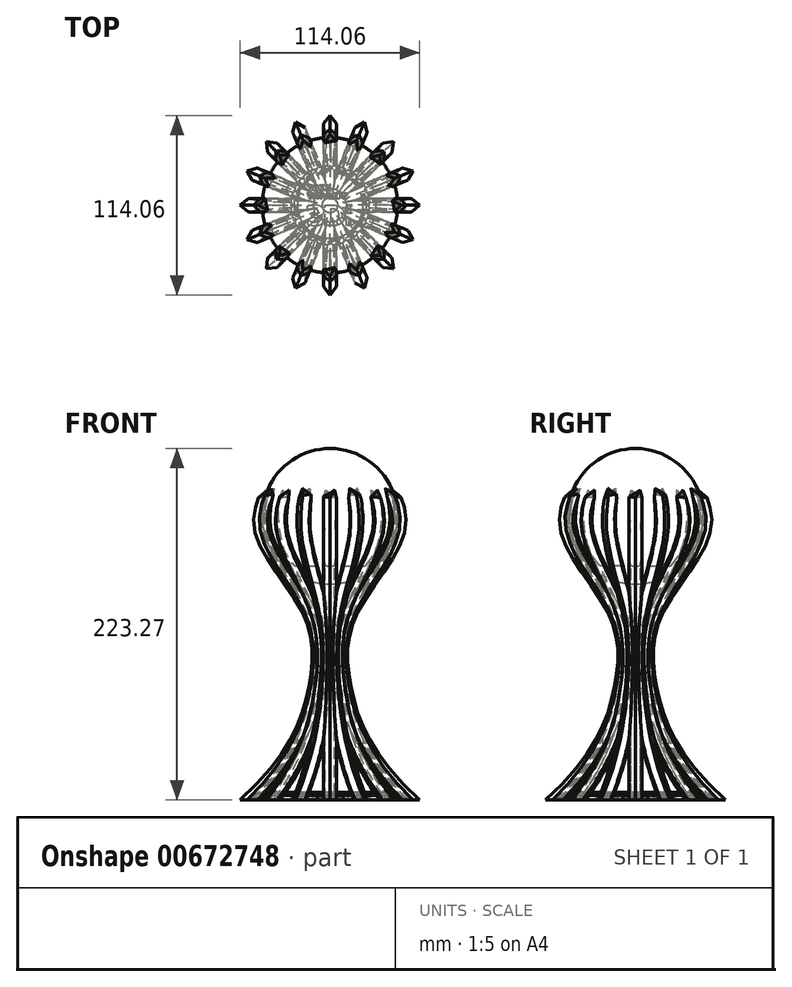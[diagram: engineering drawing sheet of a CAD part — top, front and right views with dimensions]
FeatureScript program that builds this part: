
annotation { "Feature Type Name" : "Feature", "Feature Type Description" : "" }
export const myFeature = defineFeature(function(context is Context, id is Id, definition is map)
    precondition{}
    {
        {
            var Q0;
            Q0=qCreatedBy(makeId("Front.planeOp"),FACE);
            var sketch = newSketch(context, id + "F0", { "sketchPlane" : qUnion([Q0])});
            skCircle(sketch, "E0", {"center": v(-0.22, 180.27) * mm, "radius": 43 * mm});
            skLineSegment(sketch, "E1", {"start": v(-0.22, 249.8) * mm, "end": v(-0.22, -3.53) * mm, "construction": true});
            skLineSegment(sketch, "E2", {"start": v(94.67, 200) * mm, "end": v(-91.24, 200) * mm, "construction": true});
            skFitSpline(sketch, "E3", {"points": [v(-37.53, 197.97) * mm, v(-44.72, 173.88) * mm, v(-14.42, 119.99) * mm, v(-10.02, 72.07) * mm, v(-52.16, 0) * mm], "startDerivative": vector(-55.72, -57.4) * mm, "endDerivative": vector(-278.7, -261.6) * mm});
            skLineSegment(sketch, "E4", {"start": v(-0.22, 180.27) * mm, "end": v(-70.32, 183.44) * mm, "construction": true});
            skLineSegment(sketch, "E5", {"start": v(-0.22, 223.27) * mm, "end": v(-0.22, 137.27) * mm});
            skSolve(sketch);
        }
        {
            var Q0;
            Q0=qCreatedBy(makeId("Top.planeOp"),FACE);
            var sketch = newSketch(context, id + "F1", { "sketchPlane" : qUnion([Q0])});
            skPoint(sketch, "E6.0", {"position": v(-52.16, 0) * mm});
            skCircle(sketch, "E7", {"center": v(0, 0) * mm, "radius": 52.16 * mm, "construction": true});
            skLineSegment(sketch, "E8", {"start": v(-50.09, -4.18) * mm, "end": v(-52, -4.18) * mm});
            skLineSegment(sketch, "E9", {"start": v(-52, -4.18) * mm, "end": v(-57.25, 0) * mm});
            skLineSegment(sketch, "E10", {"start": v(-49.1, 0) * mm, "end": v(-61.73, 0) * mm, "construction": true});
            skLineSegment(sketch, "E11.MirrorCS", {"start": v(-50.09, 4.18) * mm, "end": v(-52, 4.18) * mm});
            skLineSegment(sketch, "E12.MirrorCS", {"start": v(-52, 4.18) * mm, "end": v(-57.25, 0) * mm});
            skLineSegment(sketch, "E13", {"start": v(-50.09, -4.18) * mm, "end": v(-47.88, -3.04) * mm});
            skLineSegment(sketch, "E14", {"start": v(-47.88, -3.04) * mm, "end": v(-47.88, 0) * mm});
            skLineSegment(sketch, "E15.MirrorCS", {"start": v(-47.88, 3.04) * mm, "end": v(-47.88, 0) * mm});
            skLineSegment(sketch, "E16.MirrorCS", {"start": v(-50.09, 4.18) * mm, "end": v(-47.88, 3.04) * mm});
            skPoint(sketch, "E17.start.orphan", {"position": v(-51.12, 0) * mm});
            skPoint(sketch, "E18.MirrorCS.end.orphan", {"position": v(-50.09, 4.18) * mm});
            skSolve(sketch);
        }
        {
            var Q0;
            Q0=makeQuery(id+"F1.imprint","IMPRINT",FACE,{"disambiguationData":[TD([[makeQuery(id+"F1.imprint","IMPRINT",EDGE,{"derivedFrom":sQuery(id+"F1.wireOp",EDGE,"E8")}),-1.0]])]});
            var Q1;
            Q1=sQuery(id+"F0.wireOp",EDGE,"E3");
            sweep(context, id + "F2", {"profiles" : qUnion([Q0]), "path" : qUnion([Q1])});
        }
        {
            var Q0;
            Q0=makeQuery(id+"F2.opSweep","SWEPT_BODY",BODY,{"disambiguationData":[OSD([sQuery(id+"F0.wireOp",EDGE,"E3"),sQuery(id+"F1.wireOp",EDGE,"DaZxr78I-HaZT-GVOq-y3KG-bkiKTm5bVj2K"),sQuery(id+"F1.wireOp",EDGE,"ID9TlmXJ-H8h3-IZLx-eHvp-f0HMO6DgMMxN"),sQuery(id+"F1.wireOp",EDGE,"5A4HRRGu-b9xE-CkS7-00Gs-tnyZgG4T912Z"),sQuery(id+"F1.wireOp",EDGE,"uolo1fji-ynfm-Myvc-62LO-FXYa9UhFNky3"),sQuery(id+"F1.wireOp",EDGE,"E17"),sQuery(id+"F1.wireOp",EDGE,"E8"),sQuery(id+"F1.wireOp",EDGE,"E9")])]});
            var Q1;
            Q1=sQuery(id+"F0.wireOp",EDGE,"E1");
            circularPattern(context, id + "F3", {"operationType" : NewBodyOperationType.ADD, "entities" : qUnion([Q0]), "axis" : qUnion([Q1]), "angle" : 360 * degree, "instanceCount" : 16, "equalSpace" : true, "isCentered" : true});
        }
        {
            var Q0;
            {var subQ2=sQuery(id+"F0.wireOp",EDGE,"E5");Q0=makeQuery(id+"F0.imprint","IMPRINT",FACE,{"disambiguationData":[TD([[makeQuery(id+"F0.imprint","IMPRINT",EDGE,{"derivedFrom":subQ2}),-1.0]])]});}
            var Q1;
            Q1=sQuery(id+"F0.wireOp",EDGE,"E1");
            revolve(context, id + "F4", {"entities" : qUnion([Q0]), "axis" : qUnion([Q1]), "revolveType" : RevolveType.FULL});
        }
        {
            var Q0;
            Q0=makeQuery(id+"F3.opPattern","COPY",EDGE,{"derivedFrom":makeQuery(id+"F2.opSweep","CAP_EDGE",EDGE,{"disambiguationData":[OSD([sQuery(id+"F0.wireOp",VERTEX,"E3.start"),sQuery(id+"F1.wireOp",EDGE,"E9")])],"isStart":false}),"instanceName":"-7"});
            var Q1;
            Q1=makeQuery(id+"F3.opPattern","COPY",EDGE,{"derivedFrom":makeQuery(id+"F2.opSweep","CAP_EDGE",EDGE,{"disambiguationData":[OSD([sQuery(id+"F0.wireOp",VERTEX,"E3.start"),sQuery(id+"F1.wireOp",EDGE,"E9")])],"isStart":false}),"instanceName":"-9"});
            var Q2;
            Q2=makeQuery(id+"F3.opPattern","COPY",EDGE,{"derivedFrom":makeQuery(id+"F2.opSweep","CAP_EDGE",EDGE,{"disambiguationData":[OSD([sQuery(id+"F0.wireOp",VERTEX,"E3.start"),sQuery(id+"F1.wireOp",EDGE,"E9")])],"isStart":false}),"instanceName":"-11"});
            var Q3;
            Q3=makeQuery(id+"F3.opPattern","COPY",EDGE,{"derivedFrom":makeQuery(id+"F2.opSweep","CAP_EDGE",EDGE,{"disambiguationData":[OSD([sQuery(id+"F0.wireOp",VERTEX,"E3.start"),sQuery(id+"F1.wireOp",EDGE,"E9")])],"isStart":false}),"instanceName":"-13"});
            var Q4;
            Q4=makeQuery(id+"F3.opPattern","COPY",EDGE,{"derivedFrom":makeQuery(id+"F2.opSweep","CAP_EDGE",EDGE,{"disambiguationData":[OSD([sQuery(id+"F0.wireOp",VERTEX,"E3.start"),sQuery(id+"F1.wireOp",EDGE,"E9")])],"isStart":false}),"instanceName":"-15"});
            var Q5;
            Q5=makeQuery(id+"F3.opPattern","COPY",EDGE,{"derivedFrom":makeQuery(id+"F2.opSweep","CAP_EDGE",EDGE,{"disambiguationData":[OSD([sQuery(id+"F0.wireOp",VERTEX,"E3.start"),sQuery(id+"F1.wireOp",EDGE,"E9")])],"isStart":false}),"instanceName":"-1"});
            var Q6;
            Q6=makeQuery(id+"F3.opPattern","COPY",EDGE,{"derivedFrom":makeQuery(id+"F2.opSweep","CAP_EDGE",EDGE,{"disambiguationData":[OSD([sQuery(id+"F0.wireOp",VERTEX,"E3.start"),sQuery(id+"F1.wireOp",EDGE,"E9")])],"isStart":false}),"instanceName":"-3"});
            var Q7;
            Q7=makeQuery(id+"F3.opPattern","COPY",EDGE,{"derivedFrom":makeQuery(id+"F2.opSweep","CAP_EDGE",EDGE,{"disambiguationData":[OSD([sQuery(id+"F0.wireOp",VERTEX,"E3.start"),sQuery(id+"F1.wireOp",EDGE,"E9")])],"isStart":false}),"instanceName":"-5"});
            chamfer(context, id + "F5", {"entities" : qUnion([Q0, Q1, Q2, Q3, Q4, Q5, Q6, Q7]), "width" : 6 * mm, "tangentPropagation" : true});
        }
        {
            var Q0;
            Q0=makeQuery(id+"F3.opPattern","COPY",EDGE,{"derivedFrom":makeQuery(id+"F2.opSweep","CAP_EDGE",EDGE,{"disambiguationData":[OSD([sQuery(id+"F0.wireOp",VERTEX,"E3.start"),sQuery(id+"F1.wireOp",EDGE,"E12.MirrorCS")])],"isStart":false}),"instanceName":"-4"});
            var Q1;
            Q1=makeQuery(id+"F3.opPattern","COPY",EDGE,{"derivedFrom":makeQuery(id+"F2.opSweep","CAP_EDGE",EDGE,{"disambiguationData":[OSD([sQuery(id+"F0.wireOp",VERTEX,"E3.start"),sQuery(id+"F1.wireOp",EDGE,"E12.MirrorCS")])],"isStart":false}),"instanceName":"-6"});
            var Q2;
            Q2=makeQuery(id+"F3.opPattern","COPY",EDGE,{"derivedFrom":makeQuery(id+"F2.opSweep","CAP_EDGE",EDGE,{"disambiguationData":[OSD([sQuery(id+"F0.wireOp",VERTEX,"E3.start"),sQuery(id+"F1.wireOp",EDGE,"E12.MirrorCS")])],"isStart":false}),"instanceName":"-8"});
            var Q3;
            Q3=makeQuery(id+"F3.opPattern","COPY",EDGE,{"derivedFrom":makeQuery(id+"F2.opSweep","CAP_EDGE",EDGE,{"disambiguationData":[OSD([sQuery(id+"F0.wireOp",VERTEX,"E3.start"),sQuery(id+"F1.wireOp",EDGE,"E12.MirrorCS")])],"isStart":false}),"instanceName":"-10"});
            var Q4;
            Q4=makeQuery(id+"F3.opPattern","COPY",EDGE,{"derivedFrom":makeQuery(id+"F2.opSweep","CAP_EDGE",EDGE,{"disambiguationData":[OSD([sQuery(id+"F0.wireOp",VERTEX,"E3.start"),sQuery(id+"F1.wireOp",EDGE,"E12.MirrorCS")])],"isStart":false}),"instanceName":"-12"});
            var Q5;
            Q5=makeQuery(id+"F3.opPattern","COPY",EDGE,{"derivedFrom":makeQuery(id+"F2.opSweep","CAP_EDGE",EDGE,{"disambiguationData":[OSD([sQuery(id+"F0.wireOp",VERTEX,"E3.start"),sQuery(id+"F1.wireOp",EDGE,"E12.MirrorCS")])],"isStart":false}),"instanceName":"-14"});
            var Q6;
            Q6=makeQuery(id+"F2.opSweep","CAP_EDGE",EDGE,{"disambiguationData":[OSD([sQuery(id+"F0.wireOp",VERTEX,"E3.start"),sQuery(id+"F1.wireOp",EDGE,"E12.MirrorCS")])],"isStart":false});
            var Q7;
            Q7=makeQuery(id+"F3.opPattern","COPY",EDGE,{"derivedFrom":makeQuery(id+"F2.opSweep","CAP_EDGE",EDGE,{"disambiguationData":[OSD([sQuery(id+"F0.wireOp",VERTEX,"E3.start"),sQuery(id+"F1.wireOp",EDGE,"E12.MirrorCS")])],"isStart":false}),"instanceName":"-2"});
            chamfer(context, id + "F6", {"entities" : qUnion([Q0, Q1, Q2, Q3, Q4, Q5, Q6, Q7]), "width" : 8 * mm, "tangentPropagation" : true});
        }
        {
            var Q0;
            Q0=qCreatedBy(makeId("Top.planeOp"),FACE);
            var sketch = newSketch(context, id + "F7", { "sketchPlane" : qUnion([Q0])});
            skArc(sketch, "E19", {"start": v(-24.95, -1.58) * mm, "mid": v(-24.52, -4.88) * mm, "end": v(-23.66, -8.09) * mm});
            skPoint(sketch, "E20.0", {"position": v(-52.16, 0) * mm});
            skCircle(sketch, "E21.cCircle", {"center": v(0, 0) * mm, "radius": 52.16 * mm, "construction": true});
            skLineSegment(sketch, "E21.0", {"start": v(-52.16, 0) * mm, "end": v(-48.19, 19.96) * mm});
            skLineSegment(sketch, "E21.1", {"start": v(-48.19, 19.96) * mm, "end": v(-36.88, 36.88) * mm});
            skLineSegment(sketch, "E21.2", {"start": v(-36.88, 36.88) * mm, "end": v(-19.96, 48.19) * mm});
            skLineSegment(sketch, "E21.3", {"start": v(-19.96, 48.19) * mm, "end": v(0, 52.16) * mm});
            skLineSegment(sketch, "E21.4", {"start": v(0, 52.16) * mm, "end": v(19.96, 48.19) * mm});
            skLineSegment(sketch, "E21.5", {"start": v(19.96, 48.19) * mm, "end": v(36.88, 36.88) * mm});
            skLineSegment(sketch, "E21.6", {"start": v(36.88, 36.88) * mm, "end": v(48.19, 19.96) * mm});
            skLineSegment(sketch, "E21.7", {"start": v(48.19, 19.96) * mm, "end": v(52.16, 0) * mm});
            skLineSegment(sketch, "E21.8", {"start": v(52.16, 0) * mm, "end": v(48.19, -19.96) * mm});
            skLineSegment(sketch, "E21.9", {"start": v(48.19, -19.96) * mm, "end": v(36.88, -36.88) * mm});
            skLineSegment(sketch, "E21.10", {"start": v(36.88, -36.88) * mm, "end": v(19.96, -48.19) * mm});
            skLineSegment(sketch, "E21.11", {"start": v(19.96, -48.19) * mm, "end": v(0, -52.16) * mm});
            skLineSegment(sketch, "E21.12", {"start": v(0, -52.16) * mm, "end": v(-19.96, -48.19) * mm});
            skLineSegment(sketch, "E21.13", {"start": v(-19.96, -48.19) * mm, "end": v(-36.88, -36.88) * mm});
            skLineSegment(sketch, "E21.14", {"start": v(-36.88, -36.88) * mm, "end": v(-48.19, -19.96) * mm});
            skLineSegment(sketch, "E21.15", {"start": v(-48.19, -19.96) * mm, "end": v(-52.16, 0) * mm});
            skPoint(sketch, "E22.0", {"position": v(-47.88, 3.04) * mm});
            skPoint(sketch, "E23.0", {"position": v(-47.88, -3.04) * mm});
            skPoint(sketch, "E24.0", {"position": v(-47.88, 0) * mm});
            skLineSegment(sketch, "E25", {"start": v(-47.88, 3.04) * mm, "end": v(-24.95, 1.58) * mm});
            skLineSegment(sketch, "E26", {"start": v(-47.88, -3.04) * mm, "end": v(-24.95, -1.58) * mm});
            skLineSegment(sketch, "E27", {"start": v(-47.88, 3.04) * mm, "end": v(-52.16, 0) * mm});
            skLineSegment(sketch, "E28", {"start": v(-52.16, 0) * mm, "end": v(-47.88, -3.04) * mm});
            skCircle(sketch, "E29", {"center": v(0, 0) * mm, "radius": 21 * mm});
            skLineSegment(sketch, "E30.1.0", {"start": v(-45.4, -15.52) * mm, "end": v(-23.66, -8.09) * mm});
            skLineSegment(sketch, "E30.1.1", {"start": v(-45.4, -15.52) * mm, "end": v(-48.19, -19.96) * mm});
            skLineSegment(sketch, "E30.1.2", {"start": v(-48.19, -19.96) * mm, "end": v(-43.08, -21.13) * mm});
            skLineSegment(sketch, "E30.1.3", {"start": v(-43.08, -21.13) * mm, "end": v(-22.45, -11) * mm});
            skLineSegment(sketch, "E30.2.0", {"start": v(-36, -31.71) * mm, "end": v(-18.76, -16.52) * mm});
            skLineSegment(sketch, "E30.2.1", {"start": v(-36, -31.71) * mm, "end": v(-36.88, -36.88) * mm});
            skLineSegment(sketch, "E30.2.2", {"start": v(-36.88, -36.88) * mm, "end": v(-31.71, -36) * mm});
            skLineSegment(sketch, "E30.2.3", {"start": v(-31.71, -36) * mm, "end": v(-16.52, -18.76) * mm});
            skLineSegment(sketch, "E30.3.0", {"start": v(-21.13, -43.08) * mm, "end": v(-11, -22.45) * mm});
            skLineSegment(sketch, "E30.3.1", {"start": v(-21.13, -43.08) * mm, "end": v(-19.96, -48.19) * mm});
            skLineSegment(sketch, "E30.3.2", {"start": v(-19.96, -48.19) * mm, "end": v(-15.52, -45.4) * mm});
            skLineSegment(sketch, "E30.3.3", {"start": v(-15.52, -45.4) * mm, "end": v(-8.09, -23.66) * mm});
            skLineSegment(sketch, "E30.4.0", {"start": v(-3.04, -47.88) * mm, "end": v(-1.58, -24.95) * mm});
            skLineSegment(sketch, "E30.4.1", {"start": v(-3.04, -47.88) * mm, "end": v(0, -52.16) * mm});
            skLineSegment(sketch, "E30.4.2", {"start": v(0, -52.16) * mm, "end": v(3.04, -47.88) * mm});
            skLineSegment(sketch, "E30.4.3", {"start": v(3.04, -47.88) * mm, "end": v(1.58, -24.95) * mm});
            skLineSegment(sketch, "E30.5.0", {"start": v(15.52, -45.4) * mm, "end": v(8.09, -23.66) * mm});
            skLineSegment(sketch, "E30.5.1", {"start": v(15.52, -45.4) * mm, "end": v(19.96, -48.19) * mm});
            skLineSegment(sketch, "E30.5.2", {"start": v(19.96, -48.19) * mm, "end": v(21.13, -43.08) * mm});
            skLineSegment(sketch, "E30.5.3", {"start": v(21.13, -43.08) * mm, "end": v(11, -22.45) * mm});
            skLineSegment(sketch, "E30.6.0", {"start": v(31.71, -36) * mm, "end": v(16.52, -18.76) * mm});
            skLineSegment(sketch, "E30.6.1", {"start": v(31.71, -36) * mm, "end": v(36.88, -36.88) * mm});
            skLineSegment(sketch, "E30.6.2", {"start": v(36.88, -36.88) * mm, "end": v(36, -31.71) * mm});
            skLineSegment(sketch, "E30.6.3", {"start": v(36, -31.71) * mm, "end": v(18.76, -16.52) * mm});
            skLineSegment(sketch, "E30.7.0", {"start": v(43.08, -21.13) * mm, "end": v(22.45, -11) * mm});
            skLineSegment(sketch, "E30.7.1", {"start": v(43.08, -21.13) * mm, "end": v(48.19, -19.96) * mm});
            skLineSegment(sketch, "E30.7.2", {"start": v(48.19, -19.96) * mm, "end": v(45.4, -15.52) * mm});
            skLineSegment(sketch, "E30.7.3", {"start": v(45.4, -15.52) * mm, "end": v(23.66, -8.09) * mm});
            skLineSegment(sketch, "E30.8.0", {"start": v(47.88, -3.04) * mm, "end": v(24.95, -1.58) * mm});
            skLineSegment(sketch, "E30.8.1", {"start": v(47.88, -3.04) * mm, "end": v(52.16, 0) * mm});
            skLineSegment(sketch, "E30.8.2", {"start": v(52.16, 0) * mm, "end": v(47.88, 3.04) * mm});
            skLineSegment(sketch, "E30.8.3", {"start": v(47.88, 3.04) * mm, "end": v(24.95, 1.58) * mm});
            skLineSegment(sketch, "E30.9.0", {"start": v(45.4, 15.52) * mm, "end": v(23.66, 8.09) * mm});
            skLineSegment(sketch, "E30.9.1", {"start": v(45.4, 15.52) * mm, "end": v(48.19, 19.96) * mm});
            skLineSegment(sketch, "E30.9.2", {"start": v(48.19, 19.96) * mm, "end": v(43.08, 21.13) * mm});
            skLineSegment(sketch, "E30.9.3", {"start": v(43.08, 21.13) * mm, "end": v(22.45, 11) * mm});
            skLineSegment(sketch, "E30.10.0", {"start": v(36, 31.71) * mm, "end": v(18.76, 16.52) * mm});
            skLineSegment(sketch, "E30.10.1", {"start": v(36, 31.71) * mm, "end": v(36.88, 36.88) * mm});
            skLineSegment(sketch, "E30.10.2", {"start": v(36.88, 36.88) * mm, "end": v(31.71, 36) * mm});
            skLineSegment(sketch, "E30.10.3", {"start": v(31.71, 36) * mm, "end": v(16.52, 18.76) * mm});
            skLineSegment(sketch, "E30.11.0", {"start": v(21.13, 43.08) * mm, "end": v(11, 22.45) * mm});
            skLineSegment(sketch, "E30.11.1", {"start": v(21.13, 43.08) * mm, "end": v(19.96, 48.19) * mm});
            skLineSegment(sketch, "E30.11.2", {"start": v(19.96, 48.19) * mm, "end": v(15.52, 45.4) * mm});
            skLineSegment(sketch, "E30.11.3", {"start": v(15.52, 45.4) * mm, "end": v(8.09, 23.66) * mm});
            skLineSegment(sketch, "E30.12.0", {"start": v(3.04, 47.88) * mm, "end": v(1.58, 24.95) * mm});
            skLineSegment(sketch, "E30.12.1", {"start": v(3.04, 47.88) * mm, "end": v(0, 52.16) * mm});
            skLineSegment(sketch, "E30.12.2", {"start": v(0, 52.16) * mm, "end": v(-3.04, 47.88) * mm});
            skLineSegment(sketch, "E30.12.3", {"start": v(-3.04, 47.88) * mm, "end": v(-1.58, 24.95) * mm});
            skLineSegment(sketch, "E30.13.0", {"start": v(-15.52, 45.4) * mm, "end": v(-8.09, 23.66) * mm});
            skLineSegment(sketch, "E30.13.1", {"start": v(-15.52, 45.4) * mm, "end": v(-19.96, 48.19) * mm});
            skLineSegment(sketch, "E30.13.2", {"start": v(-19.96, 48.19) * mm, "end": v(-21.13, 43.08) * mm});
            skLineSegment(sketch, "E30.13.3", {"start": v(-21.13, 43.08) * mm, "end": v(-11, 22.45) * mm});
            skLineSegment(sketch, "E30.14.0", {"start": v(-31.71, 36) * mm, "end": v(-16.52, 18.76) * mm});
            skLineSegment(sketch, "E30.14.1", {"start": v(-31.71, 36) * mm, "end": v(-36.88, 36.88) * mm});
            skLineSegment(sketch, "E30.14.2", {"start": v(-36.88, 36.88) * mm, "end": v(-36, 31.71) * mm});
            skLineSegment(sketch, "E30.14.3", {"start": v(-36, 31.71) * mm, "end": v(-18.76, 16.52) * mm});
            skLineSegment(sketch, "E30.15.0", {"start": v(-43.08, 21.13) * mm, "end": v(-22.45, 11) * mm});
            skLineSegment(sketch, "E30.15.1", {"start": v(-43.08, 21.13) * mm, "end": v(-48.19, 19.96) * mm});
            skLineSegment(sketch, "E30.15.2", {"start": v(-48.19, 19.96) * mm, "end": v(-45.4, 15.52) * mm});
            skLineSegment(sketch, "E30.15.3", {"start": v(-45.4, 15.52) * mm, "end": v(-23.66, 8.09) * mm});
            skArc(sketch, "E31.trimOffspring", {"start": v(-23.66, 8.09) * mm, "mid": v(-24.52, 4.88) * mm, "end": v(-24.95, 1.58) * mm});
            skArc(sketch, "E32.trimOffspring", {"start": v(-18.76, 16.52) * mm, "mid": v(-20.79, 13.89) * mm, "end": v(-22.45, 11) * mm});
            skArc(sketch, "E33.trimOffspring", {"start": v(-11, 22.45) * mm, "mid": v(-13.89, 20.79) * mm, "end": v(-16.52, 18.76) * mm});
            skArc(sketch, "E34.trimOffspring", {"start": v(-1.58, 24.95) * mm, "mid": v(-4.88, 24.52) * mm, "end": v(-8.09, 23.66) * mm});
            skArc(sketch, "E35.trimOffspring", {"start": v(8.09, 23.66) * mm, "mid": v(4.88, 24.52) * mm, "end": v(1.58, 24.95) * mm});
            skArc(sketch, "E36.trimOffspring", {"start": v(16.52, 18.76) * mm, "mid": v(13.89, 20.79) * mm, "end": v(11, 22.45) * mm});
            skArc(sketch, "E37.trimOffspring", {"start": v(22.45, 11) * mm, "mid": v(20.79, 13.89) * mm, "end": v(18.76, 16.52) * mm});
            skArc(sketch, "E38.trimOffspring", {"start": v(24.95, 1.58) * mm, "mid": v(24.52, 4.88) * mm, "end": v(23.66, 8.09) * mm});
            skArc(sketch, "E39.trimOffspring", {"start": v(23.66, -8.09) * mm, "mid": v(24.52, -4.88) * mm, "end": v(24.95, -1.58) * mm});
            skArc(sketch, "E40.trimOffspring", {"start": v(18.76, -16.52) * mm, "mid": v(20.79, -13.89) * mm, "end": v(22.45, -11) * mm});
            skArc(sketch, "E41.trimOffspring", {"start": v(11, -22.45) * mm, "mid": v(13.89, -20.79) * mm, "end": v(16.52, -18.76) * mm});
            skArc(sketch, "E42.trimOffspring", {"start": v(1.58, -24.95) * mm, "mid": v(4.88, -24.52) * mm, "end": v(8.09, -23.66) * mm});
            skArc(sketch, "E43.trimOffspring", {"start": v(-8.09, -23.66) * mm, "mid": v(-4.88, -24.52) * mm, "end": v(-1.58, -24.95) * mm});
            skArc(sketch, "E44.trimOffspring", {"start": v(-16.52, -18.76) * mm, "mid": v(-13.89, -20.79) * mm, "end": v(-11, -22.45) * mm});
            skArc(sketch, "E45.trimOffspring", {"start": v(-22.45, -11) * mm, "mid": v(-20.79, -13.89) * mm, "end": v(-18.76, -16.52) * mm});
            skSolve(sketch);
        }
        {
            var Q0;
            Q0=makeQuery(id+"F7.imprint","IMPRINT",FACE,{"disambiguationData":[TD([[makeQuery(id+"F7.imprint","IMPRINT",EDGE,{"derivedFrom":sQuery(id+"F7.wireOp",EDGE,"E19")}),1.0]])]});
            extrude(context, id + "F8", {"entities" : qUnion([Q0]), "operationType" : NewBodyOperationType.ADD, "depth" : 3 * mm, "offsetDistance" : 25 * mm, "hasDraft" : true, "draftAngle" : 3.8 * degree});
        }
        {
            var Q0;
            Q0=makeQuery(id+"F8.opExtrude","CAP_FACE",FACE,{"disambiguationData":[OSD([sQuery(id+"F7.wireOp",EDGE,"E19"),sQuery(id+"F7.wireOp",EDGE,"E25"),sQuery(id+"F7.wireOp",EDGE,"E26"),sQuery(id+"F7.wireOp",EDGE,"E27"),sQuery(id+"F7.wireOp",EDGE,"E28"),sQuery(id+"F7.wireOp",EDGE,"E29"),sQuery(id+"F7.wireOp",EDGE,"E30.1.0"),sQuery(id+"F7.wireOp",EDGE,"E30.1.1"),sQuery(id+"F7.wireOp",EDGE,"E30.1.2"),sQuery(id+"F7.wireOp",EDGE,"E30.1.3"),sQuery(id+"F7.wireOp",EDGE,"E30.2.0"),sQuery(id+"F7.wireOp",EDGE,"E30.2.1"),sQuery(id+"F7.wireOp",EDGE,"E30.2.2"),sQuery(id+"F7.wireOp",EDGE,"E30.2.3"),sQuery(id+"F7.wireOp",EDGE,"E30.3.0"),sQuery(id+"F7.wireOp",EDGE,"E30.3.1"),sQuery(id+"F7.wireOp",EDGE,"E30.3.2"),sQuery(id+"F7.wireOp",EDGE,"E30.3.3"),sQuery(id+"F7.wireOp",EDGE,"E30.4.0"),sQuery(id+"F7.wireOp",EDGE,"E30.4.1"),sQuery(id+"F7.wireOp",EDGE,"E30.4.2"),sQuery(id+"F7.wireOp",EDGE,"E30.4.3"),sQuery(id+"F7.wireOp",EDGE,"E30.5.0"),sQuery(id+"F7.wireOp",EDGE,"E30.5.1"),sQuery(id+"F7.wireOp",EDGE,"E30.5.2"),sQuery(id+"F7.wireOp",EDGE,"E30.5.3"),sQuery(id+"F7.wireOp",EDGE,"E30.6.0"),sQuery(id+"F7.wireOp",EDGE,"E30.6.1"),sQuery(id+"F7.wireOp",EDGE,"E30.6.2"),sQuery(id+"F7.wireOp",EDGE,"E30.6.3"),sQuery(id+"F7.wireOp",EDGE,"E30.7.0"),sQuery(id+"F7.wireOp",EDGE,"E30.7.1"),sQuery(id+"F7.wireOp",EDGE,"E30.7.2"),sQuery(id+"F7.wireOp",EDGE,"E30.7.3"),sQuery(id+"F7.wireOp",EDGE,"E30.8.0"),sQuery(id+"F7.wireOp",EDGE,"E30.8.1"),sQuery(id+"F7.wireOp",EDGE,"E30.8.2"),sQuery(id+"F7.wireOp",EDGE,"E30.8.3"),sQuery(id+"F7.wireOp",EDGE,"E30.9.0"),sQuery(id+"F7.wireOp",EDGE,"E30.9.1"),sQuery(id+"F7.wireOp",EDGE,"E30.9.2"),sQuery(id+"F7.wireOp",EDGE,"E30.9.3"),sQuery(id+"F7.wireOp",EDGE,"E30.10.0"),sQuery(id+"F7.wireOp",EDGE,"E30.10.1"),sQuery(id+"F7.wireOp",EDGE,"E30.10.2"),sQuery(id+"F7.wireOp",EDGE,"E30.10.3"),sQuery(id+"F7.wireOp",EDGE,"E30.11.0"),sQuery(id+"F7.wireOp",EDGE,"E30.11.1"),sQuery(id+"F7.wireOp",EDGE,"E30.11.2"),sQuery(id+"F7.wireOp",EDGE,"E30.11.3"),sQuery(id+"F7.wireOp",EDGE,"E30.12.0"),sQuery(id+"F7.wireOp",EDGE,"E30.12.1"),sQuery(id+"F7.wireOp",EDGE,"E30.12.2"),sQuery(id+"F7.wireOp",EDGE,"E30.12.3"),sQuery(id+"F7.wireOp",EDGE,"E30.13.0"),sQuery(id+"F7.wireOp",EDGE,"E30.13.1"),sQuery(id+"F7.wireOp",EDGE,"E30.13.2"),sQuery(id+"F7.wireOp",EDGE,"E30.13.3"),sQuery(id+"F7.wireOp",EDGE,"E30.14.0"),sQuery(id+"F7.wireOp",EDGE,"E30.14.1"),sQuery(id+"F7.wireOp",EDGE,"E30.14.2"),sQuery(id+"F7.wireOp",EDGE,"E30.14.3"),sQuery(id+"F7.wireOp",EDGE,"E30.15.0"),sQuery(id+"F7.wireOp",EDGE,"E30.15.1"),sQuery(id+"F7.wireOp",EDGE,"E30.15.2"),sQuery(id+"F7.wireOp",EDGE,"E30.15.3"),sQuery(id+"F7.wireOp",EDGE,"E31.trimOffspring"),sQuery(id+"F7.wireOp",EDGE,"E32.trimOffspring"),sQuery(id+"F7.wireOp",EDGE,"E33.trimOffspring"),sQuery(id+"F7.wireOp",EDGE,"E34.trimOffspring"),sQuery(id+"F7.wireOp",EDGE,"E35.trimOffspring"),sQuery(id+"F7.wireOp",EDGE,"E36.trimOffspring"),sQuery(id+"F7.wireOp",EDGE,"E37.trimOffspring"),sQuery(id+"F7.wireOp",EDGE,"E38.trimOffspring"),sQuery(id+"F7.wireOp",EDGE,"E39.trimOffspring"),sQuery(id+"F7.wireOp",EDGE,"E40.trimOffspring"),sQuery(id+"F7.wireOp",EDGE,"E41.trimOffspring"),sQuery(id+"F7.wireOp",EDGE,"E42.trimOffspring"),sQuery(id+"F7.wireOp",EDGE,"E43.trimOffspring"),sQuery(id+"F7.wireOp",EDGE,"E44.trimOffspring"),sQuery(id+"F7.wireOp",EDGE,"E45.trimOffspring")])],"isStart":false});
            extrude(context, id + "F9", {"entities" : qUnion([Q0]), "operationType" : NewBodyOperationType.ADD, "depth" : 2 * mm, "offsetDistance" : 25 * mm, "hasDraft" : true, "draftAngle" : 50 * degree, "draftPullDirection" : true});
        }
        {
            var Q0;
            Q0=makeQuery(id+"F8.opExtrude","CAP_EDGE",EDGE,{"disambiguationData":[OSD([sQuery(id+"F7.wireOp",EDGE,"E29")])],"isStart":true});
            chamfer(context, id + "F10", {"entities" : qUnion([Q0]), "chamferType" : ChamferType.TWO_OFFSETS, "width1" : 1 * mm, "oppositeDirection" : false, "width2" : 2 * mm, "tangentPropagation" : true});
        }
        {
            var Q0;
            Q0=makeQuery(id+"F4.opRevolve","SWEPT_BODY",BODY,{"disambiguationData":[OSD([sQuery(id+"F0.wireOp",EDGE,"E0"),sQuery(id+"F0.wireOp",EDGE,"0JXTtzD2-2VzW-rgRp-cltN-5Cip2ue7kMV8")])]});
            var Q1;
            Q1=makeQuery(id+"F2.opSweep","SWEPT_BODY",BODY,{"disambiguationData":[OSD([sQuery(id+"F0.wireOp",EDGE,"E3"),sQuery(id+"F1.wireOp",EDGE,"E8"),sQuery(id+"F1.wireOp",EDGE,"E9"),sQuery(id+"F1.wireOp",EDGE,"E11.MirrorCS"),sQuery(id+"F1.wireOp",EDGE,"E12.MirrorCS"),sQuery(id+"F1.wireOp",EDGE,"E13"),sQuery(id+"F1.wireOp",EDGE,"E14"),sQuery(id+"F1.wireOp",EDGE,"E15.MirrorCS"),sQuery(id+"F1.wireOp",EDGE,"E16.MirrorCS")])]});
            booleanBodies(context, id + "F11", {"operationType" : BooleanOperationType.SUBTRACTION, "tools" : qUnion([Q0]), "targets" : qUnion([Q1]), "keepTools" : true});
        }
        {
            var Q0;
            Q0=qCreatedBy(makeId("Top.planeOp"),FACE);
            var sketch = newSketch(context, id + "F12", { "sketchPlane" : qUnion([Q0])});
            skCircle(sketch, "E46.0", {"center": v(0, 0) * mm, "radius": 22 * mm});
            skSolve(sketch);
        }
        {
            var Q0;
            Q0=makeQuery(id+"F12.imprint","IMPRINT",FACE,{"disambiguationData":[TD([[makeQuery(id+"F12.imprint","IMPRINT",EDGE,{"derivedFrom":sQuery(id+"F12.wireOp",EDGE,"E46.0")}),1.0]])]});
            extrude(context, id + "F13", {"entities" : qUnion([Q0]), "depth" : 3 * mm, "offsetDistance" : 25 * mm});
        }
        {
            var Q0;
            Q0=makeQuery(id+"F2.opSweep","SWEPT_BODY",BODY,{"disambiguationData":[OSD([sQuery(id+"F0.wireOp",EDGE,"E3"),sQuery(id+"F1.wireOp",EDGE,"E8"),sQuery(id+"F1.wireOp",EDGE,"E9"),sQuery(id+"F1.wireOp",EDGE,"E11.MirrorCS"),sQuery(id+"F1.wireOp",EDGE,"E12.MirrorCS"),sQuery(id+"F1.wireOp",EDGE,"E13"),sQuery(id+"F1.wireOp",EDGE,"E14"),sQuery(id+"F1.wireOp",EDGE,"E15.MirrorCS"),sQuery(id+"F1.wireOp",EDGE,"E16.MirrorCS")])]});
            var Q1;
            Q1=makeQuery(id+"F13.opExtrude","SWEPT_BODY",BODY,{"disambiguationData":[OSD([sQuery(id+"F12.wireOp",EDGE,"E46.0")])]});
            booleanBodies(context, id + "F14", {"operationType" : BooleanOperationType.SUBTRACTION, "tools" : qUnion([Q0]), "targets" : qUnion([Q1]), "keepTools" : true});
        }
        {
            var Q0;
            {var subQ0=sQuery(id+"F7.wireOp",EDGE,"E29");Q0=makeQuery(id+"F14.opBoolean","COPY",EDGE,{"derivedFrom":makeQuery(id+"F9.boolean.opBoolean","MERGE",EDGE,{"derivedFrom":[makeQuery(id+"F8.opExtrude","CAP_EDGE",EDGE,{"disambiguationData":[OSD([subQ0])],"isStart":false}),makeQuery(id+"F9.opExtrude","CAP_EDGE",EDGE,{"disambiguationData":[OSD([subQ0])],"isStart":true})]})});}
            var Q1;
            {var subQ0=sQuery(id+"F7.wireOp",EDGE,"E29");var subQ1=makeQuery(id+"F2.opSweep","CAP_FACE",FACE,{"disambiguationData":[OSD([sQuery(id+"F0.wireOp",VERTEX,"E3.end"),sQuery(id+"F1.wireOp",EDGE,"E8"),sQuery(id+"F1.wireOp",EDGE,"E9"),sQuery(id+"F1.wireOp",EDGE,"E11.MirrorCS"),sQuery(id+"F1.wireOp",EDGE,"E12.MirrorCS"),sQuery(id+"F1.wireOp",EDGE,"E13"),sQuery(id+"F1.wireOp",EDGE,"E14"),sQuery(id+"F1.wireOp",EDGE,"E15.MirrorCS"),sQuery(id+"F1.wireOp",EDGE,"E16.MirrorCS")])],"isStart":true});Q1=makeQuery(id+"F14.opBoolean","MERGE",EDGE,{"derivedFrom":[makeQuery(id+"F10.opChamfer","BLEND_EDGE",EDGE,{"blendedFrom":[makeQuery(id+"F8.opExtrude","CAP_EDGE",EDGE,{"disambiguationData":[OSD([subQ0])],"isStart":true}),makeQuery(id+"F8.boolean.opBoolean","MERGE",FACE,{"derivedFrom":[subQ1,makeQuery(id+"F3.opPattern","COPY",FACE,{"derivedFrom":subQ1,"instanceName":"-15"}),makeQuery(id+"F3.opPattern","COPY",FACE,{"derivedFrom":subQ1,"instanceName":"-14"}),makeQuery(id+"F3.opPattern","COPY",FACE,{"derivedFrom":subQ1,"instanceName":"-13"}),makeQuery(id+"F3.opPattern","COPY",FACE,{"derivedFrom":subQ1,"instanceName":"-12"}),makeQuery(id+"F3.opPattern","COPY",FACE,{"derivedFrom":subQ1,"instanceName":"-11"}),makeQuery(id+"F3.opPattern","COPY",FACE,{"derivedFrom":subQ1,"instanceName":"-10"}),makeQuery(id+"F3.opPattern","COPY",FACE,{"derivedFrom":subQ1,"instanceName":"-9"}),makeQuery(id+"F3.opPattern","COPY",FACE,{"derivedFrom":subQ1,"instanceName":"-8"}),makeQuery(id+"F3.opPattern","COPY",FACE,{"derivedFrom":subQ1,"instanceName":"-7"}),makeQuery(id+"F3.opPattern","COPY",FACE,{"derivedFrom":subQ1,"instanceName":"-6"}),makeQuery(id+"F3.opPattern","COPY",FACE,{"derivedFrom":subQ1,"instanceName":"-5"}),makeQuery(id+"F3.opPattern","COPY",FACE,{"derivedFrom":subQ1,"instanceName":"-4"}),makeQuery(id+"F3.opPattern","COPY",FACE,{"derivedFrom":subQ1,"instanceName":"-3"}),makeQuery(id+"F3.opPattern","COPY",FACE,{"derivedFrom":subQ1,"instanceName":"-2"}),makeQuery(id+"F3.opPattern","COPY",FACE,{"derivedFrom":subQ1,"instanceName":"-1"}),makeQuery(id+"F8.opExtrude","CAP_FACE",FACE,{"disambiguationData":[OSD([sQuery(id+"F7.wireOp",EDGE,"E19"),sQuery(id+"F7.wireOp",EDGE,"E25"),sQuery(id+"F7.wireOp",EDGE,"E26"),sQuery(id+"F7.wireOp",EDGE,"E27"),sQuery(id+"F7.wireOp",EDGE,"E28"),subQ0,sQuery(id+"F7.wireOp",EDGE,"E30.1.0"),sQuery(id+"F7.wireOp",EDGE,"E30.1.1"),sQuery(id+"F7.wireOp",EDGE,"E30.1.2"),sQuery(id+"F7.wireOp",EDGE,"E30.1.3"),sQuery(id+"F7.wireOp",EDGE,"E30.2.0"),sQuery(id+"F7.wireOp",EDGE,"E30.2.1"),sQuery(id+"F7.wireOp",EDGE,"E30.2.2"),sQuery(id+"F7.wireOp",EDGE,"E30.2.3"),sQuery(id+"F7.wireOp",EDGE,"E30.3.0"),sQuery(id+"F7.wireOp",EDGE,"E30.3.1"),sQuery(id+"F7.wireOp",EDGE,"E30.3.2"),sQuery(id+"F7.wireOp",EDGE,"E30.3.3"),sQuery(id+"F7.wireOp",EDGE,"E30.4.0"),sQuery(id+"F7.wireOp",EDGE,"E30.4.1"),sQuery(id+"F7.wireOp",EDGE,"E30.4.2"),sQuery(id+"F7.wireOp",EDGE,"E30.4.3"),sQuery(id+"F7.wireOp",EDGE,"E30.5.0"),sQuery(id+"F7.wireOp",EDGE,"E30.5.1"),sQuery(id+"F7.wireOp",EDGE,"E30.5.2"),sQuery(id+"F7.wireOp",EDGE,"E30.5.3"),sQuery(id+"F7.wireOp",EDGE,"E30.6.0"),sQuery(id+"F7.wireOp",EDGE,"E30.6.1"),sQuery(id+"F7.wireOp",EDGE,"E30.6.2"),sQuery(id+"F7.wireOp",EDGE,"E30.6.3"),sQuery(id+"F7.wireOp",EDGE,"E30.7.0"),sQuery(id+"F7.wireOp",EDGE,"E30.7.1"),sQuery(id+"F7.wireOp",EDGE,"E30.7.2"),sQuery(id+"F7.wireOp",EDGE,"E30.7.3"),sQuery(id+"F7.wireOp",EDGE,"E30.8.0"),sQuery(id+"F7.wireOp",EDGE,"E30.8.1"),sQuery(id+"F7.wireOp",EDGE,"E30.8.2"),sQuery(id+"F7.wireOp",EDGE,"E30.8.3"),sQuery(id+"F7.wireOp",EDGE,"E30.9.0"),sQuery(id+"F7.wireOp",EDGE,"E30.9.1"),sQuery(id+"F7.wireOp",EDGE,"E30.9.2"),sQuery(id+"F7.wireOp",EDGE,"E30.9.3"),sQuery(id+"F7.wireOp",EDGE,"E30.10.0"),sQuery(id+"F7.wireOp",EDGE,"E30.10.1"),sQuery(id+"F7.wireOp",EDGE,"E30.10.2"),sQuery(id+"F7.wireOp",EDGE,"E30.10.3"),sQuery(id+"F7.wireOp",EDGE,"E30.11.0"),sQuery(id+"F7.wireOp",EDGE,"E30.11.1"),sQuery(id+"F7.wireOp",EDGE,"E30.11.2"),sQuery(id+"F7.wireOp",EDGE,"E30.11.3"),sQuery(id+"F7.wireOp",EDGE,"E30.12.0"),sQuery(id+"F7.wireOp",EDGE,"E30.12.1"),sQuery(id+"F7.wireOp",EDGE,"E30.12.2"),sQuery(id+"F7.wireOp",EDGE,"E30.12.3"),sQuery(id+"F7.wireOp",EDGE,"E30.13.0"),sQuery(id+"F7.wireOp",EDGE,"E30.13.1"),sQuery(id+"F7.wireOp",EDGE,"E30.13.2"),sQuery(id+"F7.wireOp",EDGE,"E30.13.3"),sQuery(id+"F7.wireOp",EDGE,"E30.14.0"),sQuery(id+"F7.wireOp",EDGE,"E30.14.1"),sQuery(id+"F7.wireOp",EDGE,"E30.14.2"),sQuery(id+"F7.wireOp",EDGE,"E30.14.3"),sQuery(id+"F7.wireOp",EDGE,"E30.15.0"),sQuery(id+"F7.wireOp",EDGE,"E30.15.1"),sQuery(id+"F7.wireOp",EDGE,"E30.15.2"),sQuery(id+"F7.wireOp",EDGE,"E30.15.3"),sQuery(id+"F7.wireOp",EDGE,"E31.trimOffspring"),sQuery(id+"F7.wireOp",EDGE,"E32.trimOffspring"),sQuery(id+"F7.wireOp",EDGE,"E33.trimOffspring"),sQuery(id+"F7.wireOp",EDGE,"E34.trimOffspring"),sQuery(id+"F7.wireOp",EDGE,"E35.trimOffspring"),sQuery(id+"F7.wireOp",EDGE,"E36.trimOffspring"),sQuery(id+"F7.wireOp",EDGE,"E37.trimOffspring"),sQuery(id+"F7.wireOp",EDGE,"E38.trimOffspring"),sQuery(id+"F7.wireOp",EDGE,"E39.trimOffspring"),sQuery(id+"F7.wireOp",EDGE,"E40.trimOffspring"),sQuery(id+"F7.wireOp",EDGE,"E41.trimOffspring"),sQuery(id+"F7.wireOp",EDGE,"E42.trimOffspring"),sQuery(id+"F7.wireOp",EDGE,"E43.trimOffspring"),sQuery(id+"F7.wireOp",EDGE,"E44.trimOffspring"),sQuery(id+"F7.wireOp",EDGE,"E45.trimOffspring")])],"isStart":true})]})],"blendedInto":[makeQuery(id+"F8.boolean.opBoolean","MERGE",FACE,{"derivedFrom":[subQ1,makeQuery(id+"F3.opPattern","COPY",FACE,{"derivedFrom":subQ1,"instanceName":"-15"}),makeQuery(id+"F3.opPattern","COPY",FACE,{"derivedFrom":subQ1,"instanceName":"-14"}),makeQuery(id+"F3.opPattern","COPY",FACE,{"derivedFrom":subQ1,"instanceName":"-13"}),makeQuery(id+"F3.opPattern","COPY",FACE,{"derivedFrom":subQ1,"instanceName":"-12"}),makeQuery(id+"F3.opPattern","COPY",FACE,{"derivedFrom":subQ1,"instanceName":"-11"}),makeQuery(id+"F3.opPattern","COPY",FACE,{"derivedFrom":subQ1,"instanceName":"-10"}),makeQuery(id+"F3.opPattern","COPY",FACE,{"derivedFrom":subQ1,"instanceName":"-9"}),makeQuery(id+"F3.opPattern","COPY",FACE,{"derivedFrom":subQ1,"instanceName":"-8"}),makeQuery(id+"F3.opPattern","COPY",FACE,{"derivedFrom":subQ1,"instanceName":"-7"}),makeQuery(id+"F3.opPattern","COPY",FACE,{"derivedFrom":subQ1,"instanceName":"-6"}),makeQuery(id+"F3.opPattern","COPY",FACE,{"derivedFrom":subQ1,"instanceName":"-5"}),makeQuery(id+"F3.opPattern","COPY",FACE,{"derivedFrom":subQ1,"instanceName":"-4"}),makeQuery(id+"F3.opPattern","COPY",FACE,{"derivedFrom":subQ1,"instanceName":"-3"}),makeQuery(id+"F3.opPattern","COPY",FACE,{"derivedFrom":subQ1,"instanceName":"-2"}),makeQuery(id+"F3.opPattern","COPY",FACE,{"derivedFrom":subQ1,"instanceName":"-1"}),makeQuery(id+"F8.opExtrude","CAP_FACE",FACE,{"disambiguationData":[OSD([sQuery(id+"F7.wireOp",EDGE,"E19"),sQuery(id+"F7.wireOp",EDGE,"E25"),sQuery(id+"F7.wireOp",EDGE,"E26"),sQuery(id+"F7.wireOp",EDGE,"E27"),sQuery(id+"F7.wireOp",EDGE,"E28"),subQ0,sQuery(id+"F7.wireOp",EDGE,"E30.1.0"),sQuery(id+"F7.wireOp",EDGE,"E30.1.1"),sQuery(id+"F7.wireOp",EDGE,"E30.1.2"),sQuery(id+"F7.wireOp",EDGE,"E30.1.3"),sQuery(id+"F7.wireOp",EDGE,"E30.2.0"),sQuery(id+"F7.wireOp",EDGE,"E30.2.1"),sQuery(id+"F7.wireOp",EDGE,"E30.2.2"),sQuery(id+"F7.wireOp",EDGE,"E30.2.3"),sQuery(id+"F7.wireOp",EDGE,"E30.3.0"),sQuery(id+"F7.wireOp",EDGE,"E30.3.1"),sQuery(id+"F7.wireOp",EDGE,"E30.3.2"),sQuery(id+"F7.wireOp",EDGE,"E30.3.3"),sQuery(id+"F7.wireOp",EDGE,"E30.4.0"),sQuery(id+"F7.wireOp",EDGE,"E30.4.1"),sQuery(id+"F7.wireOp",EDGE,"E30.4.2"),sQuery(id+"F7.wireOp",EDGE,"E30.4.3"),sQuery(id+"F7.wireOp",EDGE,"E30.5.0"),sQuery(id+"F7.wireOp",EDGE,"E30.5.1"),sQuery(id+"F7.wireOp",EDGE,"E30.5.2"),sQuery(id+"F7.wireOp",EDGE,"E30.5.3"),sQuery(id+"F7.wireOp",EDGE,"E30.6.0"),sQuery(id+"F7.wireOp",EDGE,"E30.6.1"),sQuery(id+"F7.wireOp",EDGE,"E30.6.2"),sQuery(id+"F7.wireOp",EDGE,"E30.6.3"),sQuery(id+"F7.wireOp",EDGE,"E30.7.0"),sQuery(id+"F7.wireOp",EDGE,"E30.7.1"),sQuery(id+"F7.wireOp",EDGE,"E30.7.2"),sQuery(id+"F7.wireOp",EDGE,"E30.7.3"),sQuery(id+"F7.wireOp",EDGE,"E30.8.0"),sQuery(id+"F7.wireOp",EDGE,"E30.8.1"),sQuery(id+"F7.wireOp",EDGE,"E30.8.2"),sQuery(id+"F7.wireOp",EDGE,"E30.8.3"),sQuery(id+"F7.wireOp",EDGE,"E30.9.0"),sQuery(id+"F7.wireOp",EDGE,"E30.9.1"),sQuery(id+"F7.wireOp",EDGE,"E30.9.2"),sQuery(id+"F7.wireOp",EDGE,"E30.9.3"),sQuery(id+"F7.wireOp",EDGE,"E30.10.0"),sQuery(id+"F7.wireOp",EDGE,"E30.10.1"),sQuery(id+"F7.wireOp",EDGE,"E30.10.2"),sQuery(id+"F7.wireOp",EDGE,"E30.10.3"),sQuery(id+"F7.wireOp",EDGE,"E30.11.0"),sQuery(id+"F7.wireOp",EDGE,"E30.11.1"),sQuery(id+"F7.wireOp",EDGE,"E30.11.2"),sQuery(id+"F7.wireOp",EDGE,"E30.11.3"),sQuery(id+"F7.wireOp",EDGE,"E30.12.0"),sQuery(id+"F7.wireOp",EDGE,"E30.12.1"),sQuery(id+"F7.wireOp",EDGE,"E30.12.2"),sQuery(id+"F7.wireOp",EDGE,"E30.12.3"),sQuery(id+"F7.wireOp",EDGE,"E30.13.0"),sQuery(id+"F7.wireOp",EDGE,"E30.13.1"),sQuery(id+"F7.wireOp",EDGE,"E30.13.2"),sQuery(id+"F7.wireOp",EDGE,"E30.13.3"),sQuery(id+"F7.wireOp",EDGE,"E30.14.0"),sQuery(id+"F7.wireOp",EDGE,"E30.14.1"),sQuery(id+"F7.wireOp",EDGE,"E30.14.2"),sQuery(id+"F7.wireOp",EDGE,"E30.14.3"),sQuery(id+"F7.wireOp",EDGE,"E30.15.0"),sQuery(id+"F7.wireOp",EDGE,"E30.15.1"),sQuery(id+"F7.wireOp",EDGE,"E30.15.2"),sQuery(id+"F7.wireOp",EDGE,"E30.15.3"),sQuery(id+"F7.wireOp",EDGE,"E31.trimOffspring"),sQuery(id+"F7.wireOp",EDGE,"E32.trimOffspring"),sQuery(id+"F7.wireOp",EDGE,"E33.trimOffspring"),sQuery(id+"F7.wireOp",EDGE,"E34.trimOffspring"),sQuery(id+"F7.wireOp",EDGE,"E35.trimOffspring"),sQuery(id+"F7.wireOp",EDGE,"E36.trimOffspring"),sQuery(id+"F7.wireOp",EDGE,"E37.trimOffspring"),sQuery(id+"F7.wireOp",EDGE,"E38.trimOffspring"),sQuery(id+"F7.wireOp",EDGE,"E39.trimOffspring"),sQuery(id+"F7.wireOp",EDGE,"E40.trimOffspring"),sQuery(id+"F7.wireOp",EDGE,"E41.trimOffspring"),sQuery(id+"F7.wireOp",EDGE,"E42.trimOffspring"),sQuery(id+"F7.wireOp",EDGE,"E43.trimOffspring"),sQuery(id+"F7.wireOp",EDGE,"E44.trimOffspring"),sQuery(id+"F7.wireOp",EDGE,"E45.trimOffspring")])],"isStart":true})]})]}),makeQuery(id+"F13.opExtrude","CAP_EDGE",EDGE,{"disambiguationData":[OSD([sQuery(id+"F12.wireOp",EDGE,"E46.0")])],"isStart":true})]});}
            chamfer(context, id + "F15", {"entities" : qUnion([Q0, Q1]), "width" : 0.2 * mm, "tangentPropagation" : true});
        }
        {
            var Q0;
            Q0=qCreatedBy(makeId("Top.planeOp"),FACE);
            var sketch = newSketch(context, id + "F16", { "sketchPlane" : qUnion([Q0])});
            skLineSegment(sketch, "E47", {"start": v(0.53, 40.17) * mm, "end": v(1.64, 40.21) * mm});
            skLineSegment(sketch, "E48", {"start": v(1.64, 40.21) * mm, "end": v(4.95, 40.26) * mm});
            skLineSegment(sketch, "E49", {"start": v(4.95, 40.26) * mm, "end": v(8.94, 40.01) * mm});
            skLineSegment(sketch, "E50", {"start": v(8.94, 40.01) * mm, "end": v(12.53, 39.18) * mm});
            skLineSegment(sketch, "E51", {"start": v(12.53, 39.18) * mm, "end": v(15.03, 38.02) * mm});
            skLineSegment(sketch, "E52", {"start": v(15.03, 38.02) * mm, "end": v(15.76, 37.5) * mm});
            skLineSegment(sketch, "E53", {"start": v(15.76, 37.5) * mm, "end": v(16.17, 37.2) * mm});
            skLineSegment(sketch, "E54", {"start": v(16.17, 37.2) * mm, "end": v(17.3, 36.13) * mm});
            skLineSegment(sketch, "E55", {"start": v(17.3, 36.13) * mm, "end": v(18.64, 34.46) * mm});
            skLineSegment(sketch, "E56", {"start": v(18.64, 34.46) * mm, "end": v(19.73, 32.53) * mm});
            skLineSegment(sketch, "E57", {"start": v(19.73, 32.53) * mm, "end": v(20.57, 30.4) * mm});
            skLineSegment(sketch, "E58", {"start": v(20.57, 30.4) * mm, "end": v(21.16, 28.13) * mm});
            skLineSegment(sketch, "E59", {"start": v(21.16, 28.13) * mm, "end": v(21.46, 25.77) * mm});
            skLineSegment(sketch, "E60", {"start": v(21.46, 25.77) * mm, "end": v(21.48, 23.37) * mm});
            skLineSegment(sketch, "E61", {"start": v(21.48, 23.37) * mm, "end": v(21.19, 20.99) * mm});
            skLineSegment(sketch, "E62", {"start": v(21.19, 20.99) * mm, "end": v(20.58, 18.68) * mm});
            skLineSegment(sketch, "E63", {"start": v(20.58, 18.68) * mm, "end": v(19.65, 16.5) * mm});
            skLineSegment(sketch, "E64", {"start": v(19.65, 16.5) * mm, "end": v(18.37, 14.52) * mm});
            skLineSegment(sketch, "E65", {"start": v(18.37, 14.52) * mm, "end": v(16.73, 12.76) * mm});
            skLineSegment(sketch, "E66", {"start": v(16.73, 12.76) * mm, "end": v(14.72, 11.3) * mm});
            skLineSegment(sketch, "E67", {"start": v(14.72, 11.3) * mm, "end": v(12.32, 10.19) * mm});
            skLineSegment(sketch, "E68", {"start": v(12.32, 10.19) * mm, "end": v(9.53, 9.48) * mm});
            skLineSegment(sketch, "E69", {"start": v(9.53, 9.48) * mm, "end": v(7.12, 9.23) * mm});
            skLineSegment(sketch, "E70", {"start": v(7.12, 9.23) * mm, "end": v(6.32, 9.23) * mm});
            skLineSegment(sketch, "E71", {"start": v(6.32, 9.23) * mm, "end": v(0.54, 9.26) * mm});
            skLineSegment(sketch, "E72", {"start": v(0.54, 9.26) * mm, "end": v(0.53, 40.17) * mm});
            skLineSegment(sketch, "E73", {"start": v(-12.42, -0.15) * mm, "end": v(-11.36, -0.26) * mm});
            skLineSegment(sketch, "E74", {"start": v(-11.36, -0.26) * mm, "end": v(-8.16, -0.39) * mm});
            skLineSegment(sketch, "E75", {"start": v(-8.16, -0.39) * mm, "end": v(-3.47, -0.4) * mm});
            skLineSegment(sketch, "E76", {"start": v(-3.47, -0.4) * mm, "end": v(1.25, -0.31) * mm});
            skLineSegment(sketch, "E77", {"start": v(1.25, -0.31) * mm, "end": v(4.53, -0.25) * mm});
            skLineSegment(sketch, "E78", {"start": v(4.53, -0.25) * mm, "end": v(5.62, -0.25) * mm});
            skLineSegment(sketch, "E79", {"start": v(5.62, -0.25) * mm, "end": v(6.66, -0.25) * mm});
            skLineSegment(sketch, "E80", {"start": v(6.66, -0.25) * mm, "end": v(9.8, -0.12) * mm});
            skLineSegment(sketch, "E81", {"start": v(9.8, -0.12) * mm, "end": v(13.84, 0.3) * mm});
            skLineSegment(sketch, "E82", {"start": v(13.84, 0.3) * mm, "end": v(17.64, 1.11) * mm});
            skLineSegment(sketch, "E83", {"start": v(17.64, 1.11) * mm, "end": v(20.26, 1.98) * mm});
            skLineSegment(sketch, "E84", {"start": v(20.26, 1.98) * mm, "end": v(21.09, 2.35) * mm});
            skLineSegment(sketch, "E85", {"start": v(21.09, 2.35) * mm, "end": v(21.92, 2.73) * mm});
            skLineSegment(sketch, "E86", {"start": v(21.92, 2.73) * mm, "end": v(24.28, 4.13) * mm});
            skLineSegment(sketch, "E87", {"start": v(24.28, 4.13) * mm, "end": v(27.05, 6.32) * mm});
            skLineSegment(sketch, "E88", {"start": v(27.05, 6.32) * mm, "end": v(29.4, 8.85) * mm});
            skLineSegment(sketch, "E89", {"start": v(29.4, 8.85) * mm, "end": v(31.34, 11.67) * mm});
            skLineSegment(sketch, "E90", {"start": v(31.34, 11.67) * mm, "end": v(32.86, 14.72) * mm});
            skLineSegment(sketch, "E91", {"start": v(32.86, 14.72) * mm, "end": v(33.95, 17.95) * mm});
            skLineSegment(sketch, "E92", {"start": v(33.95, 17.95) * mm, "end": v(34.62, 21.3) * mm});
            skLineSegment(sketch, "E93", {"start": v(34.62, 21.3) * mm, "end": v(34.87, 24.7) * mm});
            skLineSegment(sketch, "E94", {"start": v(34.87, 24.7) * mm, "end": v(34.68, 28.1) * mm});
            skLineSegment(sketch, "E95", {"start": v(34.68, 28.1) * mm, "end": v(34.07, 31.43) * mm});
            skLineSegment(sketch, "E96", {"start": v(34.07, 31.43) * mm, "end": v(33.04, 34.65) * mm});
            skLineSegment(sketch, "E97", {"start": v(33.04, 34.65) * mm, "end": v(31.56, 37.7) * mm});
            skLineSegment(sketch, "E98", {"start": v(31.56, 37.7) * mm, "end": v(29.66, 40.51) * mm});
            skLineSegment(sketch, "E99", {"start": v(29.66, 40.51) * mm, "end": v(27.32, 43.04) * mm});
            skLineSegment(sketch, "E100", {"start": v(27.32, 43.04) * mm, "end": v(24.55, 45.2) * mm});
            skLineSegment(sketch, "E101", {"start": v(24.55, 45.2) * mm, "end": v(22.17, 46.6) * mm});
            skLineSegment(sketch, "E102", {"start": v(22.17, 46.6) * mm, "end": v(21.34, 46.97) * mm});
            skLineSegment(sketch, "E103", {"start": v(21.34, 46.97) * mm, "end": v(20.5, 47.35) * mm});
            skLineSegment(sketch, "E104", {"start": v(20.5, 47.35) * mm, "end": v(17.83, 48.25) * mm});
            skLineSegment(sketch, "E105", {"start": v(17.83, 48.25) * mm, "end": v(14.14, 49.06) * mm});
            skLineSegment(sketch, "E106", {"start": v(14.14, 49.06) * mm, "end": v(10.2, 49.48) * mm});
            skLineSegment(sketch, "E107", {"start": v(10.2, 49.48) * mm, "end": v(7.03, 49.6) * mm});
            skLineSegment(sketch, "E108", {"start": v(7.03, 49.6) * mm, "end": v(5.97, 49.6) * mm});
            skLineSegment(sketch, "E109", {"start": v(5.97, 49.6) * mm, "end": v(4.86, 49.6) * mm});
            skLineSegment(sketch, "E110", {"start": v(4.86, 49.6) * mm, "end": v(1.51, 49.65) * mm});
            skLineSegment(sketch, "E111", {"start": v(1.51, 49.65) * mm, "end": v(-3.26, 49.74) * mm});
            skLineSegment(sketch, "E112", {"start": v(-3.26, 49.74) * mm, "end": v(-7.98, 49.73) * mm});
            skLineSegment(sketch, "E113", {"start": v(-7.98, 49.73) * mm, "end": v(-11.24, 49.6) * mm});
            skLineSegment(sketch, "E114", {"start": v(-11.24, 49.6) * mm, "end": v(-12.31, 49.5) * mm});
            skLineSegment(sketch, "E115", {"start": v(-12.31, 49.5) * mm, "end": v(-12.42, -0.15) * mm});
            skLineSegment(sketch, "E116", {"start": v(-54.75, 47.54) * mm, "end": v(-54.8, 36.83) * mm});
            skLineSegment(sketch, "E117", {"start": v(-54.8, 36.83) * mm, "end": v(-54.28, 36.8) * mm});
            skLineSegment(sketch, "E118", {"start": v(-54.28, 36.8) * mm, "end": v(-52.7, 37.23) * mm});
            skLineSegment(sketch, "E119", {"start": v(-52.7, 37.23) * mm, "end": v(-50.1, 38.25) * mm});
            skLineSegment(sketch, "E120", {"start": v(-50.1, 38.25) * mm, "end": v(-47.4, 39.39) * mm});
            skLineSegment(sketch, "E121", {"start": v(-47.4, 39.39) * mm, "end": v(-45.68, 40.04) * mm});
            skLineSegment(sketch, "E122", {"start": v(-45.68, 40.04) * mm, "end": v(-45.08, 40.17) * mm});
            skLineSegment(sketch, "E123", {"start": v(-45.08, 40.17) * mm, "end": v(-43.83, 40.46) * mm});
            skLineSegment(sketch, "E124", {"start": v(-43.83, 40.46) * mm, "end": v(-40, 40.91) * mm});
            skLineSegment(sketch, "E125", {"start": v(-40, 40.91) * mm, "end": v(-36.11, 40.7) * mm});
            skLineSegment(sketch, "E126", {"start": v(-36.11, 40.7) * mm, "end": v(-33.33, 39.74) * mm});
            skLineSegment(sketch, "E127", {"start": v(-33.33, 39.74) * mm, "end": v(-31.57, 38.28) * mm});
            skLineSegment(sketch, "E128", {"start": v(-31.57, 38.28) * mm, "end": v(-30.73, 36.52) * mm});
            skLineSegment(sketch, "E129", {"start": v(-30.73, 36.52) * mm, "end": v(-30.74, 34.69) * mm});
            skLineSegment(sketch, "E130", {"start": v(-30.74, 34.69) * mm, "end": v(-31.5, 33) * mm});
            skLineSegment(sketch, "E131", {"start": v(-31.5, 33) * mm, "end": v(-32.52, 31.93) * mm});
            skLineSegment(sketch, "E132", {"start": v(-32.52, 31.93) * mm, "end": v(-32.93, 31.68) * mm});
            skLineSegment(sketch, "E133", {"start": v(-32.93, 31.68) * mm, "end": v(-33.2, 31.5) * mm});
            skLineSegment(sketch, "E134", {"start": v(-33.2, 31.5) * mm, "end": v(-34.16, 31.16) * mm});
            skLineSegment(sketch, "E135", {"start": v(-34.16, 31.16) * mm, "end": v(-35.69, 30.85) * mm});
            skLineSegment(sketch, "E136", {"start": v(-35.69, 30.85) * mm, "end": v(-37.39, 30.68) * mm});
            skLineSegment(sketch, "E137", {"start": v(-37.39, 30.68) * mm, "end": v(-39.14, 30.6) * mm});
            skLineSegment(sketch, "E138", {"start": v(-39.14, 30.6) * mm, "end": v(-40.84, 30.56) * mm});
            skLineSegment(sketch, "E139", {"start": v(-40.84, 30.56) * mm, "end": v(-42.35, 30.49) * mm});
            skLineSegment(sketch, "E140", {"start": v(-42.35, 30.49) * mm, "end": v(-43.55, 30.34) * mm});
            skLineSegment(sketch, "E141", {"start": v(-43.55, 30.34) * mm, "end": v(-44.17, 30.16) * mm});
            skLineSegment(sketch, "E142", {"start": v(-44.17, 30.16) * mm, "end": v(-44.34, 30.04) * mm});
            skLineSegment(sketch, "E143", {"start": v(-44.34, 30.04) * mm, "end": v(-44.4, 29.95) * mm});
            skLineSegment(sketch, "E144", {"start": v(-44.4, 29.95) * mm, "end": v(-44.6, 29.67) * mm});
            skLineSegment(sketch, "E145", {"start": v(-44.6, 29.67) * mm, "end": v(-44.7, 29.45) * mm});
            skLineSegment(sketch, "E146", {"start": v(-44.7, 29.45) * mm, "end": v(-44.7, 29.12) * mm});
            skLineSegment(sketch, "E147", {"start": v(-44.7, 29.12) * mm, "end": v(-44.69, 28.6) * mm});
            skLineSegment(sketch, "E148", {"start": v(-44.69, 28.6) * mm, "end": v(-44.7, 28.42) * mm});
            skLineSegment(sketch, "E149", {"start": v(-44.7, 28.42) * mm, "end": v(-44.61, 21.53) * mm});
            skLineSegment(sketch, "E150", {"start": v(-44.61, 21.53) * mm, "end": v(-43.84, 21.36) * mm});
            skLineSegment(sketch, "E151", {"start": v(-43.84, 21.36) * mm, "end": v(-41.44, 21.25) * mm});
            skLineSegment(sketch, "E152", {"start": v(-41.44, 21.25) * mm, "end": v(-38.17, 21.3) * mm});
            skLineSegment(sketch, "E153", {"start": v(-38.17, 21.3) * mm, "end": v(-34.99, 21.09) * mm});
            skLineSegment(sketch, "E154", {"start": v(-34.99, 21.09) * mm, "end": v(-32.7, 20.4) * mm});
            skLineSegment(sketch, "E155", {"start": v(-32.7, 20.4) * mm, "end": v(-32.06, 20) * mm});
            skLineSegment(sketch, "E156", {"start": v(-32.06, 20) * mm, "end": v(-31.8, 19.83) * mm});
            skLineSegment(sketch, "E157", {"start": v(-31.8, 19.83) * mm, "end": v(-31.1, 19.21) * mm});
            skLineSegment(sketch, "E158", {"start": v(-31.1, 19.21) * mm, "end": v(-30.4, 18.25) * mm});
            skLineSegment(sketch, "E159", {"start": v(-30.4, 18.25) * mm, "end": v(-29.96, 17.15) * mm});
            skLineSegment(sketch, "E160", {"start": v(-29.96, 17.15) * mm, "end": v(-29.77, 15.97) * mm});
            skLineSegment(sketch, "E161", {"start": v(-29.77, 15.97) * mm, "end": v(-29.86, 14.73) * mm});
            skLineSegment(sketch, "E162", {"start": v(-29.86, 14.73) * mm, "end": v(-30.23, 13.5) * mm});
            skLineSegment(sketch, "E163", {"start": v(-30.23, 13.5) * mm, "end": v(-30.88, 12.3) * mm});
            skLineSegment(sketch, "E164", {"start": v(-30.88, 12.3) * mm, "end": v(-31.81, 11.19) * mm});
            skLineSegment(sketch, "E165", {"start": v(-31.81, 11.19) * mm, "end": v(-33.04, 10.2) * mm});
            skLineSegment(sketch, "E166", {"start": v(-33.04, 10.2) * mm, "end": v(-34.58, 9.4) * mm});
            skLineSegment(sketch, "E167", {"start": v(-34.58, 9.4) * mm, "end": v(-36.42, 8.82) * mm});
            skLineSegment(sketch, "E168", {"start": v(-36.42, 8.82) * mm, "end": v(-38.58, 8.5) * mm});
            skLineSegment(sketch, "E169", {"start": v(-38.58, 8.5) * mm, "end": v(-41.06, 8.49) * mm});
            skLineSegment(sketch, "E170", {"start": v(-41.06, 8.49) * mm, "end": v(-43.87, 8.82) * mm});
            skLineSegment(sketch, "E171", {"start": v(-43.87, 8.82) * mm, "end": v(-47, 9.56) * mm});
            skLineSegment(sketch, "E172", {"start": v(-47, 9.56) * mm, "end": v(-49.63, 10.4) * mm});
            skLineSegment(sketch, "E173", {"start": v(-49.63, 10.4) * mm, "end": v(-50.5, 10.73) * mm});
            skLineSegment(sketch, "E174", {"start": v(-50.5, 10.73) * mm, "end": v(-50.83, 10.87) * mm});
            skLineSegment(sketch, "E175", {"start": v(-50.83, 10.87) * mm, "end": v(-51.83, 11.35) * mm});
            skLineSegment(sketch, "E176", {"start": v(-51.83, 11.35) * mm, "end": v(-53.16, 12) * mm});
            skLineSegment(sketch, "E177", {"start": v(-53.16, 12) * mm, "end": v(-54.59, 12.5) * mm});
            skLineSegment(sketch, "E178", {"start": v(-54.59, 12.5) * mm, "end": v(-55.8, 12.7) * mm});
            skLineSegment(sketch, "E179", {"start": v(-55.8, 12.7) * mm, "end": v(-56.2, 12.68) * mm});
            skLineSegment(sketch, "E180", {"start": v(-56.2, 12.68) * mm, "end": v(-56.23, 1.8) * mm});
            skLineSegment(sketch, "E181", {"start": v(-56.23, 1.8) * mm, "end": v(-55.28, 1.43) * mm});
            skLineSegment(sketch, "E182", {"start": v(-55.28, 1.43) * mm, "end": v(-52.36, 0.52) * mm});
            skLineSegment(sketch, "E183", {"start": v(-52.36, 0.52) * mm, "end": v(-48.14, -0.46) * mm});
            skLineSegment(sketch, "E184", {"start": v(-48.14, -0.46) * mm, "end": v(-43.72, -1.11) * mm});
            skLineSegment(sketch, "E185", {"start": v(-43.72, -1.11) * mm, "end": v(-39.23, -1.38) * mm});
            skLineSegment(sketch, "E186", {"start": v(-39.23, -1.38) * mm, "end": v(-34.8, -1.2) * mm});
            skLineSegment(sketch, "E187", {"start": v(-34.8, -1.2) * mm, "end": v(-30.56, -0.53) * mm});
            skLineSegment(sketch, "E188", {"start": v(-30.56, -0.53) * mm, "end": v(-26.64, 0.69) * mm});
            skLineSegment(sketch, "E189", {"start": v(-26.64, 0.69) * mm, "end": v(-24, 1.96) * mm});
            skLineSegment(sketch, "E190", {"start": v(-24, 1.96) * mm, "end": v(-23.2, 2.5) * mm});
            skLineSegment(sketch, "E191", {"start": v(-23.2, 2.5) * mm, "end": v(-22.45, 3) * mm});
            skLineSegment(sketch, "E192", {"start": v(-22.45, 3) * mm, "end": v(-20.45, 4.85) * mm});
            skLineSegment(sketch, "E193", {"start": v(-20.45, 4.85) * mm, "end": v(-18.38, 7.85) * mm});
            skLineSegment(sketch, "E194", {"start": v(-18.38, 7.85) * mm, "end": v(-17.14, 11.57) * mm});
            skLineSegment(sketch, "E195", {"start": v(-17.14, 11.57) * mm, "end": v(-16.8, 14.95) * mm});
            skLineSegment(sketch, "E196", {"start": v(-16.8, 14.95) * mm, "end": v(-16.86, 16.06) * mm});
            skLineSegment(sketch, "E197", {"start": v(-16.86, 16.06) * mm, "end": v(-16.89, 16.62) * mm});
            skLineSegment(sketch, "E198", {"start": v(-16.89, 16.62) * mm, "end": v(-17.17, 18.27) * mm});
            skLineSegment(sketch, "E199", {"start": v(-17.17, 18.27) * mm, "end": v(-17.84, 20.13) * mm});
            skLineSegment(sketch, "E200", {"start": v(-17.84, 20.13) * mm, "end": v(-18.8, 21.66) * mm});
            skLineSegment(sketch, "E201", {"start": v(-18.8, 21.66) * mm, "end": v(-20.06, 22.93) * mm});
            skLineSegment(sketch, "E202", {"start": v(-20.06, 22.93) * mm, "end": v(-21.53, 23.96) * mm});
            skLineSegment(sketch, "E203", {"start": v(-21.53, 23.96) * mm, "end": v(-23.2, 24.82) * mm});
            skLineSegment(sketch, "E204", {"start": v(-23.2, 24.82) * mm, "end": v(-25.01, 25.54) * mm});
            skLineSegment(sketch, "E205", {"start": v(-25.01, 25.54) * mm, "end": v(-26.45, 26.02) * mm});
            skLineSegment(sketch, "E206", {"start": v(-26.45, 26.02) * mm, "end": v(-26.93, 26.16) * mm});
            skLineSegment(sketch, "E207", {"start": v(-26.93, 26.16) * mm, "end": v(-26.8, 26.32) * mm});
            skLineSegment(sketch, "E208", {"start": v(-26.8, 26.32) * mm, "end": v(-26.27, 26.7) * mm});
            skLineSegment(sketch, "E209", {"start": v(-26.27, 26.7) * mm, "end": v(-25.29, 27.23) * mm});
            skLineSegment(sketch, "E210", {"start": v(-25.29, 27.23) * mm, "end": v(-24.08, 27.87) * mm});
            skLineSegment(sketch, "E211", {"start": v(-24.08, 27.87) * mm, "end": v(-22.75, 28.7) * mm});
            skLineSegment(sketch, "E212", {"start": v(-22.75, 28.7) * mm, "end": v(-21.4, 29.8) * mm});
            skLineSegment(sketch, "E213", {"start": v(-21.4, 29.8) * mm, "end": v(-20.15, 31.27) * mm});
            skLineSegment(sketch, "E214", {"start": v(-20.15, 31.27) * mm, "end": v(-19.08, 33.21) * mm});
            skLineSegment(sketch, "E215", {"start": v(-19.08, 33.21) * mm, "end": v(-18.44, 35.07) * mm});
            skLineSegment(sketch, "E216", {"start": v(-18.44, 35.07) * mm, "end": v(-18.3, 35.7) * mm});
            skLineSegment(sketch, "E217", {"start": v(-18.3, 35.7) * mm, "end": v(-18.15, 36.4) * mm});
            skLineSegment(sketch, "E218", {"start": v(-18.15, 36.4) * mm, "end": v(-17.97, 38.6) * mm});
            skLineSegment(sketch, "E219", {"start": v(-17.97, 38.6) * mm, "end": v(-18.24, 41.14) * mm});
            skLineSegment(sketch, "E220", {"start": v(-18.24, 41.14) * mm, "end": v(-19.07, 43.36) * mm});
            skLineSegment(sketch, "E221", {"start": v(-19.07, 43.36) * mm, "end": v(-20.4, 45.25) * mm});
            skLineSegment(sketch, "E222", {"start": v(-20.4, 45.25) * mm, "end": v(-22.17, 46.84) * mm});
            skLineSegment(sketch, "E223", {"start": v(-22.17, 46.84) * mm, "end": v(-24.32, 48.13) * mm});
            skLineSegment(sketch, "E224", {"start": v(-24.32, 48.13) * mm, "end": v(-26.8, 49.13) * mm});
            skLineSegment(sketch, "E225", {"start": v(-26.8, 49.13) * mm, "end": v(-29.56, 49.87) * mm});
            skLineSegment(sketch, "E226", {"start": v(-29.56, 49.87) * mm, "end": v(-32.53, 50.35) * mm});
            skLineSegment(sketch, "E227", {"start": v(-32.53, 50.35) * mm, "end": v(-35.67, 50.58) * mm});
            skLineSegment(sketch, "E228", {"start": v(-35.67, 50.58) * mm, "end": v(-38.9, 50.58) * mm});
            skLineSegment(sketch, "E229", {"start": v(-38.9, 50.58) * mm, "end": v(-42.2, 50.36) * mm});
            skLineSegment(sketch, "E230", {"start": v(-42.2, 50.36) * mm, "end": v(-45.49, 49.94) * mm});
            skLineSegment(sketch, "E231", {"start": v(-45.49, 49.94) * mm, "end": v(-48.71, 49.32) * mm});
            skLineSegment(sketch, "E232", {"start": v(-48.71, 49.32) * mm, "end": v(-51.82, 48.51) * mm});
            skLineSegment(sketch, "E233", {"start": v(-51.82, 48.51) * mm, "end": v(-54.03, 47.8) * mm});
            skLineSegment(sketch, "E234", {"start": v(-54.03, 47.8) * mm, "end": v(-54.75, 47.54) * mm});
            skLineSegment(sketch, "E235", {"start": v(46.54, 39.43) * mm, "end": v(45.03, 39.54) * mm});
            skLineSegment(sketch, "E236", {"start": v(45.03, 39.54) * mm, "end": v(44.9, 41.1) * mm});
            skLineSegment(sketch, "E237", {"start": v(44.9, 41.1) * mm, "end": v(44.93, 43.92) * mm});
            skLineSegment(sketch, "E238", {"start": v(44.93, 43.92) * mm, "end": v(44.99, 45.46) * mm});
            skLineSegment(sketch, "E239", {"start": v(44.99, 45.46) * mm, "end": v(46.54, 45.67) * mm});
            skLineSegment(sketch, "E240", {"start": v(46.54, 45.67) * mm, "end": v(47.01, 45.71) * mm});
            skLineSegment(sketch, "E241", {"start": v(47.01, 45.71) * mm, "end": v(48.47, 45.55) * mm});
            skLineSegment(sketch, "E242", {"start": v(48.47, 45.55) * mm, "end": v(49.85, 44.87) * mm});
            skLineSegment(sketch, "E243", {"start": v(49.85, 44.87) * mm, "end": v(50.67, 43.82) * mm});
            skLineSegment(sketch, "E244", {"start": v(50.67, 43.82) * mm, "end": v(50.94, 42.58) * mm});
            skLineSegment(sketch, "E245", {"start": v(50.94, 42.58) * mm, "end": v(50.66, 41.33) * mm});
            skLineSegment(sketch, "E246", {"start": v(50.66, 41.33) * mm, "end": v(49.83, 40.27) * mm});
            skLineSegment(sketch, "E247", {"start": v(49.83, 40.27) * mm, "end": v(48.46, 39.57) * mm});
            skLineSegment(sketch, "E248", {"start": v(48.46, 39.57) * mm, "end": v(47.01, 39.39) * mm});
            skLineSegment(sketch, "E249", {"start": v(47.01, 39.39) * mm, "end": v(46.54, 39.43) * mm});
            skLineSegment(sketch, "E250", {"start": v(39.73, 28.8) * mm, "end": v(44.98, 28.78) * mm});
            skLineSegment(sketch, "E251", {"start": v(44.98, 28.78) * mm, "end": v(45.07, 35.4) * mm});
            skLineSegment(sketch, "E252", {"start": v(45.07, 35.4) * mm, "end": v(45.7, 35.45) * mm});
            skLineSegment(sketch, "E253", {"start": v(45.7, 35.45) * mm, "end": v(47.57, 35.5) * mm});
            skLineSegment(sketch, "E254", {"start": v(47.57, 35.5) * mm, "end": v(49.74, 35.61) * mm});
            skLineSegment(sketch, "E255", {"start": v(49.74, 35.61) * mm, "end": v(51.73, 36.04) * mm});
            skLineSegment(sketch, "E256", {"start": v(51.73, 36.04) * mm, "end": v(53.22, 36.8) * mm});
            skLineSegment(sketch, "E257", {"start": v(53.22, 36.8) * mm, "end": v(53.65, 37.14) * mm});
            skLineSegment(sketch, "E258", {"start": v(53.65, 37.14) * mm, "end": v(54.03, 37.44) * mm});
            skLineSegment(sketch, "E259", {"start": v(54.03, 37.44) * mm, "end": v(55, 38.55) * mm});
            skLineSegment(sketch, "E260", {"start": v(55, 38.55) * mm, "end": v(55.95, 40.32) * mm});
            skLineSegment(sketch, "E261", {"start": v(55.95, 40.32) * mm, "end": v(56.38, 42.43) * mm});
            skLineSegment(sketch, "E262", {"start": v(56.38, 42.43) * mm, "end": v(56.32, 44.25) * mm});
            skLineSegment(sketch, "E263", {"start": v(56.32, 44.25) * mm, "end": v(56.2, 44.83) * mm});
            skLineSegment(sketch, "E264", {"start": v(56.2, 44.83) * mm, "end": v(56.1, 45.32) * mm});
            skLineSegment(sketch, "E265", {"start": v(56.1, 45.32) * mm, "end": v(55.4, 46.7) * mm});
            skLineSegment(sketch, "E266", {"start": v(55.4, 46.7) * mm, "end": v(54.01, 48.05) * mm});
            skLineSegment(sketch, "E267", {"start": v(54.01, 48.05) * mm, "end": v(52.14, 48.96) * mm});
            skLineSegment(sketch, "E268", {"start": v(52.14, 48.96) * mm, "end": v(49.92, 49.5) * mm});
            skLineSegment(sketch, "E269", {"start": v(49.92, 49.5) * mm, "end": v(47.46, 49.75) * mm});
            skLineSegment(sketch, "E270", {"start": v(47.46, 49.75) * mm, "end": v(44.88, 49.79) * mm});
            skLineSegment(sketch, "E271", {"start": v(44.88, 49.79) * mm, "end": v(42.3, 49.69) * mm});
            skLineSegment(sketch, "E272", {"start": v(42.3, 49.69) * mm, "end": v(40.46, 49.57) * mm});
            skLineSegment(sketch, "E273", {"start": v(40.46, 49.57) * mm, "end": v(39.85, 49.53) * mm});
            skLineSegment(sketch, "E274", {"start": v(39.85, 49.53) * mm, "end": v(39.73, 28.8) * mm});
            skLineSegment(sketch, "E275", {"start": v(39.78, 16.88) * mm, "end": v(42.96, 16.76) * mm});
            skLineSegment(sketch, "E276", {"start": v(42.96, 16.76) * mm, "end": v(43.03, 3.7) * mm});
            skLineSegment(sketch, "E277", {"start": v(43.03, 3.7) * mm, "end": v(42.72, 3.66) * mm});
            skLineSegment(sketch, "E278", {"start": v(42.72, 3.66) * mm, "end": v(41.79, 3.56) * mm});
            skLineSegment(sketch, "E279", {"start": v(41.79, 3.56) * mm, "end": v(40.88, 3.51) * mm});
            skLineSegment(sketch, "E280", {"start": v(40.88, 3.51) * mm, "end": v(40.25, 3.45) * mm});
            skLineSegment(sketch, "E281", {"start": v(40.25, 3.45) * mm, "end": v(39.86, 3.3) * mm});
            skLineSegment(sketch, "E282", {"start": v(39.86, 3.3) * mm, "end": v(39.66, 2.96) * mm});
            skLineSegment(sketch, "E283", {"start": v(39.66, 2.96) * mm, "end": v(39.6, 2.35) * mm});
            skLineSegment(sketch, "E284", {"start": v(39.6, 2.35) * mm, "end": v(39.61, 1.38) * mm});
            skLineSegment(sketch, "E285", {"start": v(39.61, 1.38) * mm, "end": v(39.66, 0.32) * mm});
            skLineSegment(sketch, "E286", {"start": v(39.66, 0.32) * mm, "end": v(39.67, -0.04) * mm});
            skLineSegment(sketch, "E287", {"start": v(39.67, -0.04) * mm, "end": v(40.13, -0.15) * mm});
            skLineSegment(sketch, "E288", {"start": v(40.13, -0.15) * mm, "end": v(41.98, -0.27) * mm});
            skLineSegment(sketch, "E289", {"start": v(41.98, -0.27) * mm, "end": v(45.43, -0.34) * mm});
            skLineSegment(sketch, "E290", {"start": v(45.43, -0.34) * mm, "end": v(48.96, -0.3) * mm});
            skLineSegment(sketch, "E291", {"start": v(48.96, -0.3) * mm, "end": v(50.93, -0.23) * mm});
            skLineSegment(sketch, "E292", {"start": v(50.93, -0.23) * mm, "end": v(51.49, -0.2) * mm});
            skLineSegment(sketch, "E293", {"start": v(51.49, -0.2) * mm, "end": v(51.52, 3.38) * mm});
            skLineSegment(sketch, "E294", {"start": v(51.52, 3.38) * mm, "end": v(48.44, 3.49) * mm});
            skLineSegment(sketch, "E295", {"start": v(48.44, 3.49) * mm, "end": v(48.25, 16.74) * mm});
            skLineSegment(sketch, "E296", {"start": v(48.25, 16.74) * mm, "end": v(51.37, 16.87) * mm});
            skLineSegment(sketch, "E297", {"start": v(51.37, 16.87) * mm, "end": v(51.52, 20.57) * mm});
            skLineSegment(sketch, "E298", {"start": v(51.52, 20.57) * mm, "end": v(39.88, 20.61) * mm});
            skLineSegment(sketch, "E299", {"start": v(39.88, 20.61) * mm, "end": v(39.78, 16.88) * mm});
            skLineSegment(sketch, "E300", {"start": v(-33.76, -46.4) * mm, "end": v(-33.85, -46.56) * mm});
            skLineSegment(sketch, "E301", {"start": v(-33.85, -46.56) * mm, "end": v(-34.23, -47) * mm});
            skLineSegment(sketch, "E302", {"start": v(-34.23, -47) * mm, "end": v(-34.77, -47.35) * mm});
            skLineSegment(sketch, "E303", {"start": v(-34.77, -47.35) * mm, "end": v(-35.36, -47.48) * mm});
            skLineSegment(sketch, "E304", {"start": v(-35.36, -47.48) * mm, "end": v(-35.95, -47.4) * mm});
            skLineSegment(sketch, "E305", {"start": v(-35.95, -47.4) * mm, "end": v(-36.5, -47.12) * mm});
            skLineSegment(sketch, "E306", {"start": v(-36.5, -47.12) * mm, "end": v(-37, -46.67) * mm});
            skLineSegment(sketch, "E307", {"start": v(-37, -46.67) * mm, "end": v(-37.39, -46.06) * mm});
            skLineSegment(sketch, "E308", {"start": v(-37.39, -46.06) * mm, "end": v(-37.6, -45.5) * mm});
            skLineSegment(sketch, "E309", {"start": v(-37.6, -45.5) * mm, "end": v(-37.63, -45.3) * mm});
            skLineSegment(sketch, "E310", {"start": v(-37.63, -45.3) * mm, "end": v(-37.78, -44.6) * mm});
            skLineSegment(sketch, "E311", {"start": v(-37.78, -44.6) * mm, "end": v(-37.99, -42.43) * mm});
            skLineSegment(sketch, "E312", {"start": v(-37.99, -42.43) * mm, "end": v(-37.83, -40.18) * mm});
            skLineSegment(sketch, "E313", {"start": v(-37.83, -40.18) * mm, "end": v(-37.3, -38.57) * mm});
            skLineSegment(sketch, "E314", {"start": v(-37.3, -38.57) * mm, "end": v(-36.5, -37.58) * mm});
            skLineSegment(sketch, "E315", {"start": v(-36.5, -37.58) * mm, "end": v(-35.6, -37.18) * mm});
            skLineSegment(sketch, "E316", {"start": v(-35.6, -37.18) * mm, "end": v(-34.69, -37.38) * mm});
            skLineSegment(sketch, "E317", {"start": v(-34.69, -37.38) * mm, "end": v(-33.92, -38.14) * mm});
            skLineSegment(sketch, "E318", {"start": v(-33.92, -38.14) * mm, "end": v(-33.48, -39.13) * mm});
            skLineSegment(sketch, "E319", {"start": v(-33.48, -39.13) * mm, "end": v(-33.4, -39.47) * mm});
            skLineSegment(sketch, "E320", {"start": v(-33.4, -39.47) * mm, "end": v(-33.33, -39.87) * mm});
            skLineSegment(sketch, "E321", {"start": v(-33.33, -39.87) * mm, "end": v(-33.23, -41.07) * mm});
            skLineSegment(sketch, "E322", {"start": v(-33.23, -41.07) * mm, "end": v(-33.21, -43.1) * mm});
            skLineSegment(sketch, "E323", {"start": v(-33.21, -43.1) * mm, "end": v(-33.38, -45.06) * mm});
            skLineSegment(sketch, "E324", {"start": v(-33.38, -45.06) * mm, "end": v(-33.6, -46.1) * mm});
            skLineSegment(sketch, "E325", {"start": v(-33.6, -46.1) * mm, "end": v(-33.76, -46.4) * mm});
            skLineSegment(sketch, "E326", {"start": v(-42.02, -42.16) * mm, "end": v(-42.02, -43.1) * mm});
            skLineSegment(sketch, "E327", {"start": v(-42.02, -43.1) * mm, "end": v(-41.6, -45.92) * mm});
            skLineSegment(sketch, "E328", {"start": v(-41.6, -45.92) * mm, "end": v(-40.45, -48.45) * mm});
            skLineSegment(sketch, "E329", {"start": v(-40.45, -48.45) * mm, "end": v(-38.81, -49.94) * mm});
            skLineSegment(sketch, "E330", {"start": v(-38.81, -49.94) * mm, "end": v(-36.88, -50.58) * mm});
            skLineSegment(sketch, "E331", {"start": v(-36.88, -50.58) * mm, "end": v(-34.86, -50.56) * mm});
            skLineSegment(sketch, "E332", {"start": v(-34.86, -50.56) * mm, "end": v(-32.98, -50.07) * mm});
            skLineSegment(sketch, "E333", {"start": v(-32.98, -50.07) * mm, "end": v(-31.45, -49.3) * mm});
            skLineSegment(sketch, "E334", {"start": v(-31.45, -49.3) * mm, "end": v(-30.66, -48.68) * mm});
            skLineSegment(sketch, "E335", {"start": v(-30.66, -48.68) * mm, "end": v(-30.47, -48.42) * mm});
            skLineSegment(sketch, "E336", {"start": v(-30.47, -48.42) * mm, "end": v(-30.16, -47.99) * mm});
            skLineSegment(sketch, "E337", {"start": v(-30.16, -47.99) * mm, "end": v(-29.54, -46.46) * mm});
            skLineSegment(sketch, "E338", {"start": v(-29.54, -46.46) * mm, "end": v(-29.06, -44.02) * mm});
            skLineSegment(sketch, "E339", {"start": v(-29.06, -44.02) * mm, "end": v(-28.97, -41.46) * mm});
            skLineSegment(sketch, "E340", {"start": v(-28.97, -41.46) * mm, "end": v(-29.12, -39.7) * mm});
            skLineSegment(sketch, "E341", {"start": v(-29.12, -39.7) * mm, "end": v(-29.23, -39.13) * mm});
            skLineSegment(sketch, "E342", {"start": v(-29.23, -39.13) * mm, "end": v(-29.34, -38.6) * mm});
            skLineSegment(sketch, "E343", {"start": v(-29.34, -38.6) * mm, "end": v(-29.97, -37.07) * mm});
            skLineSegment(sketch, "E344", {"start": v(-29.97, -37.07) * mm, "end": v(-31.28, -35.55) * mm});
            skLineSegment(sketch, "E345", {"start": v(-31.28, -35.55) * mm, "end": v(-33.17, -34.61) * mm});
            skLineSegment(sketch, "E346", {"start": v(-33.17, -34.61) * mm, "end": v(-35.04, -34.3) * mm});
            skLineSegment(sketch, "E347", {"start": v(-35.04, -34.3) * mm, "end": v(-35.66, -34.3) * mm});
            skLineSegment(sketch, "E348", {"start": v(-35.66, -34.3) * mm, "end": v(-36.43, -34.3) * mm});
            skLineSegment(sketch, "E349", {"start": v(-36.43, -34.3) * mm, "end": v(-38.74, -34.85) * mm});
            skLineSegment(sketch, "E350", {"start": v(-38.74, -34.85) * mm, "end": v(-40.7, -36.42) * mm});
            skLineSegment(sketch, "E351", {"start": v(-40.7, -36.42) * mm, "end": v(-41.72, -38.9) * mm});
            skLineSegment(sketch, "E352", {"start": v(-41.72, -38.9) * mm, "end": v(-42.02, -41.35) * mm});
            skLineSegment(sketch, "E353", {"start": v(-42.02, -41.35) * mm, "end": v(-42.02, -42.16) * mm});
            skLineSegment(sketch, "E354", {"start": v(-36.53, -31) * mm, "end": v(-36.26, -31.02) * mm});
            skLineSegment(sketch, "E355", {"start": v(-36.26, -31.02) * mm, "end": v(-35.42, -31) * mm});
            skLineSegment(sketch, "E356", {"start": v(-35.42, -31) * mm, "end": v(-34.65, -30.85) * mm});
            skLineSegment(sketch, "E357", {"start": v(-34.65, -30.85) * mm, "end": v(-34.14, -30.53) * mm});
            skLineSegment(sketch, "E358", {"start": v(-34.14, -30.53) * mm, "end": v(-33.82, -30.04) * mm});
            skLineSegment(sketch, "E359", {"start": v(-33.82, -30.04) * mm, "end": v(-33.63, -29.39) * mm});
            skLineSegment(sketch, "E360", {"start": v(-33.63, -29.39) * mm, "end": v(-33.48, -28.56) * mm});
            skLineSegment(sketch, "E361", {"start": v(-33.48, -28.56) * mm, "end": v(-33.32, -27.57) * mm});
            skLineSegment(sketch, "E362", {"start": v(-33.32, -27.57) * mm, "end": v(-33.13, -26.69) * mm});
            skLineSegment(sketch, "E363", {"start": v(-33.13, -26.69) * mm, "end": v(-33.06, -26.4) * mm});
            skLineSegment(sketch, "E364", {"start": v(-33.06, -26.4) * mm, "end": v(-32.95, -25.98) * mm});
            skLineSegment(sketch, "E365", {"start": v(-32.95, -25.98) * mm, "end": v(-32.67, -24.7) * mm});
            skLineSegment(sketch, "E366", {"start": v(-32.67, -24.7) * mm, "end": v(-32.26, -22.84) * mm});
            skLineSegment(sketch, "E367", {"start": v(-32.26, -22.84) * mm, "end": v(-31.76, -21.02) * mm});
            skLineSegment(sketch, "E368", {"start": v(-31.76, -21.02) * mm, "end": v(-31.29, -19.85) * mm});
            skLineSegment(sketch, "E369", {"start": v(-31.29, -19.85) * mm, "end": v(-31.07, -19.5) * mm});
            skLineSegment(sketch, "E370", {"start": v(-31.07, -19.5) * mm, "end": v(-30.38, -20.65) * mm});
            skLineSegment(sketch, "E371", {"start": v(-30.38, -20.65) * mm, "end": v(-30.36, -20.7) * mm});
            skLineSegment(sketch, "E372", {"start": v(-30.36, -20.7) * mm, "end": v(-30.3, -20.93) * mm});
            skLineSegment(sketch, "E373", {"start": v(-30.3, -20.93) * mm, "end": v(-30.2, -21.36) * mm});
            skLineSegment(sketch, "E374", {"start": v(-30.2, -21.36) * mm, "end": v(-30.1, -21.8) * mm});
            skLineSegment(sketch, "E375", {"start": v(-30.1, -21.8) * mm, "end": v(-30.05, -22.02) * mm});
            skLineSegment(sketch, "E376", {"start": v(-30.05, -22.02) * mm, "end": v(-30.03, -22.07) * mm});
            skLineSegment(sketch, "E377", {"start": v(-30.03, -22.07) * mm, "end": v(-27.68, -30.99) * mm});
            skLineSegment(sketch, "E378", {"start": v(-27.68, -30.99) * mm, "end": v(-25.33, -31.03) * mm});
            skLineSegment(sketch, "E379", {"start": v(-25.33, -31.03) * mm, "end": v(-25.21, -30.72) * mm});
            skLineSegment(sketch, "E380", {"start": v(-25.21, -30.72) * mm, "end": v(-24.92, -29.79) * mm});
            skLineSegment(sketch, "E381", {"start": v(-24.92, -29.79) * mm, "end": v(-24.35, -27.86) * mm});
            skLineSegment(sketch, "E382", {"start": v(-24.35, -27.86) * mm, "end": v(-23.7, -25.5) * mm});
            skLineSegment(sketch, "E383", {"start": v(-23.7, -25.5) * mm, "end": v(-23, -22.91) * mm});
            skLineSegment(sketch, "E384", {"start": v(-23, -22.91) * mm, "end": v(-22.35, -20.35) * mm});
            skLineSegment(sketch, "E385", {"start": v(-22.35, -20.35) * mm, "end": v(-21.8, -18.03) * mm});
            skLineSegment(sketch, "E386", {"start": v(-21.8, -18.03) * mm, "end": v(-21.41, -16.2) * mm});
            skLineSegment(sketch, "E387", {"start": v(-21.41, -16.2) * mm, "end": v(-21.27, -15.37) * mm});
            skLineSegment(sketch, "E388", {"start": v(-21.27, -15.37) * mm, "end": v(-21.26, -15.1) * mm});
            skLineSegment(sketch, "E389", {"start": v(-21.26, -15.1) * mm, "end": v(-23.26, -15.02) * mm});
            skLineSegment(sketch, "E390", {"start": v(-23.26, -15.02) * mm, "end": v(-23.5, -15.7) * mm});
            skLineSegment(sketch, "E391", {"start": v(-23.5, -15.7) * mm, "end": v(-24.02, -17.83) * mm});
            skLineSegment(sketch, "E392", {"start": v(-24.02, -17.83) * mm, "end": v(-24.77, -21.17) * mm});
            skLineSegment(sketch, "E393", {"start": v(-24.77, -21.17) * mm, "end": v(-25.56, -24.36) * mm});
            skLineSegment(sketch, "E394", {"start": v(-25.56, -24.36) * mm, "end": v(-26.17, -26.17) * mm});
            skLineSegment(sketch, "E395", {"start": v(-26.17, -26.17) * mm, "end": v(-26.49, -26.7) * mm});
            skLineSegment(sketch, "E396", {"start": v(-26.49, -26.7) * mm, "end": v(-26.5, -26.7) * mm});
            skLineSegment(sketch, "E397", {"start": v(-26.5, -26.7) * mm, "end": v(-26.58, -26.56) * mm});
            skLineSegment(sketch, "E398", {"start": v(-26.58, -26.56) * mm, "end": v(-26.65, -26.5) * mm});
            skLineSegment(sketch, "E399", {"start": v(-26.65, -26.5) * mm, "end": v(-26.85, -26.23) * mm});
            skLineSegment(sketch, "E400", {"start": v(-26.85, -26.23) * mm, "end": v(-27.22, -25.1) * mm});
            skLineSegment(sketch, "E401", {"start": v(-27.22, -25.1) * mm, "end": v(-27.7, -23.38) * mm});
            skLineSegment(sketch, "E402", {"start": v(-27.7, -23.38) * mm, "end": v(-28.24, -21.34) * mm});
            skLineSegment(sketch, "E403", {"start": v(-28.24, -21.34) * mm, "end": v(-28.8, -19.21) * mm});
            skLineSegment(sketch, "E404", {"start": v(-28.8, -19.21) * mm, "end": v(-29.3, -17.28) * mm});
            skLineSegment(sketch, "E405", {"start": v(-29.3, -17.28) * mm, "end": v(-29.7, -15.8) * mm});
            skLineSegment(sketch, "E406", {"start": v(-29.7, -15.8) * mm, "end": v(-29.87, -15.2) * mm});
            skLineSegment(sketch, "E407", {"start": v(-29.87, -15.2) * mm, "end": v(-29.96, -15.02) * mm});
            skLineSegment(sketch, "E408", {"start": v(-29.96, -15.02) * mm, "end": v(-32.13, -15.08) * mm});
            skLineSegment(sketch, "E409", {"start": v(-32.13, -15.08) * mm, "end": v(-32.4, -15.74) * mm});
            skLineSegment(sketch, "E410", {"start": v(-32.4, -15.74) * mm, "end": v(-32.92, -17.85) * mm});
            skLineSegment(sketch, "E411", {"start": v(-32.92, -17.85) * mm, "end": v(-33.68, -21.43) * mm});
            skLineSegment(sketch, "E412", {"start": v(-33.68, -21.43) * mm, "end": v(-34.46, -24.79) * mm});
            skLineSegment(sketch, "E413", {"start": v(-34.46, -24.79) * mm, "end": v(-35, -26.53) * mm});
            skLineSegment(sketch, "E414", {"start": v(-35, -26.53) * mm, "end": v(-35.3, -26.91) * mm});
            skLineSegment(sketch, "E415", {"start": v(-35.3, -26.91) * mm, "end": v(-35.62, -26.45) * mm});
            skLineSegment(sketch, "E416", {"start": v(-35.62, -26.45) * mm, "end": v(-36.2, -24.67) * mm});
            skLineSegment(sketch, "E417", {"start": v(-36.2, -24.67) * mm, "end": v(-37, -21.33) * mm});
            skLineSegment(sketch, "E418", {"start": v(-37, -21.33) * mm, "end": v(-37.79, -17.83) * mm});
            skLineSegment(sketch, "E419", {"start": v(-37.79, -17.83) * mm, "end": v(-38.32, -15.75) * mm});
            skLineSegment(sketch, "E420", {"start": v(-38.32, -15.75) * mm, "end": v(-38.59, -15.1) * mm});
            skLineSegment(sketch, "E421", {"start": v(-38.59, -15.1) * mm, "end": v(-40.63, -15) * mm});
            skLineSegment(sketch, "E422", {"start": v(-40.63, -15) * mm, "end": v(-40.63, -15.27) * mm});
            skLineSegment(sketch, "E423", {"start": v(-40.63, -15.27) * mm, "end": v(-40.49, -16.07) * mm});
            skLineSegment(sketch, "E424", {"start": v(-40.49, -16.07) * mm, "end": v(-40.1, -17.96) * mm});
            skLineSegment(sketch, "E425", {"start": v(-40.1, -17.96) * mm, "end": v(-39.53, -20.38) * mm});
            skLineSegment(sketch, "E426", {"start": v(-39.53, -20.38) * mm, "end": v(-38.85, -23.07) * mm});
            skLineSegment(sketch, "E427", {"start": v(-38.85, -23.07) * mm, "end": v(-38.14, -25.75) * mm});
            skLineSegment(sketch, "E428", {"start": v(-38.14, -25.75) * mm, "end": v(-37.47, -28.14) * mm});
            skLineSegment(sketch, "E429", {"start": v(-37.47, -28.14) * mm, "end": v(-36.91, -29.99) * mm});
            skLineSegment(sketch, "E430", {"start": v(-36.91, -29.99) * mm, "end": v(-36.66, -30.77) * mm});
            skLineSegment(sketch, "E431", {"start": v(-36.66, -30.77) * mm, "end": v(-36.53, -31) * mm});
            skLineSegment(sketch, "E432", {"start": v(-55.93, -35.1) * mm, "end": v(-56.1, -38.62) * mm});
            skLineSegment(sketch, "E433", {"start": v(-56.1, -38.62) * mm, "end": v(-55.7, -38.6) * mm});
            skLineSegment(sketch, "E434", {"start": v(-55.7, -38.6) * mm, "end": v(-54.53, -38.26) * mm});
            skLineSegment(sketch, "E435", {"start": v(-54.53, -38.26) * mm, "end": v(-53.15, -37.7) * mm});
            skLineSegment(sketch, "E436", {"start": v(-53.15, -37.7) * mm, "end": v(-51.66, -37.43) * mm});
            skLineSegment(sketch, "E437", {"start": v(-51.66, -37.43) * mm, "end": v(-50.2, -37.75) * mm});
            skLineSegment(sketch, "E438", {"start": v(-50.2, -37.75) * mm, "end": v(-49.77, -37.97) * mm});
            skLineSegment(sketch, "E439", {"start": v(-49.77, -37.97) * mm, "end": v(-49.55, -38.15) * mm});
            skLineSegment(sketch, "E440", {"start": v(-49.55, -38.15) * mm, "end": v(-49.1, -38.96) * mm});
            skLineSegment(sketch, "E441", {"start": v(-49.1, -38.96) * mm, "end": v(-49.12, -40.1) * mm});
            skLineSegment(sketch, "E442", {"start": v(-49.12, -40.1) * mm, "end": v(-49.67, -41.3) * mm});
            skLineSegment(sketch, "E443", {"start": v(-49.67, -41.3) * mm, "end": v(-50.6, -42.54) * mm});
            skLineSegment(sketch, "E444", {"start": v(-50.6, -42.54) * mm, "end": v(-51.74, -43.71) * mm});
            skLineSegment(sketch, "E445", {"start": v(-51.74, -43.71) * mm, "end": v(-52.94, -44.77) * mm});
            skLineSegment(sketch, "E446", {"start": v(-52.94, -44.77) * mm, "end": v(-54.02, -45.63) * mm});
            skLineSegment(sketch, "E447", {"start": v(-54.02, -45.63) * mm, "end": v(-54.64, -46.09) * mm});
            skLineSegment(sketch, "E448", {"start": v(-54.64, -46.09) * mm, "end": v(-54.84, -46.24) * mm});
            skLineSegment(sketch, "E449", {"start": v(-54.84, -46.24) * mm, "end": v(-54.98, -46.34) * mm});
            skLineSegment(sketch, "E450", {"start": v(-54.98, -46.34) * mm, "end": v(-55.38, -46.64) * mm});
            skLineSegment(sketch, "E451", {"start": v(-55.38, -46.64) * mm, "end": v(-55.8, -46.98) * mm});
            skLineSegment(sketch, "E452", {"start": v(-55.8, -46.98) * mm, "end": v(-56.1, -47.32) * mm});
            skLineSegment(sketch, "E453", {"start": v(-56.1, -47.32) * mm, "end": v(-56.3, -47.69) * mm});
            skLineSegment(sketch, "E454", {"start": v(-56.3, -47.69) * mm, "end": v(-56.38, -48.12) * mm});
            skLineSegment(sketch, "E455", {"start": v(-56.38, -48.12) * mm, "end": v(-56.38, -48.67) * mm});
            skLineSegment(sketch, "E456", {"start": v(-56.38, -48.67) * mm, "end": v(-56.3, -49.36) * mm});
            skLineSegment(sketch, "E457", {"start": v(-56.3, -49.36) * mm, "end": v(-56.18, -50.02) * mm});
            skLineSegment(sketch, "E458", {"start": v(-56.18, -50.02) * mm, "end": v(-56.14, -50.24) * mm});
            skLineSegment(sketch, "E459", {"start": v(-56.14, -50.24) * mm, "end": v(-44.25, -50.24) * mm});
            skLineSegment(sketch, "E460", {"start": v(-44.25, -50.24) * mm, "end": v(-44.15, -47.2) * mm});
            skLineSegment(sketch, "E461", {"start": v(-44.15, -47.2) * mm, "end": v(-50.17, -47.07) * mm});
            skLineSegment(sketch, "E462", {"start": v(-50.17, -47.07) * mm, "end": v(-50.06, -46.8) * mm});
            skLineSegment(sketch, "E463", {"start": v(-50.06, -46.8) * mm, "end": v(-49.53, -46.06) * mm});
            skLineSegment(sketch, "E464", {"start": v(-49.53, -46.06) * mm, "end": v(-48.57, -45.13) * mm});
            skLineSegment(sketch, "E465", {"start": v(-48.57, -45.13) * mm, "end": v(-47.5, -44.23) * mm});
            skLineSegment(sketch, "E466", {"start": v(-47.5, -44.23) * mm, "end": v(-46.75, -43.54) * mm});
            skLineSegment(sketch, "E467", {"start": v(-46.75, -43.54) * mm, "end": v(-46.54, -43.28) * mm});
            skLineSegment(sketch, "E468", {"start": v(-46.54, -43.28) * mm, "end": v(-46.13, -42.8) * mm});
            skLineSegment(sketch, "E469", {"start": v(-46.13, -42.8) * mm, "end": v(-45.19, -41.12) * mm});
            skLineSegment(sketch, "E470", {"start": v(-45.19, -41.12) * mm, "end": v(-44.74, -39.08) * mm});
            skLineSegment(sketch, "E471", {"start": v(-44.74, -39.08) * mm, "end": v(-45.1, -37.26) * mm});
            skLineSegment(sketch, "E472", {"start": v(-45.1, -37.26) * mm, "end": v(-46.18, -35.77) * mm});
            skLineSegment(sketch, "E473", {"start": v(-46.18, -35.77) * mm, "end": v(-47.9, -34.7) * mm});
            skLineSegment(sketch, "E474", {"start": v(-47.9, -34.7) * mm, "end": v(-50.16, -34.17) * mm});
            skLineSegment(sketch, "E475", {"start": v(-50.16, -34.17) * mm, "end": v(-52.86, -34.27) * mm});
            skLineSegment(sketch, "E476", {"start": v(-52.86, -34.27) * mm, "end": v(-55.2, -34.82) * mm});
            skLineSegment(sketch, "E477", {"start": v(-55.2, -34.82) * mm, "end": v(-55.93, -35.1) * mm});
            skLineSegment(sketch, "E478", {"start": v(-0.41, -17.06) * mm, "end": v(0.08, -17.03) * mm});
            skLineSegment(sketch, "E479", {"start": v(0.08, -17.03) * mm, "end": v(1.58, -17) * mm});
            skLineSegment(sketch, "E480", {"start": v(1.58, -17) * mm, "end": v(3.46, -17.24) * mm});
            skLineSegment(sketch, "E481", {"start": v(3.46, -17.24) * mm, "end": v(4.83, -18.11) * mm});
            skLineSegment(sketch, "E482", {"start": v(4.83, -18.11) * mm, "end": v(5.32, -19.47) * mm});
            skLineSegment(sketch, "E483", {"start": v(5.32, -19.47) * mm, "end": v(5.3, -19.91) * mm});
            skLineSegment(sketch, "E484", {"start": v(5.3, -19.91) * mm, "end": v(5.27, -20.33) * mm});
            skLineSegment(sketch, "E485", {"start": v(5.27, -20.33) * mm, "end": v(4.71, -21.58) * mm});
            skLineSegment(sketch, "E486", {"start": v(4.71, -21.58) * mm, "end": v(3.38, -22.39) * mm});
            skLineSegment(sketch, "E487", {"start": v(3.38, -22.39) * mm, "end": v(1.56, -22.62) * mm});
            skLineSegment(sketch, "E488", {"start": v(1.56, -22.62) * mm, "end": v(0.02, -22.58) * mm});
            skLineSegment(sketch, "E489", {"start": v(0.02, -22.58) * mm, "end": v(-0.5, -22.54) * mm});
            skLineSegment(sketch, "E490", {"start": v(-0.5, -22.54) * mm, "end": v(-0.41, -17.06) * mm});
            skLineSegment(sketch, "E491", {"start": v(-2.64, -31.01) * mm, "end": v(-0.63, -31.01) * mm});
            skLineSegment(sketch, "E492", {"start": v(-0.63, -31.01) * mm, "end": v(-0.45, -24.83) * mm});
            skLineSegment(sketch, "E493", {"start": v(-0.45, -24.83) * mm, "end": v(0.06, -24.8) * mm});
            skLineSegment(sketch, "E494", {"start": v(0.06, -24.8) * mm, "end": v(1.63, -24.98) * mm});
            skLineSegment(sketch, "E495", {"start": v(1.63, -24.98) * mm, "end": v(3.07, -25.63) * mm});
            skLineSegment(sketch, "E496", {"start": v(3.07, -25.63) * mm, "end": v(4.08, -26.62) * mm});
            skLineSegment(sketch, "E497", {"start": v(4.08, -26.62) * mm, "end": v(4.86, -27.79) * mm});
            skLineSegment(sketch, "E498", {"start": v(4.86, -27.79) * mm, "end": v(5.64, -28.96) * mm});
            skLineSegment(sketch, "E499", {"start": v(5.64, -28.96) * mm, "end": v(6.61, -30) * mm});
            skLineSegment(sketch, "E500", {"start": v(6.61, -30) * mm, "end": v(8, -30.71) * mm});
            skLineSegment(sketch, "E501", {"start": v(8, -30.71) * mm, "end": v(9.5, -30.97) * mm});
            skLineSegment(sketch, "E502", {"start": v(9.5, -30.97) * mm, "end": v(10, -30.96) * mm});
            skLineSegment(sketch, "E503", {"start": v(10, -30.96) * mm, "end": v(9.89, -30.5) * mm});
            skLineSegment(sketch, "E504", {"start": v(9.89, -30.5) * mm, "end": v(9.13, -29.24) * mm});
            skLineSegment(sketch, "E505", {"start": v(9.13, -29.24) * mm, "end": v(7.65, -27.5) * mm});
            skLineSegment(sketch, "E506", {"start": v(7.65, -27.5) * mm, "end": v(6.08, -25.8) * mm});
            skLineSegment(sketch, "E507", {"start": v(6.08, -25.8) * mm, "end": v(5.13, -24.6) * mm});
            skLineSegment(sketch, "E508", {"start": v(5.13, -24.6) * mm, "end": v(4.9, -24.17) * mm});
            skLineSegment(sketch, "E509", {"start": v(4.9, -24.17) * mm, "end": v(4.9, -24.17) * mm});
            skLineSegment(sketch, "E510", {"start": v(4.9, -24.17) * mm, "end": v(5.11, -24) * mm});
            skLineSegment(sketch, "E511", {"start": v(5.11, -24) * mm, "end": v(5.66, -23.52) * mm});
            skLineSegment(sketch, "E512", {"start": v(5.66, -23.52) * mm, "end": v(6.37, -22.77) * mm});
            skLineSegment(sketch, "E513", {"start": v(6.37, -22.77) * mm, "end": v(7.09, -21.8) * mm});
            skLineSegment(sketch, "E514", {"start": v(7.09, -21.8) * mm, "end": v(7.65, -20.66) * mm});
            skLineSegment(sketch, "E515", {"start": v(7.65, -20.66) * mm, "end": v(7.9, -19.38) * mm});
            skLineSegment(sketch, "E516", {"start": v(7.9, -19.38) * mm, "end": v(7.67, -18.02) * mm});
            skLineSegment(sketch, "E517", {"start": v(7.67, -18.02) * mm, "end": v(7.08, -16.92) * mm});
            skLineSegment(sketch, "E518", {"start": v(7.08, -16.92) * mm, "end": v(6.81, -16.62) * mm});
            skLineSegment(sketch, "E519", {"start": v(6.81, -16.62) * mm, "end": v(6.48, -16.23) * mm});
            skLineSegment(sketch, "E520", {"start": v(6.48, -16.23) * mm, "end": v(5.04, -15.48) * mm});
            skLineSegment(sketch, "E521", {"start": v(5.04, -15.48) * mm, "end": v(2.6, -14.97) * mm});
            skLineSegment(sketch, "E522", {"start": v(2.6, -14.97) * mm, "end": v(-0.11, -14.9) * mm});
            skLineSegment(sketch, "E523", {"start": v(-0.11, -14.9) * mm, "end": v(-2.1, -15.01) * mm});
            skLineSegment(sketch, "E524", {"start": v(-2.1, -15.01) * mm, "end": v(-2.75, -15.08) * mm});
            skLineSegment(sketch, "E525", {"start": v(-2.75, -15.08) * mm, "end": v(-2.78, -15.4) * mm});
            skLineSegment(sketch, "E526", {"start": v(-2.78, -15.4) * mm, "end": v(-2.83, -16.34) * mm});
            skLineSegment(sketch, "E527", {"start": v(-2.83, -16.34) * mm, "end": v(-2.9, -18.27) * mm});
            skLineSegment(sketch, "E528", {"start": v(-2.9, -18.27) * mm, "end": v(-2.93, -20.64) * mm});
            skLineSegment(sketch, "E529", {"start": v(-2.93, -20.64) * mm, "end": v(-2.95, -23.21) * mm});
            skLineSegment(sketch, "E530", {"start": v(-2.95, -23.21) * mm, "end": v(-2.93, -25.77) * mm});
            skLineSegment(sketch, "E531", {"start": v(-2.93, -25.77) * mm, "end": v(-2.88, -28.07) * mm});
            skLineSegment(sketch, "E532", {"start": v(-2.88, -28.07) * mm, "end": v(-2.78, -29.9) * mm});
            skLineSegment(sketch, "E533", {"start": v(-2.78, -29.9) * mm, "end": v(-2.7, -30.74) * mm});
            skLineSegment(sketch, "E534", {"start": v(-2.7, -30.74) * mm, "end": v(-2.64, -31.01) * mm});
            skLineSegment(sketch, "E535", {"start": v(-11.23, -37.68) * mm, "end": v(-3.77, -37.75) * mm});
            skLineSegment(sketch, "E536", {"start": v(-3.77, -37.75) * mm, "end": v(-3.85, -38.1) * mm});
            skLineSegment(sketch, "E537", {"start": v(-3.85, -38.1) * mm, "end": v(-4.25, -39.1) * mm});
            skLineSegment(sketch, "E538", {"start": v(-4.25, -39.1) * mm, "end": v(-5.06, -40.7) * mm});
            skLineSegment(sketch, "E539", {"start": v(-5.06, -40.7) * mm, "end": v(-6.1, -42.42) * mm});
            skLineSegment(sketch, "E540", {"start": v(-6.1, -42.42) * mm, "end": v(-7.21, -44.22) * mm});
            skLineSegment(sketch, "E541", {"start": v(-7.21, -44.22) * mm, "end": v(-8.31, -45.98) * mm});
            skLineSegment(sketch, "E542", {"start": v(-8.31, -45.98) * mm, "end": v(-9.27, -47.62) * mm});
            skLineSegment(sketch, "E543", {"start": v(-9.27, -47.62) * mm, "end": v(-9.95, -49.07) * mm});
            skLineSegment(sketch, "E544", {"start": v(-9.95, -49.07) * mm, "end": v(-10.24, -49.94) * mm});
            skLineSegment(sketch, "E545", {"start": v(-10.24, -49.94) * mm, "end": v(-10.26, -50.23) * mm});
            skLineSegment(sketch, "E546", {"start": v(-10.26, -50.23) * mm, "end": v(-6.04, -50.25) * mm});
            skLineSegment(sketch, "E547", {"start": v(-6.04, -50.25) * mm, "end": v(-5.7, -49.73) * mm});
            skLineSegment(sketch, "E548", {"start": v(-5.7, -49.73) * mm, "end": v(-3.96, -46.72) * mm});
            skLineSegment(sketch, "E549", {"start": v(-3.96, -46.72) * mm, "end": v(-2.25, -43.63) * mm});
            skLineSegment(sketch, "E550", {"start": v(-2.25, -43.63) * mm, "end": v(-1.92, -43.08) * mm});
            skLineSegment(sketch, "E551", {"start": v(-1.92, -43.08) * mm, "end": v(-1.64, -42.58) * mm});
            skLineSegment(sketch, "E552", {"start": v(-1.64, -42.58) * mm, "end": v(-0.74, -41.14) * mm});
            skLineSegment(sketch, "E553", {"start": v(-0.74, -41.14) * mm, "end": v(0.29, -39.26) * mm});
            skLineSegment(sketch, "E554", {"start": v(0.29, -39.26) * mm, "end": v(0.9, -37.15) * mm});
            skLineSegment(sketch, "E555", {"start": v(0.9, -37.15) * mm, "end": v(0.97, -35.19) * mm});
            skLineSegment(sketch, "E556", {"start": v(0.97, -35.19) * mm, "end": v(0.88, -34.55) * mm});
            skLineSegment(sketch, "E557", {"start": v(0.88, -34.55) * mm, "end": v(-11.18, -34.49) * mm});
            skLineSegment(sketch, "E558", {"start": v(-11.18, -34.49) * mm, "end": v(-11.23, -37.68) * mm});
            skLineSegment(sketch, "E559", {"start": v(15.16, -17.1) * mm, "end": v(16.04, -17) * mm});
            skLineSegment(sketch, "E560", {"start": v(16.04, -17) * mm, "end": v(18.72, -17.1) * mm});
            skLineSegment(sketch, "E561", {"start": v(18.72, -17.1) * mm, "end": v(21.51, -18.02) * mm});
            skLineSegment(sketch, "E562", {"start": v(21.51, -18.02) * mm, "end": v(23.33, -19.98) * mm});
            skLineSegment(sketch, "E563", {"start": v(23.33, -19.98) * mm, "end": v(23.96, -22.33) * mm});
            skLineSegment(sketch, "E564", {"start": v(23.96, -22.33) * mm, "end": v(23.96, -23.12) * mm});
            skLineSegment(sketch, "E565", {"start": v(23.96, -23.12) * mm, "end": v(23.95, -23.89) * mm});
            skLineSegment(sketch, "E566", {"start": v(23.95, -23.89) * mm, "end": v(23.28, -26.2) * mm});
            skLineSegment(sketch, "E567", {"start": v(23.28, -26.2) * mm, "end": v(21.44, -28.05) * mm});
            skLineSegment(sketch, "E568", {"start": v(21.44, -28.05) * mm, "end": v(18.65, -28.9) * mm});
            skLineSegment(sketch, "E569", {"start": v(18.65, -28.9) * mm, "end": v(16, -29.03) * mm});
            skLineSegment(sketch, "E570", {"start": v(16, -29.03) * mm, "end": v(15.12, -28.97) * mm});
            skLineSegment(sketch, "E571", {"start": v(15.12, -28.97) * mm, "end": v(15.16, -17.1) * mm});
            skLineSegment(sketch, "E572", {"start": v(12.9, -30.93) * mm, "end": v(13.55, -30.96) * mm});
            skLineSegment(sketch, "E573", {"start": v(13.55, -30.96) * mm, "end": v(15.51, -31.01) * mm});
            skLineSegment(sketch, "E574", {"start": v(15.51, -31.01) * mm, "end": v(17.99, -30.93) * mm});
            skLineSegment(sketch, "E575", {"start": v(17.99, -30.93) * mm, "end": v(20.25, -30.63) * mm});
            skLineSegment(sketch, "E576", {"start": v(20.25, -30.63) * mm, "end": v(22.25, -30.02) * mm});
            skLineSegment(sketch, "E577", {"start": v(22.25, -30.02) * mm, "end": v(23.91, -29.04) * mm});
            skLineSegment(sketch, "E578", {"start": v(23.91, -29.04) * mm, "end": v(25.19, -27.6) * mm});
            skLineSegment(sketch, "E579", {"start": v(25.19, -27.6) * mm, "end": v(26.01, -25.66) * mm});
            skLineSegment(sketch, "E580", {"start": v(26.01, -25.66) * mm, "end": v(26.31, -23.75) * mm});
            skLineSegment(sketch, "E581", {"start": v(26.31, -23.75) * mm, "end": v(26.32, -23.12) * mm});
            skLineSegment(sketch, "E582", {"start": v(26.32, -23.12) * mm, "end": v(26.33, -22.47) * mm});
            skLineSegment(sketch, "E583", {"start": v(26.33, -22.47) * mm, "end": v(26.07, -20.54) * mm});
            skLineSegment(sketch, "E584", {"start": v(26.07, -20.54) * mm, "end": v(25.3, -18.56) * mm});
            skLineSegment(sketch, "E585", {"start": v(25.3, -18.56) * mm, "end": v(24.06, -17.09) * mm});
            skLineSegment(sketch, "E586", {"start": v(24.06, -17.09) * mm, "end": v(22.41, -16.07) * mm});
            skLineSegment(sketch, "E587", {"start": v(22.41, -16.07) * mm, "end": v(20.43, -15.42) * mm});
            skLineSegment(sketch, "E588", {"start": v(20.43, -15.42) * mm, "end": v(18.16, -15.08) * mm});
            skLineSegment(sketch, "E589", {"start": v(18.16, -15.08) * mm, "end": v(15.67, -14.97) * mm});
            skLineSegment(sketch, "E590", {"start": v(15.67, -14.97) * mm, "end": v(13.7, -15) * mm});
            skLineSegment(sketch, "E591", {"start": v(13.7, -15) * mm, "end": v(13.03, -15.03) * mm});
            skLineSegment(sketch, "E592", {"start": v(13.03, -15.03) * mm, "end": v(12.9, -30.93) * mm});
            skLineSegment(sketch, "E593", {"start": v(-25.19, -39.17) * mm, "end": v(-22.16, -39.25) * mm});
            skLineSegment(sketch, "E594", {"start": v(-22.16, -39.25) * mm, "end": v(-22.07, -40.09) * mm});
            skLineSegment(sketch, "E595", {"start": v(-22.07, -40.09) * mm, "end": v(-21.86, -42.62) * mm});
            skLineSegment(sketch, "E596", {"start": v(-21.86, -42.62) * mm, "end": v(-21.83, -44.93) * mm});
            skLineSegment(sketch, "E597", {"start": v(-21.83, -44.93) * mm, "end": v(-22.02, -46.37) * mm});
            skLineSegment(sketch, "E598", {"start": v(-22.02, -46.37) * mm, "end": v(-22.41, -47.14) * mm});
            skLineSegment(sketch, "E599", {"start": v(-22.41, -47.14) * mm, "end": v(-22.96, -47.45) * mm});
            skLineSegment(sketch, "E600", {"start": v(-22.96, -47.45) * mm, "end": v(-23.63, -47.5) * mm});
            skLineSegment(sketch, "E601", {"start": v(-23.63, -47.5) * mm, "end": v(-24.4, -47.48) * mm});
            skLineSegment(sketch, "E602", {"start": v(-24.4, -47.48) * mm, "end": v(-25.01, -47.56) * mm});
            skLineSegment(sketch, "E603", {"start": v(-25.01, -47.56) * mm, "end": v(-25.2, -47.62) * mm});
            skLineSegment(sketch, "E604", {"start": v(-25.2, -47.62) * mm, "end": v(-25.22, -50.06) * mm});
            skLineSegment(sketch, "E605", {"start": v(-25.22, -50.06) * mm, "end": v(-24.46, -50.17) * mm});
            skLineSegment(sketch, "E606", {"start": v(-24.46, -50.17) * mm, "end": v(-20.12, -50.33) * mm});
            skLineSegment(sketch, "E607", {"start": v(-20.12, -50.33) * mm, "end": v(-15.7, -50.25) * mm});
            skLineSegment(sketch, "E608", {"start": v(-15.7, -50.25) * mm, "end": v(-14.9, -50.23) * mm});
            skLineSegment(sketch, "E609", {"start": v(-14.9, -50.23) * mm, "end": v(-14.8, -47.45) * mm});
            skLineSegment(sketch, "E610", {"start": v(-14.8, -47.45) * mm, "end": v(-17.93, -47.14) * mm});
            skLineSegment(sketch, "E611", {"start": v(-17.93, -47.14) * mm, "end": v(-17.95, -34.67) * mm});
            skLineSegment(sketch, "E612", {"start": v(-17.95, -34.67) * mm, "end": v(-18.39, -34.64) * mm});
            skLineSegment(sketch, "E613", {"start": v(-18.39, -34.64) * mm, "end": v(-19.7, -34.57) * mm});
            skLineSegment(sketch, "E614", {"start": v(-19.7, -34.57) * mm, "end": v(-20.77, -34.56) * mm});
            skLineSegment(sketch, "E615", {"start": v(-20.77, -34.56) * mm, "end": v(-21.37, -34.64) * mm});
            skLineSegment(sketch, "E616", {"start": v(-21.37, -34.64) * mm, "end": v(-21.64, -34.8) * mm});
            skLineSegment(sketch, "E617", {"start": v(-21.64, -34.8) * mm, "end": v(-21.75, -35.05) * mm});
            skLineSegment(sketch, "E618", {"start": v(-21.75, -35.05) * mm, "end": v(-21.9, -35.37) * mm});
            skLineSegment(sketch, "E619", {"start": v(-21.9, -35.37) * mm, "end": v(-22.22, -35.76) * mm});
            skLineSegment(sketch, "E620", {"start": v(-22.22, -35.76) * mm, "end": v(-22.72, -36.13) * mm});
            skLineSegment(sketch, "E621", {"start": v(-22.72, -36.13) * mm, "end": v(-22.9, -36.23) * mm});
            skLineSegment(sketch, "E622", {"start": v(-22.9, -36.23) * mm, "end": v(-23.1, -36.33) * mm});
            skLineSegment(sketch, "E623", {"start": v(-23.1, -36.33) * mm, "end": v(-23.7, -36.57) * mm});
            skLineSegment(sketch, "E624", {"start": v(-23.7, -36.57) * mm, "end": v(-24.29, -36.69) * mm});
            skLineSegment(sketch, "E625", {"start": v(-24.29, -36.69) * mm, "end": v(-24.7, -36.7) * mm});
            skLineSegment(sketch, "E626", {"start": v(-24.7, -36.7) * mm, "end": v(-24.97, -36.7) * mm});
            skLineSegment(sketch, "E627", {"start": v(-24.97, -36.7) * mm, "end": v(-25.13, -36.84) * mm});
            skLineSegment(sketch, "E628", {"start": v(-25.13, -36.84) * mm, "end": v(-25.2, -37.22) * mm});
            skLineSegment(sketch, "E629", {"start": v(-25.2, -37.22) * mm, "end": v(-25.2, -37.96) * mm});
            skLineSegment(sketch, "E630", {"start": v(-25.2, -37.96) * mm, "end": v(-25.2, -38.87) * mm});
            skLineSegment(sketch, "E631", {"start": v(-25.2, -38.87) * mm, "end": v(-25.19, -39.17) * mm});
            skLineSegment(sketch, "E632", {"start": v(29.48, -27.54) * mm, "end": v(29.44, -30.04) * mm});
            skLineSegment(sketch, "E633", {"start": v(29.44, -30.04) * mm, "end": v(30.35, -30.43) * mm});
            skLineSegment(sketch, "E634", {"start": v(30.35, -30.43) * mm, "end": v(33.24, -31.2) * mm});
            skLineSegment(sketch, "E635", {"start": v(33.24, -31.2) * mm, "end": v(36.41, -31.28) * mm});
            skLineSegment(sketch, "E636", {"start": v(36.41, -31.28) * mm, "end": v(38.9, -30.52) * mm});
            skLineSegment(sketch, "E637", {"start": v(38.9, -30.52) * mm, "end": v(40.68, -29.17) * mm});
            skLineSegment(sketch, "E638", {"start": v(40.68, -29.17) * mm, "end": v(41.68, -27.46) * mm});
            skLineSegment(sketch, "E639", {"start": v(41.68, -27.46) * mm, "end": v(41.86, -25.66) * mm});
            skLineSegment(sketch, "E640", {"start": v(41.86, -25.66) * mm, "end": v(41.17, -24) * mm});
            skLineSegment(sketch, "E641", {"start": v(41.17, -24) * mm, "end": v(40.01, -22.93) * mm});
            skLineSegment(sketch, "E642", {"start": v(40.01, -22.93) * mm, "end": v(39.56, -22.7) * mm});
            skLineSegment(sketch, "E643", {"start": v(39.56, -22.7) * mm, "end": v(39.3, -22.58) * mm});
            skLineSegment(sketch, "E644", {"start": v(39.3, -22.58) * mm, "end": v(38.47, -22.33) * mm});
            skLineSegment(sketch, "E645", {"start": v(38.47, -22.33) * mm, "end": v(37.15, -22.06) * mm});
            skLineSegment(sketch, "E646", {"start": v(37.15, -22.06) * mm, "end": v(35.74, -21.8) * mm});
            skLineSegment(sketch, "E647", {"start": v(35.74, -21.8) * mm, "end": v(34.37, -21.5) * mm});
            skLineSegment(sketch, "E648", {"start": v(34.37, -21.5) * mm, "end": v(33.19, -21.08) * mm});
            skLineSegment(sketch, "E649", {"start": v(33.19, -21.08) * mm, "end": v(32.33, -20.45) * mm});
            skLineSegment(sketch, "E650", {"start": v(32.33, -20.45) * mm, "end": v(31.93, -19.56) * mm});
            skLineSegment(sketch, "E651", {"start": v(31.93, -19.56) * mm, "end": v(32.03, -18.6) * mm});
            skLineSegment(sketch, "E652", {"start": v(32.03, -18.6) * mm, "end": v(32.14, -18.31) * mm});
            skLineSegment(sketch, "E653", {"start": v(32.14, -18.31) * mm, "end": v(32.25, -18.02) * mm});
            skLineSegment(sketch, "E654", {"start": v(32.25, -18.02) * mm, "end": v(32.88, -17.24) * mm});
            skLineSegment(sketch, "E655", {"start": v(32.88, -17.24) * mm, "end": v(33.97, -16.73) * mm});
            skLineSegment(sketch, "E656", {"start": v(33.97, -16.73) * mm, "end": v(35.3, -16.65) * mm});
            skLineSegment(sketch, "E657", {"start": v(35.3, -16.65) * mm, "end": v(36.73, -16.87) * mm});
            skLineSegment(sketch, "E658", {"start": v(36.73, -16.87) * mm, "end": v(38.14, -17.28) * mm});
            skLineSegment(sketch, "E659", {"start": v(38.14, -17.28) * mm, "end": v(39.42, -17.74) * mm});
            skLineSegment(sketch, "E660", {"start": v(39.42, -17.74) * mm, "end": v(40.43, -18.14) * mm});
            skLineSegment(sketch, "E661", {"start": v(40.43, -18.14) * mm, "end": v(40.9, -18.32) * mm});
            skLineSegment(sketch, "E662", {"start": v(40.9, -18.32) * mm, "end": v(41.07, -18.34) * mm});
            skLineSegment(sketch, "E663", {"start": v(41.07, -18.34) * mm, "end": v(41.15, -15.86) * mm});
            skLineSegment(sketch, "E664", {"start": v(41.15, -15.86) * mm, "end": v(40.64, -15.58) * mm});
            skLineSegment(sketch, "E665", {"start": v(40.64, -15.58) * mm, "end": v(38.98, -15.06) * mm});
            skLineSegment(sketch, "E666", {"start": v(38.98, -15.06) * mm, "end": v(36.34, -14.7) * mm});
            skLineSegment(sketch, "E667", {"start": v(36.34, -14.7) * mm, "end": v(33.68, -14.9) * mm});
            skLineSegment(sketch, "E668", {"start": v(33.68, -14.9) * mm, "end": v(31.92, -15.45) * mm});
            skLineSegment(sketch, "E669", {"start": v(31.92, -15.45) * mm, "end": v(31.43, -15.78) * mm});
            skLineSegment(sketch, "E670", {"start": v(31.43, -15.78) * mm, "end": v(30.97, -16.1) * mm});
            skLineSegment(sketch, "E671", {"start": v(30.97, -16.1) * mm, "end": v(29.9, -17.52) * mm});
            skLineSegment(sketch, "E672", {"start": v(29.9, -17.52) * mm, "end": v(29.45, -19.68) * mm});
            skLineSegment(sketch, "E673", {"start": v(29.45, -19.68) * mm, "end": v(30.18, -21.77) * mm});
            skLineSegment(sketch, "E674", {"start": v(30.18, -21.77) * mm, "end": v(31.64, -23.09) * mm});
            skLineSegment(sketch, "E675", {"start": v(31.64, -23.09) * mm, "end": v(32.2, -23.32) * mm});
            skLineSegment(sketch, "E676", {"start": v(32.2, -23.32) * mm, "end": v(32.45, -23.42) * mm});
            skLineSegment(sketch, "E677", {"start": v(32.45, -23.42) * mm, "end": v(33.2, -23.6) * mm});
            skLineSegment(sketch, "E678", {"start": v(33.2, -23.6) * mm, "end": v(34.46, -23.85) * mm});
            skLineSegment(sketch, "E679", {"start": v(34.46, -23.85) * mm, "end": v(35.84, -24.1) * mm});
            skLineSegment(sketch, "E680", {"start": v(35.84, -24.1) * mm, "end": v(37.2, -24.44) * mm});
            skLineSegment(sketch, "E681", {"start": v(37.2, -24.44) * mm, "end": v(38.35, -24.91) * mm});
            skLineSegment(sketch, "E682", {"start": v(38.35, -24.91) * mm, "end": v(39.16, -25.57) * mm});
            skLineSegment(sketch, "E683", {"start": v(39.16, -25.57) * mm, "end": v(39.48, -26.47) * mm});
            skLineSegment(sketch, "E684", {"start": v(39.48, -26.47) * mm, "end": v(39.27, -27.41) * mm});
            skLineSegment(sketch, "E685", {"start": v(39.27, -27.41) * mm, "end": v(39.13, -27.69) * mm});
            skLineSegment(sketch, "E686", {"start": v(39.13, -27.69) * mm, "end": v(38.98, -27.98) * mm});
            skLineSegment(sketch, "E687", {"start": v(38.98, -27.98) * mm, "end": v(38.27, -28.7) * mm});
            skLineSegment(sketch, "E688", {"start": v(38.27, -28.7) * mm, "end": v(37.14, -29.2) * mm});
            skLineSegment(sketch, "E689", {"start": v(37.14, -29.2) * mm, "end": v(35.82, -29.3) * mm});
            skLineSegment(sketch, "E690", {"start": v(35.82, -29.3) * mm, "end": v(34.4, -29.1) * mm});
            skLineSegment(sketch, "E691", {"start": v(34.4, -29.1) * mm, "end": v(32.97, -28.7) * mm});
            skLineSegment(sketch, "E692", {"start": v(32.97, -28.7) * mm, "end": v(31.61, -28.24) * mm});
            skLineSegment(sketch, "E693", {"start": v(31.61, -28.24) * mm, "end": v(30.42, -27.82) * mm});
            skLineSegment(sketch, "E694", {"start": v(30.42, -27.82) * mm, "end": v(29.72, -27.59) * mm});
            skLineSegment(sketch, "E695", {"start": v(29.72, -27.59) * mm, "end": v(29.48, -27.54) * mm});
            skLineSegment(sketch, "E696", {"start": v(-15.24, -24.56) * mm, "end": v(-15.2, -24.14) * mm});
            skLineSegment(sketch, "E697", {"start": v(-15.2, -24.14) * mm, "end": v(-14.92, -22.9) * mm});
            skLineSegment(sketch, "E698", {"start": v(-14.92, -22.9) * mm, "end": v(-14.29, -20.86) * mm});
            skLineSegment(sketch, "E699", {"start": v(-14.29, -20.86) * mm, "end": v(-13.5, -19) * mm});
            skLineSegment(sketch, "E700", {"start": v(-13.5, -19) * mm, "end": v(-12.97, -18.1) * mm});
            skLineSegment(sketch, "E701", {"start": v(-12.97, -18.1) * mm, "end": v(-12.73, -17.92) * mm});
            skLineSegment(sketch, "E702", {"start": v(-12.73, -17.92) * mm, "end": v(-12.56, -18.19) * mm});
            skLineSegment(sketch, "E703", {"start": v(-12.56, -18.19) * mm, "end": v(-12.1, -19.21) * mm});
            skLineSegment(sketch, "E704", {"start": v(-12.1, -19.21) * mm, "end": v(-11.4, -21.11) * mm});
            skLineSegment(sketch, "E705", {"start": v(-11.4, -21.11) * mm, "end": v(-10.82, -23.08) * mm});
            skLineSegment(sketch, "E706", {"start": v(-10.82, -23.08) * mm, "end": v(-10.55, -24.22) * mm});
            skLineSegment(sketch, "E707", {"start": v(-10.55, -24.22) * mm, "end": v(-10.53, -24.59) * mm});
            skLineSegment(sketch, "E708", {"start": v(-10.53, -24.59) * mm, "end": v(-12.02, -24.61) * mm});
            skLineSegment(sketch, "E709", {"start": v(-12.02, -24.61) * mm, "end": v(-13.79, -24.62) * mm});
            skLineSegment(sketch, "E710", {"start": v(-13.79, -24.62) * mm, "end": v(-15.24, -24.56) * mm});
            skLineSegment(sketch, "E711", {"start": v(-19.87, -30.96) * mm, "end": v(-19.66, -30.96) * mm});
            skLineSegment(sketch, "E712", {"start": v(-19.66, -30.96) * mm, "end": v(-19.04, -31) * mm});
            skLineSegment(sketch, "E713", {"start": v(-19.04, -31) * mm, "end": v(-18.45, -31) * mm});
            skLineSegment(sketch, "E714", {"start": v(-18.45, -31) * mm, "end": v(-18.03, -30.94) * mm});
            skLineSegment(sketch, "E715", {"start": v(-18.03, -30.94) * mm, "end": v(-17.73, -30.7) * mm});
            skLineSegment(sketch, "E716", {"start": v(-17.73, -30.7) * mm, "end": v(-17.46, -30.24) * mm});
            skLineSegment(sketch, "E717", {"start": v(-17.46, -30.24) * mm, "end": v(-17.16, -29.47) * mm});
            skLineSegment(sketch, "E718", {"start": v(-17.16, -29.47) * mm, "end": v(-16.76, -28.32) * mm});
            skLineSegment(sketch, "E719", {"start": v(-16.76, -28.32) * mm, "end": v(-16.34, -27.12) * mm});
            skLineSegment(sketch, "E720", {"start": v(-16.34, -27.12) * mm, "end": v(-16.2, -26.72) * mm});
            skLineSegment(sketch, "E721", {"start": v(-16.2, -26.72) * mm, "end": v(-9.55, -26.72) * mm});
            skLineSegment(sketch, "E722", {"start": v(-9.55, -26.72) * mm, "end": v(-9.4, -26.98) * mm});
            skLineSegment(sketch, "E723", {"start": v(-9.4, -26.98) * mm, "end": v(-9.07, -27.8) * mm});
            skLineSegment(sketch, "E724", {"start": v(-9.07, -27.8) * mm, "end": v(-8.7, -28.93) * mm});
            skLineSegment(sketch, "E725", {"start": v(-8.7, -28.93) * mm, "end": v(-8.34, -30.02) * mm});
            skLineSegment(sketch, "E726", {"start": v(-8.34, -30.02) * mm, "end": v(-8.03, -30.75) * mm});
            skLineSegment(sketch, "E727", {"start": v(-8.03, -30.75) * mm, "end": v(-7.9, -30.97) * mm});
            skLineSegment(sketch, "E728", {"start": v(-7.9, -30.97) * mm, "end": v(-5.84, -31.05) * mm});
            skLineSegment(sketch, "E729", {"start": v(-5.84, -31.05) * mm, "end": v(-5.81, -30.8) * mm});
            skLineSegment(sketch, "E730", {"start": v(-5.81, -30.8) * mm, "end": v(-6, -30) * mm});
            skLineSegment(sketch, "E731", {"start": v(-6, -30) * mm, "end": v(-6.51, -28.17) * mm});
            skLineSegment(sketch, "E732", {"start": v(-6.51, -28.17) * mm, "end": v(-7.28, -25.8) * mm});
            skLineSegment(sketch, "E733", {"start": v(-7.28, -25.8) * mm, "end": v(-8.2, -23.16) * mm});
            skLineSegment(sketch, "E734", {"start": v(-8.2, -23.16) * mm, "end": v(-9.18, -20.5) * mm});
            skLineSegment(sketch, "E735", {"start": v(-9.18, -20.5) * mm, "end": v(-10.1, -18.1) * mm});
            skLineSegment(sketch, "E736", {"start": v(-10.1, -18.1) * mm, "end": v(-10.86, -16.2) * mm});
            skLineSegment(sketch, "E737", {"start": v(-10.86, -16.2) * mm, "end": v(-11.21, -15.35) * mm});
            skLineSegment(sketch, "E738", {"start": v(-11.21, -15.35) * mm, "end": v(-11.35, -15.07) * mm});
            skLineSegment(sketch, "E739", {"start": v(-11.35, -15.07) * mm, "end": v(-14.2, -14.98) * mm});
            skLineSegment(sketch, "E740", {"start": v(-14.2, -14.98) * mm, "end": v(-14.33, -15.24) * mm});
            skLineSegment(sketch, "E741", {"start": v(-14.33, -15.24) * mm, "end": v(-14.68, -16.07) * mm});
            skLineSegment(sketch, "E742", {"start": v(-14.68, -16.07) * mm, "end": v(-15.43, -17.92) * mm});
            skLineSegment(sketch, "E743", {"start": v(-15.43, -17.92) * mm, "end": v(-16.33, -20.27) * mm});
            skLineSegment(sketch, "E744", {"start": v(-16.33, -20.27) * mm, "end": v(-17.3, -22.89) * mm});
            skLineSegment(sketch, "E745", {"start": v(-17.3, -22.89) * mm, "end": v(-18.23, -25.52) * mm});
            skLineSegment(sketch, "E746", {"start": v(-18.23, -25.52) * mm, "end": v(-19.04, -27.9) * mm});
            skLineSegment(sketch, "E747", {"start": v(-19.04, -27.9) * mm, "end": v(-19.62, -29.8) * mm});
            skLineSegment(sketch, "E748", {"start": v(-19.62, -29.8) * mm, "end": v(-19.85, -30.66) * mm});
            skLineSegment(sketch, "E749", {"start": v(-19.85, -30.66) * mm, "end": v(-19.87, -30.96) * mm});
            skLineSegment(sketch, "E750", {"start": v(-49.06, -17.87) * mm, "end": v(-48.9, -18.2) * mm});
            skLineSegment(sketch, "E751", {"start": v(-48.9, -18.2) * mm, "end": v(-48.44, -19.28) * mm});
            skLineSegment(sketch, "E752", {"start": v(-48.44, -19.28) * mm, "end": v(-47.75, -21.19) * mm});
            skLineSegment(sketch, "E753", {"start": v(-47.75, -21.19) * mm, "end": v(-47.17, -23.1) * mm});
            skLineSegment(sketch, "E754", {"start": v(-47.17, -23.1) * mm, "end": v(-46.9, -24.21) * mm});
            skLineSegment(sketch, "E755", {"start": v(-46.9, -24.21) * mm, "end": v(-46.87, -24.58) * mm});
            skLineSegment(sketch, "E756", {"start": v(-46.87, -24.58) * mm, "end": v(-51.58, -24.6) * mm});
            skLineSegment(sketch, "E757", {"start": v(-51.58, -24.6) * mm, "end": v(-51.56, -24.26) * mm});
            skLineSegment(sketch, "E758", {"start": v(-51.56, -24.26) * mm, "end": v(-51.21, -22.77) * mm});
            skLineSegment(sketch, "E759", {"start": v(-51.21, -22.77) * mm, "end": v(-50.68, -21.25) * mm});
            skLineSegment(sketch, "E760", {"start": v(-50.68, -21.25) * mm, "end": v(-50.55, -20.89) * mm});
            skLineSegment(sketch, "E761", {"start": v(-50.55, -20.89) * mm, "end": v(-49.69, -18.62) * mm});
            skLineSegment(sketch, "E762", {"start": v(-49.69, -18.62) * mm, "end": v(-49.63, -18.53) * mm});
            skLineSegment(sketch, "E763", {"start": v(-49.63, -18.53) * mm, "end": v(-49.47, -18.24) * mm});
            skLineSegment(sketch, "E764", {"start": v(-49.47, -18.24) * mm, "end": v(-49.35, -18.03) * mm});
            skLineSegment(sketch, "E765", {"start": v(-49.35, -18.03) * mm, "end": v(-49.3, -17.95) * mm});
            skLineSegment(sketch, "E766", {"start": v(-49.3, -17.95) * mm, "end": v(-49.3, -17.95) * mm});
            skLineSegment(sketch, "E767", {"start": v(-49.3, -17.95) * mm, "end": v(-49.31, -18) * mm});
            skLineSegment(sketch, "E768", {"start": v(-49.31, -18) * mm, "end": v(-49.3, -18.02) * mm});
            skLineSegment(sketch, "E769", {"start": v(-49.3, -18.02) * mm, "end": v(-49.22, -18) * mm});
            skLineSegment(sketch, "E770", {"start": v(-49.22, -18) * mm, "end": v(-49.1, -17.9) * mm});
            skLineSegment(sketch, "E771", {"start": v(-49.1, -17.9) * mm, "end": v(-49.06, -17.87) * mm});
            skLineSegment(sketch, "E772", {"start": v(-56.2, -30.95) * mm, "end": v(-55.93, -30.95) * mm});
            skLineSegment(sketch, "E773", {"start": v(-55.93, -30.95) * mm, "end": v(-55.12, -30.95) * mm});
            skLineSegment(sketch, "E774", {"start": v(-55.12, -30.95) * mm, "end": v(-54.43, -30.89) * mm});
            skLineSegment(sketch, "E775", {"start": v(-54.43, -30.89) * mm, "end": v(-54.02, -30.7) * mm});
            skLineSegment(sketch, "E776", {"start": v(-54.02, -30.7) * mm, "end": v(-53.8, -30.37) * mm});
            skLineSegment(sketch, "E777", {"start": v(-53.8, -30.37) * mm, "end": v(-53.65, -29.84) * mm});
            skLineSegment(sketch, "E778", {"start": v(-53.65, -29.84) * mm, "end": v(-53.47, -29.1) * mm});
            skLineSegment(sketch, "E779", {"start": v(-53.47, -29.1) * mm, "end": v(-53.15, -28.08) * mm});
            skLineSegment(sketch, "E780", {"start": v(-53.15, -28.08) * mm, "end": v(-52.75, -27.1) * mm});
            skLineSegment(sketch, "E781", {"start": v(-52.75, -27.1) * mm, "end": v(-52.6, -26.77) * mm});
            skLineSegment(sketch, "E782", {"start": v(-52.6, -26.77) * mm, "end": v(-45.9, -26.63) * mm});
            skLineSegment(sketch, "E783", {"start": v(-45.9, -26.63) * mm, "end": v(-45.75, -27) * mm});
            skLineSegment(sketch, "E784", {"start": v(-45.75, -27) * mm, "end": v(-45.34, -28.14) * mm});
            skLineSegment(sketch, "E785", {"start": v(-45.34, -28.14) * mm, "end": v(-44.97, -29.26) * mm});
            skLineSegment(sketch, "E786", {"start": v(-44.97, -29.26) * mm, "end": v(-44.73, -30.05) * mm});
            skLineSegment(sketch, "E787", {"start": v(-44.73, -30.05) * mm, "end": v(-44.51, -30.55) * mm});
            skLineSegment(sketch, "E788", {"start": v(-44.51, -30.55) * mm, "end": v(-44.24, -30.83) * mm});
            skLineSegment(sketch, "E789", {"start": v(-44.24, -30.83) * mm, "end": v(-43.82, -30.96) * mm});
            skLineSegment(sketch, "E790", {"start": v(-43.82, -30.96) * mm, "end": v(-43.17, -30.98) * mm});
            skLineSegment(sketch, "E791", {"start": v(-43.17, -30.98) * mm, "end": v(-42.45, -30.96) * mm});
            skLineSegment(sketch, "E792", {"start": v(-42.45, -30.96) * mm, "end": v(-42.2, -30.96) * mm});
            skLineSegment(sketch, "E793", {"start": v(-42.2, -30.96) * mm, "end": v(-42.22, -30.65) * mm});
            skLineSegment(sketch, "E794", {"start": v(-42.22, -30.65) * mm, "end": v(-42.44, -29.76) * mm});
            skLineSegment(sketch, "E795", {"start": v(-42.44, -29.76) * mm, "end": v(-43, -27.87) * mm});
            skLineSegment(sketch, "E796", {"start": v(-43, -27.87) * mm, "end": v(-43.76, -25.54) * mm});
            skLineSegment(sketch, "E797", {"start": v(-43.76, -25.54) * mm, "end": v(-44.67, -22.97) * mm});
            skLineSegment(sketch, "E798", {"start": v(-44.67, -22.97) * mm, "end": v(-45.6, -20.42) * mm});
            skLineSegment(sketch, "E799", {"start": v(-45.6, -20.42) * mm, "end": v(-46.48, -18.1) * mm});
            skLineSegment(sketch, "E800", {"start": v(-46.48, -18.1) * mm, "end": v(-47.21, -16.23) * mm});
            skLineSegment(sketch, "E801", {"start": v(-47.21, -16.23) * mm, "end": v(-47.57, -15.36) * mm});
            skLineSegment(sketch, "E802", {"start": v(-47.57, -15.36) * mm, "end": v(-47.7, -15.07) * mm});
            skLineSegment(sketch, "E803", {"start": v(-47.7, -15.07) * mm, "end": v(-50.72, -15.05) * mm});
            skLineSegment(sketch, "E804", {"start": v(-50.72, -15.05) * mm, "end": v(-50.85, -15.44) * mm});
            skLineSegment(sketch, "E805", {"start": v(-50.85, -15.44) * mm, "end": v(-51.28, -16.6) * mm});
            skLineSegment(sketch, "E806", {"start": v(-51.28, -16.6) * mm, "end": v(-52.04, -18.6) * mm});
            skLineSegment(sketch, "E807", {"start": v(-52.04, -18.6) * mm, "end": v(-52.91, -20.87) * mm});
            skLineSegment(sketch, "E808", {"start": v(-52.91, -20.87) * mm, "end": v(-53.82, -23.28) * mm});
            skLineSegment(sketch, "E809", {"start": v(-53.82, -23.28) * mm, "end": v(-54.69, -25.64) * mm});
            skLineSegment(sketch, "E810", {"start": v(-54.69, -25.64) * mm, "end": v(-55.42, -27.82) * mm});
            skLineSegment(sketch, "E811", {"start": v(-55.42, -27.82) * mm, "end": v(-55.95, -29.64) * mm});
            skLineSegment(sketch, "E812", {"start": v(-55.95, -29.64) * mm, "end": v(-56.17, -30.62) * mm});
            skLineSegment(sketch, "E813", {"start": v(-56.17, -30.62) * mm, "end": v(-56.2, -30.95) * mm});
            skLineSegment(sketch, "E814", {"start": v(-72.88, 0) * mm, "end": v(69.81, 0) * mm, "construction": true});
            skSolve(sketch);
        }
        {
            var Q0;
            Q0=makeQuery(id+"F16.imprint","IMPRINT",FACE,{"disambiguationData":[TD([[makeQuery(id+"F16.imprint","IMPRINT",EDGE,{"derivedFrom":sQuery(id+"F16.wireOp",EDGE,"E432")}),1.0]])]});
            var Q1;
            Q1=makeQuery(id+"F16.imprint","IMPRINT",FACE,{"disambiguationData":[TD([[makeQuery(id+"F16.imprint","IMPRINT",EDGE,{"derivedFrom":sQuery(id+"F16.wireOp",EDGE,"E300")}),1.0]])]});
            var Q2;
            Q2=makeQuery(id+"F16.imprint","IMPRINT",FACE,{"disambiguationData":[TD([[makeQuery(id+"F16.imprint","IMPRINT",EDGE,{"derivedFrom":sQuery(id+"F16.wireOp",EDGE,"E593")}),1.0]])]});
            var Q3;
            Q3=makeQuery(id+"F16.imprint","IMPRINT",FACE,{"disambiguationData":[TD([[makeQuery(id+"F16.imprint","IMPRINT",EDGE,{"derivedFrom":sQuery(id+"F16.wireOp",EDGE,"E535")}),1.0]])]});
            var Q4;
            Q4=makeQuery(id+"F16.imprint","IMPRINT",FACE,{"disambiguationData":[TD([[makeQuery(id+"F16.imprint","IMPRINT",EDGE,{"derivedFrom":sQuery(id+"F16.wireOp",EDGE,"E632")}),1.0]])]});
            var Q5;
            Q5=makeQuery(id+"F16.imprint","IMPRINT",FACE,{"disambiguationData":[TD([[makeQuery(id+"F16.imprint","IMPRINT",EDGE,{"derivedFrom":sQuery(id+"F16.wireOp",EDGE,"E559")}),1.0]])]});
            var Q6;
            Q6=makeQuery(id+"F16.imprint","IMPRINT",FACE,{"disambiguationData":[TD([[makeQuery(id+"F16.imprint","IMPRINT",EDGE,{"derivedFrom":sQuery(id+"F16.wireOp",EDGE,"E478")}),1.0]])]});
            var Q7;
            Q7=makeQuery(id+"F16.imprint","IMPRINT",FACE,{"disambiguationData":[TD([[makeQuery(id+"F16.imprint","IMPRINT",EDGE,{"derivedFrom":sQuery(id+"F16.wireOp",EDGE,"E696")}),1.0]])]});
            var Q8;
            Q8=makeQuery(id+"F16.imprint","IMPRINT",FACE,{"disambiguationData":[TD([[makeQuery(id+"F16.imprint","IMPRINT",EDGE,{"derivedFrom":sQuery(id+"F16.wireOp",EDGE,"E354")}),1.0]])]});
            var Q9;
            Q9=makeQuery(id+"F16.imprint","IMPRINT",FACE,{"disambiguationData":[TD([[makeQuery(id+"F16.imprint","IMPRINT",EDGE,{"derivedFrom":sQuery(id+"F16.wireOp",EDGE,"E750")}),1.0]])]});
            var Q10;
            Q10=makeQuery(id+"F16.imprint","IMPRINT",FACE,{"disambiguationData":[TD([[makeQuery(id+"F16.imprint","IMPRINT",EDGE,{"derivedFrom":sQuery(id+"F16.wireOp",EDGE,"E116")}),1.0]])]});
            var Q11;
            Q11=makeQuery(id+"F16.imprint","IMPRINT",FACE,{"disambiguationData":[TD([[makeQuery(id+"F16.imprint","IMPRINT",EDGE,{"derivedFrom":sQuery(id+"F16.wireOp",EDGE,"E47")}),1.0]])]});
            var Q12;
            Q12=makeQuery(id+"F16.imprint","IMPRINT",FACE,{"disambiguationData":[TD([[makeQuery(id+"F16.imprint","IMPRINT",EDGE,{"derivedFrom":sQuery(id+"F16.wireOp",EDGE,"E235")}),1.0]])]});
            var Q13;
            Q13=makeQuery(id+"F16.imprint","IMPRINT",FACE,{"disambiguationData":[TD([[makeQuery(id+"F16.imprint","IMPRINT",EDGE,{"derivedFrom":sQuery(id+"F16.wireOp",EDGE,"E275")}),1.0]])]});
            extrude(context, id + "F17", {"entities" : qUnion([Q0, Q1, Q2, Q3, Q4, Q5, Q6, Q7, Q8, Q9, Q10, Q11, Q12, Q13]), "oppositeDirection" : true, "depth" : 3 * mm, "offsetDistance" : 25 * mm});
        }
        {
            var Q0;
            Q0=makeQuery(id+"F17.opExtrude","SWEPT_BODY",BODY,{"disambiguationData":[OSD([sQuery(id+"F16.wireOp",EDGE,"E47"),sQuery(id+"F16.wireOp",EDGE,"E48"),sQuery(id+"F16.wireOp",EDGE,"E49"),sQuery(id+"F16.wireOp",EDGE,"E50"),sQuery(id+"F16.wireOp",EDGE,"E51"),sQuery(id+"F16.wireOp",EDGE,"E52"),sQuery(id+"F16.wireOp",EDGE,"E53"),sQuery(id+"F16.wireOp",EDGE,"E54"),sQuery(id+"F16.wireOp",EDGE,"E55"),sQuery(id+"F16.wireOp",EDGE,"E56"),sQuery(id+"F16.wireOp",EDGE,"E57"),sQuery(id+"F16.wireOp",EDGE,"E58"),sQuery(id+"F16.wireOp",EDGE,"E59"),sQuery(id+"F16.wireOp",EDGE,"E60"),sQuery(id+"F16.wireOp",EDGE,"E61"),sQuery(id+"F16.wireOp",EDGE,"E62"),sQuery(id+"F16.wireOp",EDGE,"E63"),sQuery(id+"F16.wireOp",EDGE,"E64"),sQuery(id+"F16.wireOp",EDGE,"E65"),sQuery(id+"F16.wireOp",EDGE,"E66"),sQuery(id+"F16.wireOp",EDGE,"E67"),sQuery(id+"F16.wireOp",EDGE,"E68"),sQuery(id+"F16.wireOp",EDGE,"E69"),sQuery(id+"F16.wireOp",EDGE,"E70"),sQuery(id+"F16.wireOp",EDGE,"E71"),sQuery(id+"F16.wireOp",EDGE,"E72"),sQuery(id+"F16.wireOp",EDGE,"E73"),sQuery(id+"F16.wireOp",EDGE,"E74"),sQuery(id+"F16.wireOp",EDGE,"E75"),sQuery(id+"F16.wireOp",EDGE,"E76"),sQuery(id+"F16.wireOp",EDGE,"E77"),sQuery(id+"F16.wireOp",EDGE,"E78"),sQuery(id+"F16.wireOp",EDGE,"E79"),sQuery(id+"F16.wireOp",EDGE,"E80"),sQuery(id+"F16.wireOp",EDGE,"E81"),sQuery(id+"F16.wireOp",EDGE,"E82"),sQuery(id+"F16.wireOp",EDGE,"E83"),sQuery(id+"F16.wireOp",EDGE,"E84"),sQuery(id+"F16.wireOp",EDGE,"E85"),sQuery(id+"F16.wireOp",EDGE,"E86"),sQuery(id+"F16.wireOp",EDGE,"E87"),sQuery(id+"F16.wireOp",EDGE,"E88"),sQuery(id+"F16.wireOp",EDGE,"E89"),sQuery(id+"F16.wireOp",EDGE,"E90"),sQuery(id+"F16.wireOp",EDGE,"E91"),sQuery(id+"F16.wireOp",EDGE,"E92"),sQuery(id+"F16.wireOp",EDGE,"E93"),sQuery(id+"F16.wireOp",EDGE,"E94"),sQuery(id+"F16.wireOp",EDGE,"E95"),sQuery(id+"F16.wireOp",EDGE,"E96"),sQuery(id+"F16.wireOp",EDGE,"E97"),sQuery(id+"F16.wireOp",EDGE,"E98"),sQuery(id+"F16.wireOp",EDGE,"E99"),sQuery(id+"F16.wireOp",EDGE,"E100"),sQuery(id+"F16.wireOp",EDGE,"E101"),sQuery(id+"F16.wireOp",EDGE,"E102"),sQuery(id+"F16.wireOp",EDGE,"E103"),sQuery(id+"F16.wireOp",EDGE,"E104"),sQuery(id+"F16.wireOp",EDGE,"E105"),sQuery(id+"F16.wireOp",EDGE,"E106"),sQuery(id+"F16.wireOp",EDGE,"E107"),sQuery(id+"F16.wireOp",EDGE,"E108"),sQuery(id+"F16.wireOp",EDGE,"E109"),sQuery(id+"F16.wireOp",EDGE,"E110"),sQuery(id+"F16.wireOp",EDGE,"E111"),sQuery(id+"F16.wireOp",EDGE,"E112"),sQuery(id+"F16.wireOp",EDGE,"E113"),sQuery(id+"F16.wireOp",EDGE,"E114"),sQuery(id+"F16.wireOp",EDGE,"E115")])]});
            var Q1;
            Q1=makeQuery(id+"F17.opExtrude","SWEPT_BODY",BODY,{"disambiguationData":[OSD([sQuery(id+"F16.wireOp",EDGE,"E116"),sQuery(id+"F16.wireOp",EDGE,"E117"),sQuery(id+"F16.wireOp",EDGE,"E118"),sQuery(id+"F16.wireOp",EDGE,"E119"),sQuery(id+"F16.wireOp",EDGE,"E120"),sQuery(id+"F16.wireOp",EDGE,"E121"),sQuery(id+"F16.wireOp",EDGE,"E122"),sQuery(id+"F16.wireOp",EDGE,"E123"),sQuery(id+"F16.wireOp",EDGE,"E124"),sQuery(id+"F16.wireOp",EDGE,"E125"),sQuery(id+"F16.wireOp",EDGE,"E126"),sQuery(id+"F16.wireOp",EDGE,"E127"),sQuery(id+"F16.wireOp",EDGE,"E128"),sQuery(id+"F16.wireOp",EDGE,"E129"),sQuery(id+"F16.wireOp",EDGE,"E130"),sQuery(id+"F16.wireOp",EDGE,"E131"),sQuery(id+"F16.wireOp",EDGE,"E132"),sQuery(id+"F16.wireOp",EDGE,"E133"),sQuery(id+"F16.wireOp",EDGE,"E134"),sQuery(id+"F16.wireOp",EDGE,"E135"),sQuery(id+"F16.wireOp",EDGE,"E136"),sQuery(id+"F16.wireOp",EDGE,"E137"),sQuery(id+"F16.wireOp",EDGE,"E138"),sQuery(id+"F16.wireOp",EDGE,"E139"),sQuery(id+"F16.wireOp",EDGE,"E140"),sQuery(id+"F16.wireOp",EDGE,"E141"),sQuery(id+"F16.wireOp",EDGE,"E142"),sQuery(id+"F16.wireOp",EDGE,"E143"),sQuery(id+"F16.wireOp",EDGE,"E144"),sQuery(id+"F16.wireOp",EDGE,"E145"),sQuery(id+"F16.wireOp",EDGE,"E146"),sQuery(id+"F16.wireOp",EDGE,"E147"),sQuery(id+"F16.wireOp",EDGE,"E148"),sQuery(id+"F16.wireOp",EDGE,"E149"),sQuery(id+"F16.wireOp",EDGE,"E150"),sQuery(id+"F16.wireOp",EDGE,"E151"),sQuery(id+"F16.wireOp",EDGE,"E152"),sQuery(id+"F16.wireOp",EDGE,"E153"),sQuery(id+"F16.wireOp",EDGE,"E154"),sQuery(id+"F16.wireOp",EDGE,"E155"),sQuery(id+"F16.wireOp",EDGE,"E156"),sQuery(id+"F16.wireOp",EDGE,"E157"),sQuery(id+"F16.wireOp",EDGE,"E158"),sQuery(id+"F16.wireOp",EDGE,"E159"),sQuery(id+"F16.wireOp",EDGE,"E160"),sQuery(id+"F16.wireOp",EDGE,"E161"),sQuery(id+"F16.wireOp",EDGE,"E162"),sQuery(id+"F16.wireOp",EDGE,"E163"),sQuery(id+"F16.wireOp",EDGE,"E164"),sQuery(id+"F16.wireOp",EDGE,"E165"),sQuery(id+"F16.wireOp",EDGE,"E166"),sQuery(id+"F16.wireOp",EDGE,"E167"),sQuery(id+"F16.wireOp",EDGE,"E168"),sQuery(id+"F16.wireOp",EDGE,"E169"),sQuery(id+"F16.wireOp",EDGE,"E170"),sQuery(id+"F16.wireOp",EDGE,"E171"),sQuery(id+"F16.wireOp",EDGE,"E172"),sQuery(id+"F16.wireOp",EDGE,"E173"),sQuery(id+"F16.wireOp",EDGE,"E174"),sQuery(id+"F16.wireOp",EDGE,"E175"),sQuery(id+"F16.wireOp",EDGE,"E176"),sQuery(id+"F16.wireOp",EDGE,"E177"),sQuery(id+"F16.wireOp",EDGE,"E178"),sQuery(id+"F16.wireOp",EDGE,"E179"),sQuery(id+"F16.wireOp",EDGE,"E180"),sQuery(id+"F16.wireOp",EDGE,"E181"),sQuery(id+"F16.wireOp",EDGE,"E182"),sQuery(id+"F16.wireOp",EDGE,"E183"),sQuery(id+"F16.wireOp",EDGE,"E184"),sQuery(id+"F16.wireOp",EDGE,"E185"),sQuery(id+"F16.wireOp",EDGE,"E186"),sQuery(id+"F16.wireOp",EDGE,"E187"),sQuery(id+"F16.wireOp",EDGE,"E188"),sQuery(id+"F16.wireOp",EDGE,"E189"),sQuery(id+"F16.wireOp",EDGE,"E190"),sQuery(id+"F16.wireOp",EDGE,"E191"),sQuery(id+"F16.wireOp",EDGE,"E192"),sQuery(id+"F16.wireOp",EDGE,"E193"),sQuery(id+"F16.wireOp",EDGE,"E194"),sQuery(id+"F16.wireOp",EDGE,"E195"),sQuery(id+"F16.wireOp",EDGE,"E196"),sQuery(id+"F16.wireOp",EDGE,"E197"),sQuery(id+"F16.wireOp",EDGE,"E198"),sQuery(id+"F16.wireOp",EDGE,"E199"),sQuery(id+"F16.wireOp",EDGE,"E200"),sQuery(id+"F16.wireOp",EDGE,"E201"),sQuery(id+"F16.wireOp",EDGE,"E202"),sQuery(id+"F16.wireOp",EDGE,"E203"),sQuery(id+"F16.wireOp",EDGE,"E204"),sQuery(id+"F16.wireOp",EDGE,"E205"),sQuery(id+"F16.wireOp",EDGE,"E206"),sQuery(id+"F16.wireOp",EDGE,"E207"),sQuery(id+"F16.wireOp",EDGE,"E208"),sQuery(id+"F16.wireOp",EDGE,"E209"),sQuery(id+"F16.wireOp",EDGE,"E210"),sQuery(id+"F16.wireOp",EDGE,"E211"),sQuery(id+"F16.wireOp",EDGE,"E212"),sQuery(id+"F16.wireOp",EDGE,"E213"),sQuery(id+"F16.wireOp",EDGE,"E214"),sQuery(id+"F16.wireOp",EDGE,"E215"),sQuery(id+"F16.wireOp",EDGE,"E216"),sQuery(id+"F16.wireOp",EDGE,"E217"),sQuery(id+"F16.wireOp",EDGE,"E218"),sQuery(id+"F16.wireOp",EDGE,"E219"),sQuery(id+"F16.wireOp",EDGE,"E220"),sQuery(id+"F16.wireOp",EDGE,"E221"),sQuery(id+"F16.wireOp",EDGE,"E222"),sQuery(id+"F16.wireOp",EDGE,"E223"),sQuery(id+"F16.wireOp",EDGE,"E224"),sQuery(id+"F16.wireOp",EDGE,"E225"),sQuery(id+"F16.wireOp",EDGE,"E226"),sQuery(id+"F16.wireOp",EDGE,"E227"),sQuery(id+"F16.wireOp",EDGE,"E228"),sQuery(id+"F16.wireOp",EDGE,"E229"),sQuery(id+"F16.wireOp",EDGE,"E230"),sQuery(id+"F16.wireOp",EDGE,"E231"),sQuery(id+"F16.wireOp",EDGE,"E232"),sQuery(id+"F16.wireOp",EDGE,"E233"),sQuery(id+"F16.wireOp",EDGE,"E234")])]});
            var Q2;
            Q2=makeQuery(id+"F17.opExtrude","SWEPT_BODY",BODY,{"disambiguationData":[OSD([sQuery(id+"F16.wireOp",EDGE,"E235"),sQuery(id+"F16.wireOp",EDGE,"E236"),sQuery(id+"F16.wireOp",EDGE,"E237"),sQuery(id+"F16.wireOp",EDGE,"E238"),sQuery(id+"F16.wireOp",EDGE,"E239"),sQuery(id+"F16.wireOp",EDGE,"E240"),sQuery(id+"F16.wireOp",EDGE,"E241"),sQuery(id+"F16.wireOp",EDGE,"E242"),sQuery(id+"F16.wireOp",EDGE,"E243"),sQuery(id+"F16.wireOp",EDGE,"E244"),sQuery(id+"F16.wireOp",EDGE,"E245"),sQuery(id+"F16.wireOp",EDGE,"E246"),sQuery(id+"F16.wireOp",EDGE,"E247"),sQuery(id+"F16.wireOp",EDGE,"E248"),sQuery(id+"F16.wireOp",EDGE,"E249"),sQuery(id+"F16.wireOp",EDGE,"E250"),sQuery(id+"F16.wireOp",EDGE,"E251"),sQuery(id+"F16.wireOp",EDGE,"E252"),sQuery(id+"F16.wireOp",EDGE,"E253"),sQuery(id+"F16.wireOp",EDGE,"E254"),sQuery(id+"F16.wireOp",EDGE,"E255"),sQuery(id+"F16.wireOp",EDGE,"E256"),sQuery(id+"F16.wireOp",EDGE,"E257"),sQuery(id+"F16.wireOp",EDGE,"E258"),sQuery(id+"F16.wireOp",EDGE,"E259"),sQuery(id+"F16.wireOp",EDGE,"E260"),sQuery(id+"F16.wireOp",EDGE,"E261"),sQuery(id+"F16.wireOp",EDGE,"E262"),sQuery(id+"F16.wireOp",EDGE,"E263"),sQuery(id+"F16.wireOp",EDGE,"E264"),sQuery(id+"F16.wireOp",EDGE,"E265"),sQuery(id+"F16.wireOp",EDGE,"E266"),sQuery(id+"F16.wireOp",EDGE,"E267"),sQuery(id+"F16.wireOp",EDGE,"E268"),sQuery(id+"F16.wireOp",EDGE,"E269"),sQuery(id+"F16.wireOp",EDGE,"E270"),sQuery(id+"F16.wireOp",EDGE,"E271"),sQuery(id+"F16.wireOp",EDGE,"E272"),sQuery(id+"F16.wireOp",EDGE,"E273"),sQuery(id+"F16.wireOp",EDGE,"E274")])]});
            var Q3;
            Q3=makeQuery(id+"F17.opExtrude","SWEPT_BODY",BODY,{"disambiguationData":[OSD([sQuery(id+"F16.wireOp",EDGE,"E275"),sQuery(id+"F16.wireOp",EDGE,"E276"),sQuery(id+"F16.wireOp",EDGE,"E277"),sQuery(id+"F16.wireOp",EDGE,"E278"),sQuery(id+"F16.wireOp",EDGE,"E279"),sQuery(id+"F16.wireOp",EDGE,"E280"),sQuery(id+"F16.wireOp",EDGE,"E281"),sQuery(id+"F16.wireOp",EDGE,"E282"),sQuery(id+"F16.wireOp",EDGE,"E283"),sQuery(id+"F16.wireOp",EDGE,"E284"),sQuery(id+"F16.wireOp",EDGE,"E285"),sQuery(id+"F16.wireOp",EDGE,"E286"),sQuery(id+"F16.wireOp",EDGE,"E287"),sQuery(id+"F16.wireOp",EDGE,"E288"),sQuery(id+"F16.wireOp",EDGE,"E289"),sQuery(id+"F16.wireOp",EDGE,"E290"),sQuery(id+"F16.wireOp",EDGE,"E291"),sQuery(id+"F16.wireOp",EDGE,"E292"),sQuery(id+"F16.wireOp",EDGE,"E293"),sQuery(id+"F16.wireOp",EDGE,"E294"),sQuery(id+"F16.wireOp",EDGE,"E295"),sQuery(id+"F16.wireOp",EDGE,"E296"),sQuery(id+"F16.wireOp",EDGE,"E297"),sQuery(id+"F16.wireOp",EDGE,"E298"),sQuery(id+"F16.wireOp",EDGE,"E299")])]});
            var Q4;
            Q4=makeQuery(id+"F17.opExtrude","SWEPT_BODY",BODY,{"disambiguationData":[OSD([sQuery(id+"F16.wireOp",EDGE,"E300"),sQuery(id+"F16.wireOp",EDGE,"E301"),sQuery(id+"F16.wireOp",EDGE,"E302"),sQuery(id+"F16.wireOp",EDGE,"E303"),sQuery(id+"F16.wireOp",EDGE,"E304"),sQuery(id+"F16.wireOp",EDGE,"E305"),sQuery(id+"F16.wireOp",EDGE,"E306"),sQuery(id+"F16.wireOp",EDGE,"E307"),sQuery(id+"F16.wireOp",EDGE,"E308"),sQuery(id+"F16.wireOp",EDGE,"E309"),sQuery(id+"F16.wireOp",EDGE,"E310"),sQuery(id+"F16.wireOp",EDGE,"E311"),sQuery(id+"F16.wireOp",EDGE,"E312"),sQuery(id+"F16.wireOp",EDGE,"E313"),sQuery(id+"F16.wireOp",EDGE,"E314"),sQuery(id+"F16.wireOp",EDGE,"E315"),sQuery(id+"F16.wireOp",EDGE,"E316"),sQuery(id+"F16.wireOp",EDGE,"E317"),sQuery(id+"F16.wireOp",EDGE,"E318"),sQuery(id+"F16.wireOp",EDGE,"E319"),sQuery(id+"F16.wireOp",EDGE,"E320"),sQuery(id+"F16.wireOp",EDGE,"E321"),sQuery(id+"F16.wireOp",EDGE,"E322"),sQuery(id+"F16.wireOp",EDGE,"E323"),sQuery(id+"F16.wireOp",EDGE,"E324"),sQuery(id+"F16.wireOp",EDGE,"E325"),sQuery(id+"F16.wireOp",EDGE,"E326"),sQuery(id+"F16.wireOp",EDGE,"E327"),sQuery(id+"F16.wireOp",EDGE,"E328"),sQuery(id+"F16.wireOp",EDGE,"E329"),sQuery(id+"F16.wireOp",EDGE,"E330"),sQuery(id+"F16.wireOp",EDGE,"E331"),sQuery(id+"F16.wireOp",EDGE,"E332"),sQuery(id+"F16.wireOp",EDGE,"E333"),sQuery(id+"F16.wireOp",EDGE,"E334"),sQuery(id+"F16.wireOp",EDGE,"E335"),sQuery(id+"F16.wireOp",EDGE,"E336"),sQuery(id+"F16.wireOp",EDGE,"E337"),sQuery(id+"F16.wireOp",EDGE,"E338"),sQuery(id+"F16.wireOp",EDGE,"E339"),sQuery(id+"F16.wireOp",EDGE,"E340"),sQuery(id+"F16.wireOp",EDGE,"E341"),sQuery(id+"F16.wireOp",EDGE,"E342"),sQuery(id+"F16.wireOp",EDGE,"E343"),sQuery(id+"F16.wireOp",EDGE,"E344"),sQuery(id+"F16.wireOp",EDGE,"E345"),sQuery(id+"F16.wireOp",EDGE,"E346"),sQuery(id+"F16.wireOp",EDGE,"E347"),sQuery(id+"F16.wireOp",EDGE,"E348"),sQuery(id+"F16.wireOp",EDGE,"E349"),sQuery(id+"F16.wireOp",EDGE,"E350"),sQuery(id+"F16.wireOp",EDGE,"E351"),sQuery(id+"F16.wireOp",EDGE,"E352"),sQuery(id+"F16.wireOp",EDGE,"E353")])]});
            var Q5;
            Q5=makeQuery(id+"F17.opExtrude","SWEPT_BODY",BODY,{"disambiguationData":[OSD([sQuery(id+"F16.wireOp",EDGE,"E354"),sQuery(id+"F16.wireOp",EDGE,"E355"),sQuery(id+"F16.wireOp",EDGE,"E356"),sQuery(id+"F16.wireOp",EDGE,"E357"),sQuery(id+"F16.wireOp",EDGE,"E358"),sQuery(id+"F16.wireOp",EDGE,"E359"),sQuery(id+"F16.wireOp",EDGE,"E360"),sQuery(id+"F16.wireOp",EDGE,"E361"),sQuery(id+"F16.wireOp",EDGE,"E362"),sQuery(id+"F16.wireOp",EDGE,"E363"),sQuery(id+"F16.wireOp",EDGE,"E364"),sQuery(id+"F16.wireOp",EDGE,"E365"),sQuery(id+"F16.wireOp",EDGE,"E366"),sQuery(id+"F16.wireOp",EDGE,"E367"),sQuery(id+"F16.wireOp",EDGE,"E368"),sQuery(id+"F16.wireOp",EDGE,"E369"),sQuery(id+"F16.wireOp",EDGE,"E370"),sQuery(id+"F16.wireOp",EDGE,"E371"),sQuery(id+"F16.wireOp",EDGE,"E372"),sQuery(id+"F16.wireOp",EDGE,"E373"),sQuery(id+"F16.wireOp",EDGE,"E374"),sQuery(id+"F16.wireOp",EDGE,"E375"),sQuery(id+"F16.wireOp",EDGE,"E376"),sQuery(id+"F16.wireOp",EDGE,"E377"),sQuery(id+"F16.wireOp",EDGE,"E378"),sQuery(id+"F16.wireOp",EDGE,"E379"),sQuery(id+"F16.wireOp",EDGE,"E380"),sQuery(id+"F16.wireOp",EDGE,"E381"),sQuery(id+"F16.wireOp",EDGE,"E382"),sQuery(id+"F16.wireOp",EDGE,"E383"),sQuery(id+"F16.wireOp",EDGE,"E384"),sQuery(id+"F16.wireOp",EDGE,"E385"),sQuery(id+"F16.wireOp",EDGE,"E386"),sQuery(id+"F16.wireOp",EDGE,"E387"),sQuery(id+"F16.wireOp",EDGE,"E388"),sQuery(id+"F16.wireOp",EDGE,"E389"),sQuery(id+"F16.wireOp",EDGE,"E390"),sQuery(id+"F16.wireOp",EDGE,"E391"),sQuery(id+"F16.wireOp",EDGE,"E392"),sQuery(id+"F16.wireOp",EDGE,"E393"),sQuery(id+"F16.wireOp",EDGE,"E394"),sQuery(id+"F16.wireOp",EDGE,"E395"),sQuery(id+"F16.wireOp",EDGE,"E396"),sQuery(id+"F16.wireOp",EDGE,"E397"),sQuery(id+"F16.wireOp",EDGE,"E398"),sQuery(id+"F16.wireOp",EDGE,"E399"),sQuery(id+"F16.wireOp",EDGE,"E400"),sQuery(id+"F16.wireOp",EDGE,"E401"),sQuery(id+"F16.wireOp",EDGE,"E402"),sQuery(id+"F16.wireOp",EDGE,"E403"),sQuery(id+"F16.wireOp",EDGE,"E404"),sQuery(id+"F16.wireOp",EDGE,"E405"),sQuery(id+"F16.wireOp",EDGE,"E406"),sQuery(id+"F16.wireOp",EDGE,"E407"),sQuery(id+"F16.wireOp",EDGE,"E408"),sQuery(id+"F16.wireOp",EDGE,"E409"),sQuery(id+"F16.wireOp",EDGE,"E410"),sQuery(id+"F16.wireOp",EDGE,"E411"),sQuery(id+"F16.wireOp",EDGE,"E412"),sQuery(id+"F16.wireOp",EDGE,"E413"),sQuery(id+"F16.wireOp",EDGE,"E414"),sQuery(id+"F16.wireOp",EDGE,"E415"),sQuery(id+"F16.wireOp",EDGE,"E416"),sQuery(id+"F16.wireOp",EDGE,"E417"),sQuery(id+"F16.wireOp",EDGE,"E418"),sQuery(id+"F16.wireOp",EDGE,"E419"),sQuery(id+"F16.wireOp",EDGE,"E420"),sQuery(id+"F16.wireOp",EDGE,"E421"),sQuery(id+"F16.wireOp",EDGE,"E422"),sQuery(id+"F16.wireOp",EDGE,"E423"),sQuery(id+"F16.wireOp",EDGE,"E424"),sQuery(id+"F16.wireOp",EDGE,"E425"),sQuery(id+"F16.wireOp",EDGE,"E426"),sQuery(id+"F16.wireOp",EDGE,"E427"),sQuery(id+"F16.wireOp",EDGE,"E428"),sQuery(id+"F16.wireOp",EDGE,"E429"),sQuery(id+"F16.wireOp",EDGE,"E430"),sQuery(id+"F16.wireOp",EDGE,"E431")])]});
            var Q6;
            Q6=makeQuery(id+"F17.opExtrude","SWEPT_BODY",BODY,{"disambiguationData":[OSD([sQuery(id+"F16.wireOp",EDGE,"E432"),sQuery(id+"F16.wireOp",EDGE,"E433"),sQuery(id+"F16.wireOp",EDGE,"E434"),sQuery(id+"F16.wireOp",EDGE,"E435"),sQuery(id+"F16.wireOp",EDGE,"E436"),sQuery(id+"F16.wireOp",EDGE,"E437"),sQuery(id+"F16.wireOp",EDGE,"E438"),sQuery(id+"F16.wireOp",EDGE,"E439"),sQuery(id+"F16.wireOp",EDGE,"E440"),sQuery(id+"F16.wireOp",EDGE,"E441"),sQuery(id+"F16.wireOp",EDGE,"E442"),sQuery(id+"F16.wireOp",EDGE,"E443"),sQuery(id+"F16.wireOp",EDGE,"E444"),sQuery(id+"F16.wireOp",EDGE,"E445"),sQuery(id+"F16.wireOp",EDGE,"E446"),sQuery(id+"F16.wireOp",EDGE,"E447"),sQuery(id+"F16.wireOp",EDGE,"E448"),sQuery(id+"F16.wireOp",EDGE,"E449"),sQuery(id+"F16.wireOp",EDGE,"E450"),sQuery(id+"F16.wireOp",EDGE,"E451"),sQuery(id+"F16.wireOp",EDGE,"E452"),sQuery(id+"F16.wireOp",EDGE,"E453"),sQuery(id+"F16.wireOp",EDGE,"E454"),sQuery(id+"F16.wireOp",EDGE,"E455"),sQuery(id+"F16.wireOp",EDGE,"E456"),sQuery(id+"F16.wireOp",EDGE,"E457"),sQuery(id+"F16.wireOp",EDGE,"E458"),sQuery(id+"F16.wireOp",EDGE,"E459"),sQuery(id+"F16.wireOp",EDGE,"E460"),sQuery(id+"F16.wireOp",EDGE,"E461"),sQuery(id+"F16.wireOp",EDGE,"E462"),sQuery(id+"F16.wireOp",EDGE,"E463"),sQuery(id+"F16.wireOp",EDGE,"E464"),sQuery(id+"F16.wireOp",EDGE,"E465"),sQuery(id+"F16.wireOp",EDGE,"E466"),sQuery(id+"F16.wireOp",EDGE,"E467"),sQuery(id+"F16.wireOp",EDGE,"E468"),sQuery(id+"F16.wireOp",EDGE,"E469"),sQuery(id+"F16.wireOp",EDGE,"E470"),sQuery(id+"F16.wireOp",EDGE,"E471"),sQuery(id+"F16.wireOp",EDGE,"E472"),sQuery(id+"F16.wireOp",EDGE,"E473"),sQuery(id+"F16.wireOp",EDGE,"E474"),sQuery(id+"F16.wireOp",EDGE,"E475"),sQuery(id+"F16.wireOp",EDGE,"E476"),sQuery(id+"F16.wireOp",EDGE,"E477")])]});
            var Q7;
            Q7=makeQuery(id+"F17.opExtrude","SWEPT_BODY",BODY,{"disambiguationData":[OSD([sQuery(id+"F16.wireOp",EDGE,"E478"),sQuery(id+"F16.wireOp",EDGE,"E479"),sQuery(id+"F16.wireOp",EDGE,"E480"),sQuery(id+"F16.wireOp",EDGE,"E481"),sQuery(id+"F16.wireOp",EDGE,"E482"),sQuery(id+"F16.wireOp",EDGE,"E483"),sQuery(id+"F16.wireOp",EDGE,"E484"),sQuery(id+"F16.wireOp",EDGE,"E485"),sQuery(id+"F16.wireOp",EDGE,"E486"),sQuery(id+"F16.wireOp",EDGE,"E487"),sQuery(id+"F16.wireOp",EDGE,"E488"),sQuery(id+"F16.wireOp",EDGE,"E489"),sQuery(id+"F16.wireOp",EDGE,"E490"),sQuery(id+"F16.wireOp",EDGE,"E491"),sQuery(id+"F16.wireOp",EDGE,"E492"),sQuery(id+"F16.wireOp",EDGE,"E493"),sQuery(id+"F16.wireOp",EDGE,"E494"),sQuery(id+"F16.wireOp",EDGE,"E495"),sQuery(id+"F16.wireOp",EDGE,"E496"),sQuery(id+"F16.wireOp",EDGE,"E497"),sQuery(id+"F16.wireOp",EDGE,"E498"),sQuery(id+"F16.wireOp",EDGE,"E499"),sQuery(id+"F16.wireOp",EDGE,"E500"),sQuery(id+"F16.wireOp",EDGE,"E501"),sQuery(id+"F16.wireOp",EDGE,"E502"),sQuery(id+"F16.wireOp",EDGE,"E503"),sQuery(id+"F16.wireOp",EDGE,"E504"),sQuery(id+"F16.wireOp",EDGE,"E505"),sQuery(id+"F16.wireOp",EDGE,"E506"),sQuery(id+"F16.wireOp",EDGE,"E507"),sQuery(id+"F16.wireOp",EDGE,"E508"),sQuery(id+"F16.wireOp",EDGE,"E509"),sQuery(id+"F16.wireOp",EDGE,"E510"),sQuery(id+"F16.wireOp",EDGE,"E511"),sQuery(id+"F16.wireOp",EDGE,"E512"),sQuery(id+"F16.wireOp",EDGE,"E513"),sQuery(id+"F16.wireOp",EDGE,"E514"),sQuery(id+"F16.wireOp",EDGE,"E515"),sQuery(id+"F16.wireOp",EDGE,"E516"),sQuery(id+"F16.wireOp",EDGE,"E517"),sQuery(id+"F16.wireOp",EDGE,"E518"),sQuery(id+"F16.wireOp",EDGE,"E519"),sQuery(id+"F16.wireOp",EDGE,"E520"),sQuery(id+"F16.wireOp",EDGE,"E521"),sQuery(id+"F16.wireOp",EDGE,"E522"),sQuery(id+"F16.wireOp",EDGE,"E523"),sQuery(id+"F16.wireOp",EDGE,"E524"),sQuery(id+"F16.wireOp",EDGE,"E525"),sQuery(id+"F16.wireOp",EDGE,"E526"),sQuery(id+"F16.wireOp",EDGE,"E527"),sQuery(id+"F16.wireOp",EDGE,"E528"),sQuery(id+"F16.wireOp",EDGE,"E529"),sQuery(id+"F16.wireOp",EDGE,"E530"),sQuery(id+"F16.wireOp",EDGE,"E531"),sQuery(id+"F16.wireOp",EDGE,"E532"),sQuery(id+"F16.wireOp",EDGE,"E533"),sQuery(id+"F16.wireOp",EDGE,"E534")])]});
            var Q8;
            Q8=makeQuery(id+"F17.opExtrude","SWEPT_BODY",BODY,{"disambiguationData":[OSD([sQuery(id+"F16.wireOp",EDGE,"E535"),sQuery(id+"F16.wireOp",EDGE,"E536"),sQuery(id+"F16.wireOp",EDGE,"E537"),sQuery(id+"F16.wireOp",EDGE,"E538"),sQuery(id+"F16.wireOp",EDGE,"E539"),sQuery(id+"F16.wireOp",EDGE,"E540"),sQuery(id+"F16.wireOp",EDGE,"E541"),sQuery(id+"F16.wireOp",EDGE,"E542"),sQuery(id+"F16.wireOp",EDGE,"E543"),sQuery(id+"F16.wireOp",EDGE,"E544"),sQuery(id+"F16.wireOp",EDGE,"E545"),sQuery(id+"F16.wireOp",EDGE,"E546"),sQuery(id+"F16.wireOp",EDGE,"E547"),sQuery(id+"F16.wireOp",EDGE,"E548"),sQuery(id+"F16.wireOp",EDGE,"E549"),sQuery(id+"F16.wireOp",EDGE,"E550"),sQuery(id+"F16.wireOp",EDGE,"E551"),sQuery(id+"F16.wireOp",EDGE,"E552"),sQuery(id+"F16.wireOp",EDGE,"E553"),sQuery(id+"F16.wireOp",EDGE,"E554"),sQuery(id+"F16.wireOp",EDGE,"E555"),sQuery(id+"F16.wireOp",EDGE,"E556"),sQuery(id+"F16.wireOp",EDGE,"E557"),sQuery(id+"F16.wireOp",EDGE,"E558")])]});
            var Q9;
            Q9=makeQuery(id+"F17.opExtrude","SWEPT_BODY",BODY,{"disambiguationData":[OSD([sQuery(id+"F16.wireOp",EDGE,"E559"),sQuery(id+"F16.wireOp",EDGE,"E560"),sQuery(id+"F16.wireOp",EDGE,"E561"),sQuery(id+"F16.wireOp",EDGE,"E562"),sQuery(id+"F16.wireOp",EDGE,"E563"),sQuery(id+"F16.wireOp",EDGE,"E564"),sQuery(id+"F16.wireOp",EDGE,"E565"),sQuery(id+"F16.wireOp",EDGE,"E566"),sQuery(id+"F16.wireOp",EDGE,"E567"),sQuery(id+"F16.wireOp",EDGE,"E568"),sQuery(id+"F16.wireOp",EDGE,"E569"),sQuery(id+"F16.wireOp",EDGE,"E570"),sQuery(id+"F16.wireOp",EDGE,"E571"),sQuery(id+"F16.wireOp",EDGE,"E572"),sQuery(id+"F16.wireOp",EDGE,"E573"),sQuery(id+"F16.wireOp",EDGE,"E574"),sQuery(id+"F16.wireOp",EDGE,"E575"),sQuery(id+"F16.wireOp",EDGE,"E576"),sQuery(id+"F16.wireOp",EDGE,"E577"),sQuery(id+"F16.wireOp",EDGE,"E578"),sQuery(id+"F16.wireOp",EDGE,"E579"),sQuery(id+"F16.wireOp",EDGE,"E580"),sQuery(id+"F16.wireOp",EDGE,"E581"),sQuery(id+"F16.wireOp",EDGE,"E582"),sQuery(id+"F16.wireOp",EDGE,"E583"),sQuery(id+"F16.wireOp",EDGE,"E584"),sQuery(id+"F16.wireOp",EDGE,"E585"),sQuery(id+"F16.wireOp",EDGE,"E586"),sQuery(id+"F16.wireOp",EDGE,"E587"),sQuery(id+"F16.wireOp",EDGE,"E588"),sQuery(id+"F16.wireOp",EDGE,"E589"),sQuery(id+"F16.wireOp",EDGE,"E590"),sQuery(id+"F16.wireOp",EDGE,"E591"),sQuery(id+"F16.wireOp",EDGE,"E592")])]});
            var Q10;
            Q10=makeQuery(id+"F17.opExtrude","SWEPT_BODY",BODY,{"disambiguationData":[OSD([sQuery(id+"F16.wireOp",EDGE,"E593"),sQuery(id+"F16.wireOp",EDGE,"E594"),sQuery(id+"F16.wireOp",EDGE,"E595"),sQuery(id+"F16.wireOp",EDGE,"E596"),sQuery(id+"F16.wireOp",EDGE,"E597"),sQuery(id+"F16.wireOp",EDGE,"E598"),sQuery(id+"F16.wireOp",EDGE,"E599"),sQuery(id+"F16.wireOp",EDGE,"E600"),sQuery(id+"F16.wireOp",EDGE,"E601"),sQuery(id+"F16.wireOp",EDGE,"E602"),sQuery(id+"F16.wireOp",EDGE,"E603"),sQuery(id+"F16.wireOp",EDGE,"E604"),sQuery(id+"F16.wireOp",EDGE,"E605"),sQuery(id+"F16.wireOp",EDGE,"E606"),sQuery(id+"F16.wireOp",EDGE,"E607"),sQuery(id+"F16.wireOp",EDGE,"E608"),sQuery(id+"F16.wireOp",EDGE,"E609"),sQuery(id+"F16.wireOp",EDGE,"E610"),sQuery(id+"F16.wireOp",EDGE,"E611"),sQuery(id+"F16.wireOp",EDGE,"E612"),sQuery(id+"F16.wireOp",EDGE,"E613"),sQuery(id+"F16.wireOp",EDGE,"E614"),sQuery(id+"F16.wireOp",EDGE,"E615"),sQuery(id+"F16.wireOp",EDGE,"E616"),sQuery(id+"F16.wireOp",EDGE,"E617"),sQuery(id+"F16.wireOp",EDGE,"E618"),sQuery(id+"F16.wireOp",EDGE,"E619"),sQuery(id+"F16.wireOp",EDGE,"E620"),sQuery(id+"F16.wireOp",EDGE,"E621"),sQuery(id+"F16.wireOp",EDGE,"E622"),sQuery(id+"F16.wireOp",EDGE,"E623"),sQuery(id+"F16.wireOp",EDGE,"E624"),sQuery(id+"F16.wireOp",EDGE,"E625"),sQuery(id+"F16.wireOp",EDGE,"E626"),sQuery(id+"F16.wireOp",EDGE,"E627"),sQuery(id+"F16.wireOp",EDGE,"E628"),sQuery(id+"F16.wireOp",EDGE,"E629"),sQuery(id+"F16.wireOp",EDGE,"E630"),sQuery(id+"F16.wireOp",EDGE,"E631")])]});
            var Q11;
            Q11=makeQuery(id+"F17.opExtrude","SWEPT_BODY",BODY,{"disambiguationData":[OSD([sQuery(id+"F16.wireOp",EDGE,"E632"),sQuery(id+"F16.wireOp",EDGE,"E633"),sQuery(id+"F16.wireOp",EDGE,"E634"),sQuery(id+"F16.wireOp",EDGE,"E635"),sQuery(id+"F16.wireOp",EDGE,"E636"),sQuery(id+"F16.wireOp",EDGE,"E637"),sQuery(id+"F16.wireOp",EDGE,"E638"),sQuery(id+"F16.wireOp",EDGE,"E639"),sQuery(id+"F16.wireOp",EDGE,"E640"),sQuery(id+"F16.wireOp",EDGE,"E641"),sQuery(id+"F16.wireOp",EDGE,"E642"),sQuery(id+"F16.wireOp",EDGE,"E643"),sQuery(id+"F16.wireOp",EDGE,"E644"),sQuery(id+"F16.wireOp",EDGE,"E645"),sQuery(id+"F16.wireOp",EDGE,"E646"),sQuery(id+"F16.wireOp",EDGE,"E647"),sQuery(id+"F16.wireOp",EDGE,"E648"),sQuery(id+"F16.wireOp",EDGE,"E649"),sQuery(id+"F16.wireOp",EDGE,"E650"),sQuery(id+"F16.wireOp",EDGE,"E651"),sQuery(id+"F16.wireOp",EDGE,"E652"),sQuery(id+"F16.wireOp",EDGE,"E653"),sQuery(id+"F16.wireOp",EDGE,"E654"),sQuery(id+"F16.wireOp",EDGE,"E655"),sQuery(id+"F16.wireOp",EDGE,"E656"),sQuery(id+"F16.wireOp",EDGE,"E657"),sQuery(id+"F16.wireOp",EDGE,"E658"),sQuery(id+"F16.wireOp",EDGE,"E659"),sQuery(id+"F16.wireOp",EDGE,"E660"),sQuery(id+"F16.wireOp",EDGE,"E661"),sQuery(id+"F16.wireOp",EDGE,"E662"),sQuery(id+"F16.wireOp",EDGE,"E663"),sQuery(id+"F16.wireOp",EDGE,"E664"),sQuery(id+"F16.wireOp",EDGE,"E665"),sQuery(id+"F16.wireOp",EDGE,"E666"),sQuery(id+"F16.wireOp",EDGE,"E667"),sQuery(id+"F16.wireOp",EDGE,"E668"),sQuery(id+"F16.wireOp",EDGE,"E669"),sQuery(id+"F16.wireOp",EDGE,"E670"),sQuery(id+"F16.wireOp",EDGE,"E671"),sQuery(id+"F16.wireOp",EDGE,"E672"),sQuery(id+"F16.wireOp",EDGE,"E673"),sQuery(id+"F16.wireOp",EDGE,"E674"),sQuery(id+"F16.wireOp",EDGE,"E675"),sQuery(id+"F16.wireOp",EDGE,"E676"),sQuery(id+"F16.wireOp",EDGE,"E677"),sQuery(id+"F16.wireOp",EDGE,"E678"),sQuery(id+"F16.wireOp",EDGE,"E679"),sQuery(id+"F16.wireOp",EDGE,"E680"),sQuery(id+"F16.wireOp",EDGE,"E681"),sQuery(id+"F16.wireOp",EDGE,"E682"),sQuery(id+"F16.wireOp",EDGE,"E683"),sQuery(id+"F16.wireOp",EDGE,"E684"),sQuery(id+"F16.wireOp",EDGE,"E685"),sQuery(id+"F16.wireOp",EDGE,"E686"),sQuery(id+"F16.wireOp",EDGE,"E687"),sQuery(id+"F16.wireOp",EDGE,"E688"),sQuery(id+"F16.wireOp",EDGE,"E689"),sQuery(id+"F16.wireOp",EDGE,"E690"),sQuery(id+"F16.wireOp",EDGE,"E691"),sQuery(id+"F16.wireOp",EDGE,"E692"),sQuery(id+"F16.wireOp",EDGE,"E693"),sQuery(id+"F16.wireOp",EDGE,"E694"),sQuery(id+"F16.wireOp",EDGE,"E695")])]});
            var Q12;
            Q12=makeQuery(id+"F17.opExtrude","SWEPT_BODY",BODY,{"disambiguationData":[OSD([sQuery(id+"F16.wireOp",EDGE,"E696"),sQuery(id+"F16.wireOp",EDGE,"E697"),sQuery(id+"F16.wireOp",EDGE,"E698"),sQuery(id+"F16.wireOp",EDGE,"E699"),sQuery(id+"F16.wireOp",EDGE,"E700"),sQuery(id+"F16.wireOp",EDGE,"E701"),sQuery(id+"F16.wireOp",EDGE,"E702"),sQuery(id+"F16.wireOp",EDGE,"E703"),sQuery(id+"F16.wireOp",EDGE,"E704"),sQuery(id+"F16.wireOp",EDGE,"E705"),sQuery(id+"F16.wireOp",EDGE,"E706"),sQuery(id+"F16.wireOp",EDGE,"E707"),sQuery(id+"F16.wireOp",EDGE,"E708"),sQuery(id+"F16.wireOp",EDGE,"E709"),sQuery(id+"F16.wireOp",EDGE,"E710"),sQuery(id+"F16.wireOp",EDGE,"E711"),sQuery(id+"F16.wireOp",EDGE,"E712"),sQuery(id+"F16.wireOp",EDGE,"E713"),sQuery(id+"F16.wireOp",EDGE,"E714"),sQuery(id+"F16.wireOp",EDGE,"E715"),sQuery(id+"F16.wireOp",EDGE,"E716"),sQuery(id+"F16.wireOp",EDGE,"E717"),sQuery(id+"F16.wireOp",EDGE,"E718"),sQuery(id+"F16.wireOp",EDGE,"E719"),sQuery(id+"F16.wireOp",EDGE,"E720"),sQuery(id+"F16.wireOp",EDGE,"E721"),sQuery(id+"F16.wireOp",EDGE,"E722"),sQuery(id+"F16.wireOp",EDGE,"E723"),sQuery(id+"F16.wireOp",EDGE,"E724"),sQuery(id+"F16.wireOp",EDGE,"E725"),sQuery(id+"F16.wireOp",EDGE,"E726"),sQuery(id+"F16.wireOp",EDGE,"E727"),sQuery(id+"F16.wireOp",EDGE,"E728"),sQuery(id+"F16.wireOp",EDGE,"E729"),sQuery(id+"F16.wireOp",EDGE,"E730"),sQuery(id+"F16.wireOp",EDGE,"E731"),sQuery(id+"F16.wireOp",EDGE,"E732"),sQuery(id+"F16.wireOp",EDGE,"E733"),sQuery(id+"F16.wireOp",EDGE,"E734"),sQuery(id+"F16.wireOp",EDGE,"E735"),sQuery(id+"F16.wireOp",EDGE,"E736"),sQuery(id+"F16.wireOp",EDGE,"E737"),sQuery(id+"F16.wireOp",EDGE,"E738"),sQuery(id+"F16.wireOp",EDGE,"E739"),sQuery(id+"F16.wireOp",EDGE,"E740"),sQuery(id+"F16.wireOp",EDGE,"E741"),sQuery(id+"F16.wireOp",EDGE,"E742"),sQuery(id+"F16.wireOp",EDGE,"E743"),sQuery(id+"F16.wireOp",EDGE,"E744"),sQuery(id+"F16.wireOp",EDGE,"E745"),sQuery(id+"F16.wireOp",EDGE,"E746"),sQuery(id+"F16.wireOp",EDGE,"E747"),sQuery(id+"F16.wireOp",EDGE,"E748"),sQuery(id+"F16.wireOp",EDGE,"E749")])]});
            var Q13;
            Q13=makeQuery(id+"F17.opExtrude","SWEPT_BODY",BODY,{"disambiguationData":[OSD([sQuery(id+"F16.wireOp",EDGE,"E750"),sQuery(id+"F16.wireOp",EDGE,"E751"),sQuery(id+"F16.wireOp",EDGE,"E752"),sQuery(id+"F16.wireOp",EDGE,"E753"),sQuery(id+"F16.wireOp",EDGE,"E754"),sQuery(id+"F16.wireOp",EDGE,"E755"),sQuery(id+"F16.wireOp",EDGE,"E756"),sQuery(id+"F16.wireOp",EDGE,"E757"),sQuery(id+"F16.wireOp",EDGE,"E758"),sQuery(id+"F16.wireOp",EDGE,"E759"),sQuery(id+"F16.wireOp",EDGE,"E760"),sQuery(id+"F16.wireOp",EDGE,"E761"),sQuery(id+"F16.wireOp",EDGE,"E762"),sQuery(id+"F16.wireOp",EDGE,"E763"),sQuery(id+"F16.wireOp",EDGE,"E764"),sQuery(id+"F16.wireOp",EDGE,"E765"),sQuery(id+"F16.wireOp",EDGE,"E766"),sQuery(id+"F16.wireOp",EDGE,"E767"),sQuery(id+"F16.wireOp",EDGE,"E768"),sQuery(id+"F16.wireOp",EDGE,"E769"),sQuery(id+"F16.wireOp",EDGE,"E770"),sQuery(id+"F16.wireOp",EDGE,"E771"),sQuery(id+"F16.wireOp",EDGE,"E772"),sQuery(id+"F16.wireOp",EDGE,"E773"),sQuery(id+"F16.wireOp",EDGE,"E774"),sQuery(id+"F16.wireOp",EDGE,"E775"),sQuery(id+"F16.wireOp",EDGE,"E776"),sQuery(id+"F16.wireOp",EDGE,"E777"),sQuery(id+"F16.wireOp",EDGE,"E778"),sQuery(id+"F16.wireOp",EDGE,"E779"),sQuery(id+"F16.wireOp",EDGE,"E780"),sQuery(id+"F16.wireOp",EDGE,"E781"),sQuery(id+"F16.wireOp",EDGE,"E782"),sQuery(id+"F16.wireOp",EDGE,"E783"),sQuery(id+"F16.wireOp",EDGE,"E784"),sQuery(id+"F16.wireOp",EDGE,"E785"),sQuery(id+"F16.wireOp",EDGE,"E786"),sQuery(id+"F16.wireOp",EDGE,"E787"),sQuery(id+"F16.wireOp",EDGE,"E788"),sQuery(id+"F16.wireOp",EDGE,"E789"),sQuery(id+"F16.wireOp",EDGE,"E790"),sQuery(id+"F16.wireOp",EDGE,"E791"),sQuery(id+"F16.wireOp",EDGE,"E792"),sQuery(id+"F16.wireOp",EDGE,"E793"),sQuery(id+"F16.wireOp",EDGE,"E794"),sQuery(id+"F16.wireOp",EDGE,"E795"),sQuery(id+"F16.wireOp",EDGE,"E796"),sQuery(id+"F16.wireOp",EDGE,"E797"),sQuery(id+"F16.wireOp",EDGE,"E798"),sQuery(id+"F16.wireOp",EDGE,"E799"),sQuery(id+"F16.wireOp",EDGE,"E800"),sQuery(id+"F16.wireOp",EDGE,"E801"),sQuery(id+"F16.wireOp",EDGE,"E802"),sQuery(id+"F16.wireOp",EDGE,"E803"),sQuery(id+"F16.wireOp",EDGE,"E804"),sQuery(id+"F16.wireOp",EDGE,"E805"),sQuery(id+"F16.wireOp",EDGE,"E806"),sQuery(id+"F16.wireOp",EDGE,"E807"),sQuery(id+"F16.wireOp",EDGE,"E808"),sQuery(id+"F16.wireOp",EDGE,"E809"),sQuery(id+"F16.wireOp",EDGE,"E810"),sQuery(id+"F16.wireOp",EDGE,"E811"),sQuery(id+"F16.wireOp",EDGE,"E812"),sQuery(id+"F16.wireOp",EDGE,"E813")])]});
            var Q14;
            Q14=sQuery(id+"F16.wireOp",EDGE,"E814");
            transform(context, id + "F18", {"entities" : qUnion([Q0, Q1, Q2, Q3, Q4, Q5, Q6, Q7, Q8, Q9, Q10, Q11, Q12, Q13]), "transformType" : TransformType.ROTATION, "transformAxis" : qUnion([Q14]), "angle" : 180 * degree, "makeCopy" : false});
        }
        {
            var Q0;
            Q0=makeQuery(id+"F17.opExtrude","SWEPT_BODY",BODY,{"disambiguationData":[OSD([sQuery(id+"F16.wireOp",EDGE,"E47"),sQuery(id+"F16.wireOp",EDGE,"E48"),sQuery(id+"F16.wireOp",EDGE,"E49"),sQuery(id+"F16.wireOp",EDGE,"E50"),sQuery(id+"F16.wireOp",EDGE,"E51"),sQuery(id+"F16.wireOp",EDGE,"E52"),sQuery(id+"F16.wireOp",EDGE,"E53"),sQuery(id+"F16.wireOp",EDGE,"E54"),sQuery(id+"F16.wireOp",EDGE,"E55"),sQuery(id+"F16.wireOp",EDGE,"E56"),sQuery(id+"F16.wireOp",EDGE,"E57"),sQuery(id+"F16.wireOp",EDGE,"E58"),sQuery(id+"F16.wireOp",EDGE,"E59"),sQuery(id+"F16.wireOp",EDGE,"E60"),sQuery(id+"F16.wireOp",EDGE,"E61"),sQuery(id+"F16.wireOp",EDGE,"E62"),sQuery(id+"F16.wireOp",EDGE,"E63"),sQuery(id+"F16.wireOp",EDGE,"E64"),sQuery(id+"F16.wireOp",EDGE,"E65"),sQuery(id+"F16.wireOp",EDGE,"E66"),sQuery(id+"F16.wireOp",EDGE,"E67"),sQuery(id+"F16.wireOp",EDGE,"E68"),sQuery(id+"F16.wireOp",EDGE,"E69"),sQuery(id+"F16.wireOp",EDGE,"E70"),sQuery(id+"F16.wireOp",EDGE,"E71"),sQuery(id+"F16.wireOp",EDGE,"E72"),sQuery(id+"F16.wireOp",EDGE,"E73"),sQuery(id+"F16.wireOp",EDGE,"E74"),sQuery(id+"F16.wireOp",EDGE,"E75"),sQuery(id+"F16.wireOp",EDGE,"E76"),sQuery(id+"F16.wireOp",EDGE,"E77"),sQuery(id+"F16.wireOp",EDGE,"E78"),sQuery(id+"F16.wireOp",EDGE,"E79"),sQuery(id+"F16.wireOp",EDGE,"E80"),sQuery(id+"F16.wireOp",EDGE,"E81"),sQuery(id+"F16.wireOp",EDGE,"E82"),sQuery(id+"F16.wireOp",EDGE,"E83"),sQuery(id+"F16.wireOp",EDGE,"E84"),sQuery(id+"F16.wireOp",EDGE,"E85"),sQuery(id+"F16.wireOp",EDGE,"E86"),sQuery(id+"F16.wireOp",EDGE,"E87"),sQuery(id+"F16.wireOp",EDGE,"E88"),sQuery(id+"F16.wireOp",EDGE,"E89"),sQuery(id+"F16.wireOp",EDGE,"E90"),sQuery(id+"F16.wireOp",EDGE,"E91"),sQuery(id+"F16.wireOp",EDGE,"E92"),sQuery(id+"F16.wireOp",EDGE,"E93"),sQuery(id+"F16.wireOp",EDGE,"E94"),sQuery(id+"F16.wireOp",EDGE,"E95"),sQuery(id+"F16.wireOp",EDGE,"E96"),sQuery(id+"F16.wireOp",EDGE,"E97"),sQuery(id+"F16.wireOp",EDGE,"E98"),sQuery(id+"F16.wireOp",EDGE,"E99"),sQuery(id+"F16.wireOp",EDGE,"E100"),sQuery(id+"F16.wireOp",EDGE,"E101"),sQuery(id+"F16.wireOp",EDGE,"E102"),sQuery(id+"F16.wireOp",EDGE,"E103"),sQuery(id+"F16.wireOp",EDGE,"E104"),sQuery(id+"F16.wireOp",EDGE,"E105"),sQuery(id+"F16.wireOp",EDGE,"E106"),sQuery(id+"F16.wireOp",EDGE,"E107"),sQuery(id+"F16.wireOp",EDGE,"E108"),sQuery(id+"F16.wireOp",EDGE,"E109"),sQuery(id+"F16.wireOp",EDGE,"E110"),sQuery(id+"F16.wireOp",EDGE,"E111"),sQuery(id+"F16.wireOp",EDGE,"E112"),sQuery(id+"F16.wireOp",EDGE,"E113"),sQuery(id+"F16.wireOp",EDGE,"E114"),sQuery(id+"F16.wireOp",EDGE,"E115")])]});
            var Q1;
            Q1=makeQuery(id+"F17.opExtrude","SWEPT_BODY",BODY,{"disambiguationData":[OSD([sQuery(id+"F16.wireOp",EDGE,"E116"),sQuery(id+"F16.wireOp",EDGE,"E117"),sQuery(id+"F16.wireOp",EDGE,"E118"),sQuery(id+"F16.wireOp",EDGE,"E119"),sQuery(id+"F16.wireOp",EDGE,"E120"),sQuery(id+"F16.wireOp",EDGE,"E121"),sQuery(id+"F16.wireOp",EDGE,"E122"),sQuery(id+"F16.wireOp",EDGE,"E123"),sQuery(id+"F16.wireOp",EDGE,"E124"),sQuery(id+"F16.wireOp",EDGE,"E125"),sQuery(id+"F16.wireOp",EDGE,"E126"),sQuery(id+"F16.wireOp",EDGE,"E127"),sQuery(id+"F16.wireOp",EDGE,"E128"),sQuery(id+"F16.wireOp",EDGE,"E129"),sQuery(id+"F16.wireOp",EDGE,"E130"),sQuery(id+"F16.wireOp",EDGE,"E131"),sQuery(id+"F16.wireOp",EDGE,"E132"),sQuery(id+"F16.wireOp",EDGE,"E133"),sQuery(id+"F16.wireOp",EDGE,"E134"),sQuery(id+"F16.wireOp",EDGE,"E135"),sQuery(id+"F16.wireOp",EDGE,"E136"),sQuery(id+"F16.wireOp",EDGE,"E137"),sQuery(id+"F16.wireOp",EDGE,"E138"),sQuery(id+"F16.wireOp",EDGE,"E139"),sQuery(id+"F16.wireOp",EDGE,"E140"),sQuery(id+"F16.wireOp",EDGE,"E141"),sQuery(id+"F16.wireOp",EDGE,"E142"),sQuery(id+"F16.wireOp",EDGE,"E143"),sQuery(id+"F16.wireOp",EDGE,"E144"),sQuery(id+"F16.wireOp",EDGE,"E145"),sQuery(id+"F16.wireOp",EDGE,"E146"),sQuery(id+"F16.wireOp",EDGE,"E147"),sQuery(id+"F16.wireOp",EDGE,"E148"),sQuery(id+"F16.wireOp",EDGE,"E149"),sQuery(id+"F16.wireOp",EDGE,"E150"),sQuery(id+"F16.wireOp",EDGE,"E151"),sQuery(id+"F16.wireOp",EDGE,"E152"),sQuery(id+"F16.wireOp",EDGE,"E153"),sQuery(id+"F16.wireOp",EDGE,"E154"),sQuery(id+"F16.wireOp",EDGE,"E155"),sQuery(id+"F16.wireOp",EDGE,"E156"),sQuery(id+"F16.wireOp",EDGE,"E157"),sQuery(id+"F16.wireOp",EDGE,"E158"),sQuery(id+"F16.wireOp",EDGE,"E159"),sQuery(id+"F16.wireOp",EDGE,"E160"),sQuery(id+"F16.wireOp",EDGE,"E161"),sQuery(id+"F16.wireOp",EDGE,"E162"),sQuery(id+"F16.wireOp",EDGE,"E163"),sQuery(id+"F16.wireOp",EDGE,"E164"),sQuery(id+"F16.wireOp",EDGE,"E165"),sQuery(id+"F16.wireOp",EDGE,"E166"),sQuery(id+"F16.wireOp",EDGE,"E167"),sQuery(id+"F16.wireOp",EDGE,"E168"),sQuery(id+"F16.wireOp",EDGE,"E169"),sQuery(id+"F16.wireOp",EDGE,"E170"),sQuery(id+"F16.wireOp",EDGE,"E171"),sQuery(id+"F16.wireOp",EDGE,"E172"),sQuery(id+"F16.wireOp",EDGE,"E173"),sQuery(id+"F16.wireOp",EDGE,"E174"),sQuery(id+"F16.wireOp",EDGE,"E175"),sQuery(id+"F16.wireOp",EDGE,"E176"),sQuery(id+"F16.wireOp",EDGE,"E177"),sQuery(id+"F16.wireOp",EDGE,"E178"),sQuery(id+"F16.wireOp",EDGE,"E179"),sQuery(id+"F16.wireOp",EDGE,"E180"),sQuery(id+"F16.wireOp",EDGE,"E181"),sQuery(id+"F16.wireOp",EDGE,"E182"),sQuery(id+"F16.wireOp",EDGE,"E183"),sQuery(id+"F16.wireOp",EDGE,"E184"),sQuery(id+"F16.wireOp",EDGE,"E185"),sQuery(id+"F16.wireOp",EDGE,"E186"),sQuery(id+"F16.wireOp",EDGE,"E187"),sQuery(id+"F16.wireOp",EDGE,"E188"),sQuery(id+"F16.wireOp",EDGE,"E189"),sQuery(id+"F16.wireOp",EDGE,"E190"),sQuery(id+"F16.wireOp",EDGE,"E191"),sQuery(id+"F16.wireOp",EDGE,"E192"),sQuery(id+"F16.wireOp",EDGE,"E193"),sQuery(id+"F16.wireOp",EDGE,"E194"),sQuery(id+"F16.wireOp",EDGE,"E195"),sQuery(id+"F16.wireOp",EDGE,"E196"),sQuery(id+"F16.wireOp",EDGE,"E197"),sQuery(id+"F16.wireOp",EDGE,"E198"),sQuery(id+"F16.wireOp",EDGE,"E199"),sQuery(id+"F16.wireOp",EDGE,"E200"),sQuery(id+"F16.wireOp",EDGE,"E201"),sQuery(id+"F16.wireOp",EDGE,"E202"),sQuery(id+"F16.wireOp",EDGE,"E203"),sQuery(id+"F16.wireOp",EDGE,"E204"),sQuery(id+"F16.wireOp",EDGE,"E205"),sQuery(id+"F16.wireOp",EDGE,"E206"),sQuery(id+"F16.wireOp",EDGE,"E207"),sQuery(id+"F16.wireOp",EDGE,"E208"),sQuery(id+"F16.wireOp",EDGE,"E209"),sQuery(id+"F16.wireOp",EDGE,"E210"),sQuery(id+"F16.wireOp",EDGE,"E211"),sQuery(id+"F16.wireOp",EDGE,"E212"),sQuery(id+"F16.wireOp",EDGE,"E213"),sQuery(id+"F16.wireOp",EDGE,"E214"),sQuery(id+"F16.wireOp",EDGE,"E215"),sQuery(id+"F16.wireOp",EDGE,"E216"),sQuery(id+"F16.wireOp",EDGE,"E217"),sQuery(id+"F16.wireOp",EDGE,"E218"),sQuery(id+"F16.wireOp",EDGE,"E219"),sQuery(id+"F16.wireOp",EDGE,"E220"),sQuery(id+"F16.wireOp",EDGE,"E221"),sQuery(id+"F16.wireOp",EDGE,"E222"),sQuery(id+"F16.wireOp",EDGE,"E223"),sQuery(id+"F16.wireOp",EDGE,"E224"),sQuery(id+"F16.wireOp",EDGE,"E225"),sQuery(id+"F16.wireOp",EDGE,"E226"),sQuery(id+"F16.wireOp",EDGE,"E227"),sQuery(id+"F16.wireOp",EDGE,"E228"),sQuery(id+"F16.wireOp",EDGE,"E229"),sQuery(id+"F16.wireOp",EDGE,"E230"),sQuery(id+"F16.wireOp",EDGE,"E231"),sQuery(id+"F16.wireOp",EDGE,"E232"),sQuery(id+"F16.wireOp",EDGE,"E233"),sQuery(id+"F16.wireOp",EDGE,"E234")])]});
            var Q2;
            Q2=makeQuery(id+"F17.opExtrude","SWEPT_BODY",BODY,{"disambiguationData":[OSD([sQuery(id+"F16.wireOp",EDGE,"E235"),sQuery(id+"F16.wireOp",EDGE,"E236"),sQuery(id+"F16.wireOp",EDGE,"E237"),sQuery(id+"F16.wireOp",EDGE,"E238"),sQuery(id+"F16.wireOp",EDGE,"E239"),sQuery(id+"F16.wireOp",EDGE,"E240"),sQuery(id+"F16.wireOp",EDGE,"E241"),sQuery(id+"F16.wireOp",EDGE,"E242"),sQuery(id+"F16.wireOp",EDGE,"E243"),sQuery(id+"F16.wireOp",EDGE,"E244"),sQuery(id+"F16.wireOp",EDGE,"E245"),sQuery(id+"F16.wireOp",EDGE,"E246"),sQuery(id+"F16.wireOp",EDGE,"E247"),sQuery(id+"F16.wireOp",EDGE,"E248"),sQuery(id+"F16.wireOp",EDGE,"E249"),sQuery(id+"F16.wireOp",EDGE,"E250"),sQuery(id+"F16.wireOp",EDGE,"E251"),sQuery(id+"F16.wireOp",EDGE,"E252"),sQuery(id+"F16.wireOp",EDGE,"E253"),sQuery(id+"F16.wireOp",EDGE,"E254"),sQuery(id+"F16.wireOp",EDGE,"E255"),sQuery(id+"F16.wireOp",EDGE,"E256"),sQuery(id+"F16.wireOp",EDGE,"E257"),sQuery(id+"F16.wireOp",EDGE,"E258"),sQuery(id+"F16.wireOp",EDGE,"E259"),sQuery(id+"F16.wireOp",EDGE,"E260"),sQuery(id+"F16.wireOp",EDGE,"E261"),sQuery(id+"F16.wireOp",EDGE,"E262"),sQuery(id+"F16.wireOp",EDGE,"E263"),sQuery(id+"F16.wireOp",EDGE,"E264"),sQuery(id+"F16.wireOp",EDGE,"E265"),sQuery(id+"F16.wireOp",EDGE,"E266"),sQuery(id+"F16.wireOp",EDGE,"E267"),sQuery(id+"F16.wireOp",EDGE,"E268"),sQuery(id+"F16.wireOp",EDGE,"E269"),sQuery(id+"F16.wireOp",EDGE,"E270"),sQuery(id+"F16.wireOp",EDGE,"E271"),sQuery(id+"F16.wireOp",EDGE,"E272"),sQuery(id+"F16.wireOp",EDGE,"E273"),sQuery(id+"F16.wireOp",EDGE,"E274")])]});
            var Q3;
            Q3=makeQuery(id+"F17.opExtrude","SWEPT_BODY",BODY,{"disambiguationData":[OSD([sQuery(id+"F16.wireOp",EDGE,"E275"),sQuery(id+"F16.wireOp",EDGE,"E276"),sQuery(id+"F16.wireOp",EDGE,"E277"),sQuery(id+"F16.wireOp",EDGE,"E278"),sQuery(id+"F16.wireOp",EDGE,"E279"),sQuery(id+"F16.wireOp",EDGE,"E280"),sQuery(id+"F16.wireOp",EDGE,"E281"),sQuery(id+"F16.wireOp",EDGE,"E282"),sQuery(id+"F16.wireOp",EDGE,"E283"),sQuery(id+"F16.wireOp",EDGE,"E284"),sQuery(id+"F16.wireOp",EDGE,"E285"),sQuery(id+"F16.wireOp",EDGE,"E286"),sQuery(id+"F16.wireOp",EDGE,"E287"),sQuery(id+"F16.wireOp",EDGE,"E288"),sQuery(id+"F16.wireOp",EDGE,"E289"),sQuery(id+"F16.wireOp",EDGE,"E290"),sQuery(id+"F16.wireOp",EDGE,"E291"),sQuery(id+"F16.wireOp",EDGE,"E292"),sQuery(id+"F16.wireOp",EDGE,"E293"),sQuery(id+"F16.wireOp",EDGE,"E294"),sQuery(id+"F16.wireOp",EDGE,"E295"),sQuery(id+"F16.wireOp",EDGE,"E296"),sQuery(id+"F16.wireOp",EDGE,"E297"),sQuery(id+"F16.wireOp",EDGE,"E298"),sQuery(id+"F16.wireOp",EDGE,"E299")])]});
            var Q4;
            Q4=makeQuery(id+"F17.opExtrude","SWEPT_BODY",BODY,{"disambiguationData":[OSD([sQuery(id+"F16.wireOp",EDGE,"E300"),sQuery(id+"F16.wireOp",EDGE,"E301"),sQuery(id+"F16.wireOp",EDGE,"E302"),sQuery(id+"F16.wireOp",EDGE,"E303"),sQuery(id+"F16.wireOp",EDGE,"E304"),sQuery(id+"F16.wireOp",EDGE,"E305"),sQuery(id+"F16.wireOp",EDGE,"E306"),sQuery(id+"F16.wireOp",EDGE,"E307"),sQuery(id+"F16.wireOp",EDGE,"E308"),sQuery(id+"F16.wireOp",EDGE,"E309"),sQuery(id+"F16.wireOp",EDGE,"E310"),sQuery(id+"F16.wireOp",EDGE,"E311"),sQuery(id+"F16.wireOp",EDGE,"E312"),sQuery(id+"F16.wireOp",EDGE,"E313"),sQuery(id+"F16.wireOp",EDGE,"E314"),sQuery(id+"F16.wireOp",EDGE,"E315"),sQuery(id+"F16.wireOp",EDGE,"E316"),sQuery(id+"F16.wireOp",EDGE,"E317"),sQuery(id+"F16.wireOp",EDGE,"E318"),sQuery(id+"F16.wireOp",EDGE,"E319"),sQuery(id+"F16.wireOp",EDGE,"E320"),sQuery(id+"F16.wireOp",EDGE,"E321"),sQuery(id+"F16.wireOp",EDGE,"E322"),sQuery(id+"F16.wireOp",EDGE,"E323"),sQuery(id+"F16.wireOp",EDGE,"E324"),sQuery(id+"F16.wireOp",EDGE,"E325"),sQuery(id+"F16.wireOp",EDGE,"E326"),sQuery(id+"F16.wireOp",EDGE,"E327"),sQuery(id+"F16.wireOp",EDGE,"E328"),sQuery(id+"F16.wireOp",EDGE,"E329"),sQuery(id+"F16.wireOp",EDGE,"E330"),sQuery(id+"F16.wireOp",EDGE,"E331"),sQuery(id+"F16.wireOp",EDGE,"E332"),sQuery(id+"F16.wireOp",EDGE,"E333"),sQuery(id+"F16.wireOp",EDGE,"E334"),sQuery(id+"F16.wireOp",EDGE,"E335"),sQuery(id+"F16.wireOp",EDGE,"E336"),sQuery(id+"F16.wireOp",EDGE,"E337"),sQuery(id+"F16.wireOp",EDGE,"E338"),sQuery(id+"F16.wireOp",EDGE,"E339"),sQuery(id+"F16.wireOp",EDGE,"E340"),sQuery(id+"F16.wireOp",EDGE,"E341"),sQuery(id+"F16.wireOp",EDGE,"E342"),sQuery(id+"F16.wireOp",EDGE,"E343"),sQuery(id+"F16.wireOp",EDGE,"E344"),sQuery(id+"F16.wireOp",EDGE,"E345"),sQuery(id+"F16.wireOp",EDGE,"E346"),sQuery(id+"F16.wireOp",EDGE,"E347"),sQuery(id+"F16.wireOp",EDGE,"E348"),sQuery(id+"F16.wireOp",EDGE,"E349"),sQuery(id+"F16.wireOp",EDGE,"E350"),sQuery(id+"F16.wireOp",EDGE,"E351"),sQuery(id+"F16.wireOp",EDGE,"E352"),sQuery(id+"F16.wireOp",EDGE,"E353")])]});
            var Q5;
            Q5=makeQuery(id+"F17.opExtrude","SWEPT_BODY",BODY,{"disambiguationData":[OSD([sQuery(id+"F16.wireOp",EDGE,"E354"),sQuery(id+"F16.wireOp",EDGE,"E355"),sQuery(id+"F16.wireOp",EDGE,"E356"),sQuery(id+"F16.wireOp",EDGE,"E357"),sQuery(id+"F16.wireOp",EDGE,"E358"),sQuery(id+"F16.wireOp",EDGE,"E359"),sQuery(id+"F16.wireOp",EDGE,"E360"),sQuery(id+"F16.wireOp",EDGE,"E361"),sQuery(id+"F16.wireOp",EDGE,"E362"),sQuery(id+"F16.wireOp",EDGE,"E363"),sQuery(id+"F16.wireOp",EDGE,"E364"),sQuery(id+"F16.wireOp",EDGE,"E365"),sQuery(id+"F16.wireOp",EDGE,"E366"),sQuery(id+"F16.wireOp",EDGE,"E367"),sQuery(id+"F16.wireOp",EDGE,"E368"),sQuery(id+"F16.wireOp",EDGE,"E369"),sQuery(id+"F16.wireOp",EDGE,"E370"),sQuery(id+"F16.wireOp",EDGE,"E371"),sQuery(id+"F16.wireOp",EDGE,"E372"),sQuery(id+"F16.wireOp",EDGE,"E373"),sQuery(id+"F16.wireOp",EDGE,"E374"),sQuery(id+"F16.wireOp",EDGE,"E375"),sQuery(id+"F16.wireOp",EDGE,"E376"),sQuery(id+"F16.wireOp",EDGE,"E377"),sQuery(id+"F16.wireOp",EDGE,"E378"),sQuery(id+"F16.wireOp",EDGE,"E379"),sQuery(id+"F16.wireOp",EDGE,"E380"),sQuery(id+"F16.wireOp",EDGE,"E381"),sQuery(id+"F16.wireOp",EDGE,"E382"),sQuery(id+"F16.wireOp",EDGE,"E383"),sQuery(id+"F16.wireOp",EDGE,"E384"),sQuery(id+"F16.wireOp",EDGE,"E385"),sQuery(id+"F16.wireOp",EDGE,"E386"),sQuery(id+"F16.wireOp",EDGE,"E387"),sQuery(id+"F16.wireOp",EDGE,"E388"),sQuery(id+"F16.wireOp",EDGE,"E389"),sQuery(id+"F16.wireOp",EDGE,"E390"),sQuery(id+"F16.wireOp",EDGE,"E391"),sQuery(id+"F16.wireOp",EDGE,"E392"),sQuery(id+"F16.wireOp",EDGE,"E393"),sQuery(id+"F16.wireOp",EDGE,"E394"),sQuery(id+"F16.wireOp",EDGE,"E395"),sQuery(id+"F16.wireOp",EDGE,"E396"),sQuery(id+"F16.wireOp",EDGE,"E397"),sQuery(id+"F16.wireOp",EDGE,"E398"),sQuery(id+"F16.wireOp",EDGE,"E399"),sQuery(id+"F16.wireOp",EDGE,"E400"),sQuery(id+"F16.wireOp",EDGE,"E401"),sQuery(id+"F16.wireOp",EDGE,"E402"),sQuery(id+"F16.wireOp",EDGE,"E403"),sQuery(id+"F16.wireOp",EDGE,"E404"),sQuery(id+"F16.wireOp",EDGE,"E405"),sQuery(id+"F16.wireOp",EDGE,"E406"),sQuery(id+"F16.wireOp",EDGE,"E407"),sQuery(id+"F16.wireOp",EDGE,"E408"),sQuery(id+"F16.wireOp",EDGE,"E409"),sQuery(id+"F16.wireOp",EDGE,"E410"),sQuery(id+"F16.wireOp",EDGE,"E411"),sQuery(id+"F16.wireOp",EDGE,"E412"),sQuery(id+"F16.wireOp",EDGE,"E413"),sQuery(id+"F16.wireOp",EDGE,"E414"),sQuery(id+"F16.wireOp",EDGE,"E415"),sQuery(id+"F16.wireOp",EDGE,"E416"),sQuery(id+"F16.wireOp",EDGE,"E417"),sQuery(id+"F16.wireOp",EDGE,"E418"),sQuery(id+"F16.wireOp",EDGE,"E419"),sQuery(id+"F16.wireOp",EDGE,"E420"),sQuery(id+"F16.wireOp",EDGE,"E421"),sQuery(id+"F16.wireOp",EDGE,"E422"),sQuery(id+"F16.wireOp",EDGE,"E423"),sQuery(id+"F16.wireOp",EDGE,"E424"),sQuery(id+"F16.wireOp",EDGE,"E425"),sQuery(id+"F16.wireOp",EDGE,"E426"),sQuery(id+"F16.wireOp",EDGE,"E427"),sQuery(id+"F16.wireOp",EDGE,"E428"),sQuery(id+"F16.wireOp",EDGE,"E429"),sQuery(id+"F16.wireOp",EDGE,"E430"),sQuery(id+"F16.wireOp",EDGE,"E431")])]});
            var Q6;
            Q6=makeQuery(id+"F17.opExtrude","SWEPT_BODY",BODY,{"disambiguationData":[OSD([sQuery(id+"F16.wireOp",EDGE,"E432"),sQuery(id+"F16.wireOp",EDGE,"E433"),sQuery(id+"F16.wireOp",EDGE,"E434"),sQuery(id+"F16.wireOp",EDGE,"E435"),sQuery(id+"F16.wireOp",EDGE,"E436"),sQuery(id+"F16.wireOp",EDGE,"E437"),sQuery(id+"F16.wireOp",EDGE,"E438"),sQuery(id+"F16.wireOp",EDGE,"E439"),sQuery(id+"F16.wireOp",EDGE,"E440"),sQuery(id+"F16.wireOp",EDGE,"E441"),sQuery(id+"F16.wireOp",EDGE,"E442"),sQuery(id+"F16.wireOp",EDGE,"E443"),sQuery(id+"F16.wireOp",EDGE,"E444"),sQuery(id+"F16.wireOp",EDGE,"E445"),sQuery(id+"F16.wireOp",EDGE,"E446"),sQuery(id+"F16.wireOp",EDGE,"E447"),sQuery(id+"F16.wireOp",EDGE,"E448"),sQuery(id+"F16.wireOp",EDGE,"E449"),sQuery(id+"F16.wireOp",EDGE,"E450"),sQuery(id+"F16.wireOp",EDGE,"E451"),sQuery(id+"F16.wireOp",EDGE,"E452"),sQuery(id+"F16.wireOp",EDGE,"E453"),sQuery(id+"F16.wireOp",EDGE,"E454"),sQuery(id+"F16.wireOp",EDGE,"E455"),sQuery(id+"F16.wireOp",EDGE,"E456"),sQuery(id+"F16.wireOp",EDGE,"E457"),sQuery(id+"F16.wireOp",EDGE,"E458"),sQuery(id+"F16.wireOp",EDGE,"E459"),sQuery(id+"F16.wireOp",EDGE,"E460"),sQuery(id+"F16.wireOp",EDGE,"E461"),sQuery(id+"F16.wireOp",EDGE,"E462"),sQuery(id+"F16.wireOp",EDGE,"E463"),sQuery(id+"F16.wireOp",EDGE,"E464"),sQuery(id+"F16.wireOp",EDGE,"E465"),sQuery(id+"F16.wireOp",EDGE,"E466"),sQuery(id+"F16.wireOp",EDGE,"E467"),sQuery(id+"F16.wireOp",EDGE,"E468"),sQuery(id+"F16.wireOp",EDGE,"E469"),sQuery(id+"F16.wireOp",EDGE,"E470"),sQuery(id+"F16.wireOp",EDGE,"E471"),sQuery(id+"F16.wireOp",EDGE,"E472"),sQuery(id+"F16.wireOp",EDGE,"E473"),sQuery(id+"F16.wireOp",EDGE,"E474"),sQuery(id+"F16.wireOp",EDGE,"E475"),sQuery(id+"F16.wireOp",EDGE,"E476"),sQuery(id+"F16.wireOp",EDGE,"E477")])]});
            var Q7;
            Q7=makeQuery(id+"F17.opExtrude","SWEPT_BODY",BODY,{"disambiguationData":[OSD([sQuery(id+"F16.wireOp",EDGE,"E478"),sQuery(id+"F16.wireOp",EDGE,"E479"),sQuery(id+"F16.wireOp",EDGE,"E480"),sQuery(id+"F16.wireOp",EDGE,"E481"),sQuery(id+"F16.wireOp",EDGE,"E482"),sQuery(id+"F16.wireOp",EDGE,"E483"),sQuery(id+"F16.wireOp",EDGE,"E484"),sQuery(id+"F16.wireOp",EDGE,"E485"),sQuery(id+"F16.wireOp",EDGE,"E486"),sQuery(id+"F16.wireOp",EDGE,"E487"),sQuery(id+"F16.wireOp",EDGE,"E488"),sQuery(id+"F16.wireOp",EDGE,"E489"),sQuery(id+"F16.wireOp",EDGE,"E490"),sQuery(id+"F16.wireOp",EDGE,"E491"),sQuery(id+"F16.wireOp",EDGE,"E492"),sQuery(id+"F16.wireOp",EDGE,"E493"),sQuery(id+"F16.wireOp",EDGE,"E494"),sQuery(id+"F16.wireOp",EDGE,"E495"),sQuery(id+"F16.wireOp",EDGE,"E496"),sQuery(id+"F16.wireOp",EDGE,"E497"),sQuery(id+"F16.wireOp",EDGE,"E498"),sQuery(id+"F16.wireOp",EDGE,"E499"),sQuery(id+"F16.wireOp",EDGE,"E500"),sQuery(id+"F16.wireOp",EDGE,"E501"),sQuery(id+"F16.wireOp",EDGE,"E502"),sQuery(id+"F16.wireOp",EDGE,"E503"),sQuery(id+"F16.wireOp",EDGE,"E504"),sQuery(id+"F16.wireOp",EDGE,"E505"),sQuery(id+"F16.wireOp",EDGE,"E506"),sQuery(id+"F16.wireOp",EDGE,"E507"),sQuery(id+"F16.wireOp",EDGE,"E508"),sQuery(id+"F16.wireOp",EDGE,"E509"),sQuery(id+"F16.wireOp",EDGE,"E510"),sQuery(id+"F16.wireOp",EDGE,"E511"),sQuery(id+"F16.wireOp",EDGE,"E512"),sQuery(id+"F16.wireOp",EDGE,"E513"),sQuery(id+"F16.wireOp",EDGE,"E514"),sQuery(id+"F16.wireOp",EDGE,"E515"),sQuery(id+"F16.wireOp",EDGE,"E516"),sQuery(id+"F16.wireOp",EDGE,"E517"),sQuery(id+"F16.wireOp",EDGE,"E518"),sQuery(id+"F16.wireOp",EDGE,"E519"),sQuery(id+"F16.wireOp",EDGE,"E520"),sQuery(id+"F16.wireOp",EDGE,"E521"),sQuery(id+"F16.wireOp",EDGE,"E522"),sQuery(id+"F16.wireOp",EDGE,"E523"),sQuery(id+"F16.wireOp",EDGE,"E524"),sQuery(id+"F16.wireOp",EDGE,"E525"),sQuery(id+"F16.wireOp",EDGE,"E526"),sQuery(id+"F16.wireOp",EDGE,"E527"),sQuery(id+"F16.wireOp",EDGE,"E528"),sQuery(id+"F16.wireOp",EDGE,"E529"),sQuery(id+"F16.wireOp",EDGE,"E530"),sQuery(id+"F16.wireOp",EDGE,"E531"),sQuery(id+"F16.wireOp",EDGE,"E532"),sQuery(id+"F16.wireOp",EDGE,"E533"),sQuery(id+"F16.wireOp",EDGE,"E534")])]});
            var Q8;
            Q8=makeQuery(id+"F17.opExtrude","SWEPT_BODY",BODY,{"disambiguationData":[OSD([sQuery(id+"F16.wireOp",EDGE,"E535"),sQuery(id+"F16.wireOp",EDGE,"E536"),sQuery(id+"F16.wireOp",EDGE,"E537"),sQuery(id+"F16.wireOp",EDGE,"E538"),sQuery(id+"F16.wireOp",EDGE,"E539"),sQuery(id+"F16.wireOp",EDGE,"E540"),sQuery(id+"F16.wireOp",EDGE,"E541"),sQuery(id+"F16.wireOp",EDGE,"E542"),sQuery(id+"F16.wireOp",EDGE,"E543"),sQuery(id+"F16.wireOp",EDGE,"E544"),sQuery(id+"F16.wireOp",EDGE,"E545"),sQuery(id+"F16.wireOp",EDGE,"E546"),sQuery(id+"F16.wireOp",EDGE,"E547"),sQuery(id+"F16.wireOp",EDGE,"E548"),sQuery(id+"F16.wireOp",EDGE,"E549"),sQuery(id+"F16.wireOp",EDGE,"E550"),sQuery(id+"F16.wireOp",EDGE,"E551"),sQuery(id+"F16.wireOp",EDGE,"E552"),sQuery(id+"F16.wireOp",EDGE,"E553"),sQuery(id+"F16.wireOp",EDGE,"E554"),sQuery(id+"F16.wireOp",EDGE,"E555"),sQuery(id+"F16.wireOp",EDGE,"E556"),sQuery(id+"F16.wireOp",EDGE,"E557"),sQuery(id+"F16.wireOp",EDGE,"E558")])]});
            var Q9;
            Q9=makeQuery(id+"F17.opExtrude","SWEPT_BODY",BODY,{"disambiguationData":[OSD([sQuery(id+"F16.wireOp",EDGE,"E559"),sQuery(id+"F16.wireOp",EDGE,"E560"),sQuery(id+"F16.wireOp",EDGE,"E561"),sQuery(id+"F16.wireOp",EDGE,"E562"),sQuery(id+"F16.wireOp",EDGE,"E563"),sQuery(id+"F16.wireOp",EDGE,"E564"),sQuery(id+"F16.wireOp",EDGE,"E565"),sQuery(id+"F16.wireOp",EDGE,"E566"),sQuery(id+"F16.wireOp",EDGE,"E567"),sQuery(id+"F16.wireOp",EDGE,"E568"),sQuery(id+"F16.wireOp",EDGE,"E569"),sQuery(id+"F16.wireOp",EDGE,"E570"),sQuery(id+"F16.wireOp",EDGE,"E571"),sQuery(id+"F16.wireOp",EDGE,"E572"),sQuery(id+"F16.wireOp",EDGE,"E573"),sQuery(id+"F16.wireOp",EDGE,"E574"),sQuery(id+"F16.wireOp",EDGE,"E575"),sQuery(id+"F16.wireOp",EDGE,"E576"),sQuery(id+"F16.wireOp",EDGE,"E577"),sQuery(id+"F16.wireOp",EDGE,"E578"),sQuery(id+"F16.wireOp",EDGE,"E579"),sQuery(id+"F16.wireOp",EDGE,"E580"),sQuery(id+"F16.wireOp",EDGE,"E581"),sQuery(id+"F16.wireOp",EDGE,"E582"),sQuery(id+"F16.wireOp",EDGE,"E583"),sQuery(id+"F16.wireOp",EDGE,"E584"),sQuery(id+"F16.wireOp",EDGE,"E585"),sQuery(id+"F16.wireOp",EDGE,"E586"),sQuery(id+"F16.wireOp",EDGE,"E587"),sQuery(id+"F16.wireOp",EDGE,"E588"),sQuery(id+"F16.wireOp",EDGE,"E589"),sQuery(id+"F16.wireOp",EDGE,"E590"),sQuery(id+"F16.wireOp",EDGE,"E591"),sQuery(id+"F16.wireOp",EDGE,"E592")])]});
            var Q10;
            Q10=makeQuery(id+"F17.opExtrude","SWEPT_BODY",BODY,{"disambiguationData":[OSD([sQuery(id+"F16.wireOp",EDGE,"E593"),sQuery(id+"F16.wireOp",EDGE,"E594"),sQuery(id+"F16.wireOp",EDGE,"E595"),sQuery(id+"F16.wireOp",EDGE,"E596"),sQuery(id+"F16.wireOp",EDGE,"E597"),sQuery(id+"F16.wireOp",EDGE,"E598"),sQuery(id+"F16.wireOp",EDGE,"E599"),sQuery(id+"F16.wireOp",EDGE,"E600"),sQuery(id+"F16.wireOp",EDGE,"E601"),sQuery(id+"F16.wireOp",EDGE,"E602"),sQuery(id+"F16.wireOp",EDGE,"E603"),sQuery(id+"F16.wireOp",EDGE,"E604"),sQuery(id+"F16.wireOp",EDGE,"E605"),sQuery(id+"F16.wireOp",EDGE,"E606"),sQuery(id+"F16.wireOp",EDGE,"E607"),sQuery(id+"F16.wireOp",EDGE,"E608"),sQuery(id+"F16.wireOp",EDGE,"E609"),sQuery(id+"F16.wireOp",EDGE,"E610"),sQuery(id+"F16.wireOp",EDGE,"E611"),sQuery(id+"F16.wireOp",EDGE,"E612"),sQuery(id+"F16.wireOp",EDGE,"E613"),sQuery(id+"F16.wireOp",EDGE,"E614"),sQuery(id+"F16.wireOp",EDGE,"E615"),sQuery(id+"F16.wireOp",EDGE,"E616"),sQuery(id+"F16.wireOp",EDGE,"E617"),sQuery(id+"F16.wireOp",EDGE,"E618"),sQuery(id+"F16.wireOp",EDGE,"E619"),sQuery(id+"F16.wireOp",EDGE,"E620"),sQuery(id+"F16.wireOp",EDGE,"E621"),sQuery(id+"F16.wireOp",EDGE,"E622"),sQuery(id+"F16.wireOp",EDGE,"E623"),sQuery(id+"F16.wireOp",EDGE,"E624"),sQuery(id+"F16.wireOp",EDGE,"E625"),sQuery(id+"F16.wireOp",EDGE,"E626"),sQuery(id+"F16.wireOp",EDGE,"E627"),sQuery(id+"F16.wireOp",EDGE,"E628"),sQuery(id+"F16.wireOp",EDGE,"E629"),sQuery(id+"F16.wireOp",EDGE,"E630"),sQuery(id+"F16.wireOp",EDGE,"E631")])]});
            var Q11;
            Q11=makeQuery(id+"F17.opExtrude","SWEPT_BODY",BODY,{"disambiguationData":[OSD([sQuery(id+"F16.wireOp",EDGE,"E632"),sQuery(id+"F16.wireOp",EDGE,"E633"),sQuery(id+"F16.wireOp",EDGE,"E634"),sQuery(id+"F16.wireOp",EDGE,"E635"),sQuery(id+"F16.wireOp",EDGE,"E636"),sQuery(id+"F16.wireOp",EDGE,"E637"),sQuery(id+"F16.wireOp",EDGE,"E638"),sQuery(id+"F16.wireOp",EDGE,"E639"),sQuery(id+"F16.wireOp",EDGE,"E640"),sQuery(id+"F16.wireOp",EDGE,"E641"),sQuery(id+"F16.wireOp",EDGE,"E642"),sQuery(id+"F16.wireOp",EDGE,"E643"),sQuery(id+"F16.wireOp",EDGE,"E644"),sQuery(id+"F16.wireOp",EDGE,"E645"),sQuery(id+"F16.wireOp",EDGE,"E646"),sQuery(id+"F16.wireOp",EDGE,"E647"),sQuery(id+"F16.wireOp",EDGE,"E648"),sQuery(id+"F16.wireOp",EDGE,"E649"),sQuery(id+"F16.wireOp",EDGE,"E650"),sQuery(id+"F16.wireOp",EDGE,"E651"),sQuery(id+"F16.wireOp",EDGE,"E652"),sQuery(id+"F16.wireOp",EDGE,"E653"),sQuery(id+"F16.wireOp",EDGE,"E654"),sQuery(id+"F16.wireOp",EDGE,"E655"),sQuery(id+"F16.wireOp",EDGE,"E656"),sQuery(id+"F16.wireOp",EDGE,"E657"),sQuery(id+"F16.wireOp",EDGE,"E658"),sQuery(id+"F16.wireOp",EDGE,"E659"),sQuery(id+"F16.wireOp",EDGE,"E660"),sQuery(id+"F16.wireOp",EDGE,"E661"),sQuery(id+"F16.wireOp",EDGE,"E662"),sQuery(id+"F16.wireOp",EDGE,"E663"),sQuery(id+"F16.wireOp",EDGE,"E664"),sQuery(id+"F16.wireOp",EDGE,"E665"),sQuery(id+"F16.wireOp",EDGE,"E666"),sQuery(id+"F16.wireOp",EDGE,"E667"),sQuery(id+"F16.wireOp",EDGE,"E668"),sQuery(id+"F16.wireOp",EDGE,"E669"),sQuery(id+"F16.wireOp",EDGE,"E670"),sQuery(id+"F16.wireOp",EDGE,"E671"),sQuery(id+"F16.wireOp",EDGE,"E672"),sQuery(id+"F16.wireOp",EDGE,"E673"),sQuery(id+"F16.wireOp",EDGE,"E674"),sQuery(id+"F16.wireOp",EDGE,"E675"),sQuery(id+"F16.wireOp",EDGE,"E676"),sQuery(id+"F16.wireOp",EDGE,"E677"),sQuery(id+"F16.wireOp",EDGE,"E678"),sQuery(id+"F16.wireOp",EDGE,"E679"),sQuery(id+"F16.wireOp",EDGE,"E680"),sQuery(id+"F16.wireOp",EDGE,"E681"),sQuery(id+"F16.wireOp",EDGE,"E682"),sQuery(id+"F16.wireOp",EDGE,"E683"),sQuery(id+"F16.wireOp",EDGE,"E684"),sQuery(id+"F16.wireOp",EDGE,"E685"),sQuery(id+"F16.wireOp",EDGE,"E686"),sQuery(id+"F16.wireOp",EDGE,"E687"),sQuery(id+"F16.wireOp",EDGE,"E688"),sQuery(id+"F16.wireOp",EDGE,"E689"),sQuery(id+"F16.wireOp",EDGE,"E690"),sQuery(id+"F16.wireOp",EDGE,"E691"),sQuery(id+"F16.wireOp",EDGE,"E692"),sQuery(id+"F16.wireOp",EDGE,"E693"),sQuery(id+"F16.wireOp",EDGE,"E694"),sQuery(id+"F16.wireOp",EDGE,"E695")])]});
            var Q12;
            Q12=makeQuery(id+"F17.opExtrude","SWEPT_BODY",BODY,{"disambiguationData":[OSD([sQuery(id+"F16.wireOp",EDGE,"E696"),sQuery(id+"F16.wireOp",EDGE,"E697"),sQuery(id+"F16.wireOp",EDGE,"E698"),sQuery(id+"F16.wireOp",EDGE,"E699"),sQuery(id+"F16.wireOp",EDGE,"E700"),sQuery(id+"F16.wireOp",EDGE,"E701"),sQuery(id+"F16.wireOp",EDGE,"E702"),sQuery(id+"F16.wireOp",EDGE,"E703"),sQuery(id+"F16.wireOp",EDGE,"E704"),sQuery(id+"F16.wireOp",EDGE,"E705"),sQuery(id+"F16.wireOp",EDGE,"E706"),sQuery(id+"F16.wireOp",EDGE,"E707"),sQuery(id+"F16.wireOp",EDGE,"E708"),sQuery(id+"F16.wireOp",EDGE,"E709"),sQuery(id+"F16.wireOp",EDGE,"E710"),sQuery(id+"F16.wireOp",EDGE,"E711"),sQuery(id+"F16.wireOp",EDGE,"E712"),sQuery(id+"F16.wireOp",EDGE,"E713"),sQuery(id+"F16.wireOp",EDGE,"E714"),sQuery(id+"F16.wireOp",EDGE,"E715"),sQuery(id+"F16.wireOp",EDGE,"E716"),sQuery(id+"F16.wireOp",EDGE,"E717"),sQuery(id+"F16.wireOp",EDGE,"E718"),sQuery(id+"F16.wireOp",EDGE,"E719"),sQuery(id+"F16.wireOp",EDGE,"E720"),sQuery(id+"F16.wireOp",EDGE,"E721"),sQuery(id+"F16.wireOp",EDGE,"E722"),sQuery(id+"F16.wireOp",EDGE,"E723"),sQuery(id+"F16.wireOp",EDGE,"E724"),sQuery(id+"F16.wireOp",EDGE,"E725"),sQuery(id+"F16.wireOp",EDGE,"E726"),sQuery(id+"F16.wireOp",EDGE,"E727"),sQuery(id+"F16.wireOp",EDGE,"E728"),sQuery(id+"F16.wireOp",EDGE,"E729"),sQuery(id+"F16.wireOp",EDGE,"E730"),sQuery(id+"F16.wireOp",EDGE,"E731"),sQuery(id+"F16.wireOp",EDGE,"E732"),sQuery(id+"F16.wireOp",EDGE,"E733"),sQuery(id+"F16.wireOp",EDGE,"E734"),sQuery(id+"F16.wireOp",EDGE,"E735"),sQuery(id+"F16.wireOp",EDGE,"E736"),sQuery(id+"F16.wireOp",EDGE,"E737"),sQuery(id+"F16.wireOp",EDGE,"E738"),sQuery(id+"F16.wireOp",EDGE,"E739"),sQuery(id+"F16.wireOp",EDGE,"E740"),sQuery(id+"F16.wireOp",EDGE,"E741"),sQuery(id+"F16.wireOp",EDGE,"E742"),sQuery(id+"F16.wireOp",EDGE,"E743"),sQuery(id+"F16.wireOp",EDGE,"E744"),sQuery(id+"F16.wireOp",EDGE,"E745"),sQuery(id+"F16.wireOp",EDGE,"E746"),sQuery(id+"F16.wireOp",EDGE,"E747"),sQuery(id+"F16.wireOp",EDGE,"E748"),sQuery(id+"F16.wireOp",EDGE,"E749")])]});
            var Q13;
            Q13=makeQuery(id+"F17.opExtrude","SWEPT_BODY",BODY,{"disambiguationData":[OSD([sQuery(id+"F16.wireOp",EDGE,"E750"),sQuery(id+"F16.wireOp",EDGE,"E751"),sQuery(id+"F16.wireOp",EDGE,"E752"),sQuery(id+"F16.wireOp",EDGE,"E753"),sQuery(id+"F16.wireOp",EDGE,"E754"),sQuery(id+"F16.wireOp",EDGE,"E755"),sQuery(id+"F16.wireOp",EDGE,"E756"),sQuery(id+"F16.wireOp",EDGE,"E757"),sQuery(id+"F16.wireOp",EDGE,"E758"),sQuery(id+"F16.wireOp",EDGE,"E759"),sQuery(id+"F16.wireOp",EDGE,"E760"),sQuery(id+"F16.wireOp",EDGE,"E761"),sQuery(id+"F16.wireOp",EDGE,"E762"),sQuery(id+"F16.wireOp",EDGE,"E763"),sQuery(id+"F16.wireOp",EDGE,"E764"),sQuery(id+"F16.wireOp",EDGE,"E765"),sQuery(id+"F16.wireOp",EDGE,"E766"),sQuery(id+"F16.wireOp",EDGE,"E767"),sQuery(id+"F16.wireOp",EDGE,"E768"),sQuery(id+"F16.wireOp",EDGE,"E769"),sQuery(id+"F16.wireOp",EDGE,"E770"),sQuery(id+"F16.wireOp",EDGE,"E771"),sQuery(id+"F16.wireOp",EDGE,"E772"),sQuery(id+"F16.wireOp",EDGE,"E773"),sQuery(id+"F16.wireOp",EDGE,"E774"),sQuery(id+"F16.wireOp",EDGE,"E775"),sQuery(id+"F16.wireOp",EDGE,"E776"),sQuery(id+"F16.wireOp",EDGE,"E777"),sQuery(id+"F16.wireOp",EDGE,"E778"),sQuery(id+"F16.wireOp",EDGE,"E779"),sQuery(id+"F16.wireOp",EDGE,"E780"),sQuery(id+"F16.wireOp",EDGE,"E781"),sQuery(id+"F16.wireOp",EDGE,"E782"),sQuery(id+"F16.wireOp",EDGE,"E783"),sQuery(id+"F16.wireOp",EDGE,"E784"),sQuery(id+"F16.wireOp",EDGE,"E785"),sQuery(id+"F16.wireOp",EDGE,"E786"),sQuery(id+"F16.wireOp",EDGE,"E787"),sQuery(id+"F16.wireOp",EDGE,"E788"),sQuery(id+"F16.wireOp",EDGE,"E789"),sQuery(id+"F16.wireOp",EDGE,"E790"),sQuery(id+"F16.wireOp",EDGE,"E791"),sQuery(id+"F16.wireOp",EDGE,"E792"),sQuery(id+"F16.wireOp",EDGE,"E793"),sQuery(id+"F16.wireOp",EDGE,"E794"),sQuery(id+"F16.wireOp",EDGE,"E795"),sQuery(id+"F16.wireOp",EDGE,"E796"),sQuery(id+"F16.wireOp",EDGE,"E797"),sQuery(id+"F16.wireOp",EDGE,"E798"),sQuery(id+"F16.wireOp",EDGE,"E799"),sQuery(id+"F16.wireOp",EDGE,"E800"),sQuery(id+"F16.wireOp",EDGE,"E801"),sQuery(id+"F16.wireOp",EDGE,"E802"),sQuery(id+"F16.wireOp",EDGE,"E803"),sQuery(id+"F16.wireOp",EDGE,"E804"),sQuery(id+"F16.wireOp",EDGE,"E805"),sQuery(id+"F16.wireOp",EDGE,"E806"),sQuery(id+"F16.wireOp",EDGE,"E807"),sQuery(id+"F16.wireOp",EDGE,"E808"),sQuery(id+"F16.wireOp",EDGE,"E809"),sQuery(id+"F16.wireOp",EDGE,"E810"),sQuery(id+"F16.wireOp",EDGE,"E811"),sQuery(id+"F16.wireOp",EDGE,"E812"),sQuery(id+"F16.wireOp",EDGE,"E813")])]});
            var Q14;
            Q14=qCreatedBy(makeId("Origin.pointOp"),VERTEX);
            transform(context, id + "F19", {"entities" : qUnion([Q0, Q1, Q2, Q3, Q4, Q5, Q6, Q7, Q8, Q9, Q10, Q11, Q12, Q13]), "transformType" : TransformType.SCALE_UNIFORMLY, "scale" : 0.26, "scalePoint" : qUnion([Q14]), "makeCopy" : false});
        }
        {
            var Q0;
            Q0=makeQuery(id+"F17.opExtrude","SWEPT_BODY",BODY,{"disambiguationData":[OSD([sQuery(id+"F16.wireOp",EDGE,"E47"),sQuery(id+"F16.wireOp",EDGE,"E48"),sQuery(id+"F16.wireOp",EDGE,"E49"),sQuery(id+"F16.wireOp",EDGE,"E50"),sQuery(id+"F16.wireOp",EDGE,"E51"),sQuery(id+"F16.wireOp",EDGE,"E52"),sQuery(id+"F16.wireOp",EDGE,"E53"),sQuery(id+"F16.wireOp",EDGE,"E54"),sQuery(id+"F16.wireOp",EDGE,"E55"),sQuery(id+"F16.wireOp",EDGE,"E56"),sQuery(id+"F16.wireOp",EDGE,"E57"),sQuery(id+"F16.wireOp",EDGE,"E58"),sQuery(id+"F16.wireOp",EDGE,"E59"),sQuery(id+"F16.wireOp",EDGE,"E60"),sQuery(id+"F16.wireOp",EDGE,"E61"),sQuery(id+"F16.wireOp",EDGE,"E62"),sQuery(id+"F16.wireOp",EDGE,"E63"),sQuery(id+"F16.wireOp",EDGE,"E64"),sQuery(id+"F16.wireOp",EDGE,"E65"),sQuery(id+"F16.wireOp",EDGE,"E66"),sQuery(id+"F16.wireOp",EDGE,"E67"),sQuery(id+"F16.wireOp",EDGE,"E68"),sQuery(id+"F16.wireOp",EDGE,"E69"),sQuery(id+"F16.wireOp",EDGE,"E70"),sQuery(id+"F16.wireOp",EDGE,"E71"),sQuery(id+"F16.wireOp",EDGE,"E72"),sQuery(id+"F16.wireOp",EDGE,"E73"),sQuery(id+"F16.wireOp",EDGE,"E74"),sQuery(id+"F16.wireOp",EDGE,"E75"),sQuery(id+"F16.wireOp",EDGE,"E76"),sQuery(id+"F16.wireOp",EDGE,"E77"),sQuery(id+"F16.wireOp",EDGE,"E78"),sQuery(id+"F16.wireOp",EDGE,"E79"),sQuery(id+"F16.wireOp",EDGE,"E80"),sQuery(id+"F16.wireOp",EDGE,"E81"),sQuery(id+"F16.wireOp",EDGE,"E82"),sQuery(id+"F16.wireOp",EDGE,"E83"),sQuery(id+"F16.wireOp",EDGE,"E84"),sQuery(id+"F16.wireOp",EDGE,"E85"),sQuery(id+"F16.wireOp",EDGE,"E86"),sQuery(id+"F16.wireOp",EDGE,"E87"),sQuery(id+"F16.wireOp",EDGE,"E88"),sQuery(id+"F16.wireOp",EDGE,"E89"),sQuery(id+"F16.wireOp",EDGE,"E90"),sQuery(id+"F16.wireOp",EDGE,"E91"),sQuery(id+"F16.wireOp",EDGE,"E92"),sQuery(id+"F16.wireOp",EDGE,"E93"),sQuery(id+"F16.wireOp",EDGE,"E94"),sQuery(id+"F16.wireOp",EDGE,"E95"),sQuery(id+"F16.wireOp",EDGE,"E96"),sQuery(id+"F16.wireOp",EDGE,"E97"),sQuery(id+"F16.wireOp",EDGE,"E98"),sQuery(id+"F16.wireOp",EDGE,"E99"),sQuery(id+"F16.wireOp",EDGE,"E100"),sQuery(id+"F16.wireOp",EDGE,"E101"),sQuery(id+"F16.wireOp",EDGE,"E102"),sQuery(id+"F16.wireOp",EDGE,"E103"),sQuery(id+"F16.wireOp",EDGE,"E104"),sQuery(id+"F16.wireOp",EDGE,"E105"),sQuery(id+"F16.wireOp",EDGE,"E106"),sQuery(id+"F16.wireOp",EDGE,"E107"),sQuery(id+"F16.wireOp",EDGE,"E108"),sQuery(id+"F16.wireOp",EDGE,"E109"),sQuery(id+"F16.wireOp",EDGE,"E110"),sQuery(id+"F16.wireOp",EDGE,"E111"),sQuery(id+"F16.wireOp",EDGE,"E112"),sQuery(id+"F16.wireOp",EDGE,"E113"),sQuery(id+"F16.wireOp",EDGE,"E114"),sQuery(id+"F16.wireOp",EDGE,"E115")])]});
            var Q1;
            Q1=makeQuery(id+"F17.opExtrude","SWEPT_BODY",BODY,{"disambiguationData":[OSD([sQuery(id+"F16.wireOp",EDGE,"E116"),sQuery(id+"F16.wireOp",EDGE,"E117"),sQuery(id+"F16.wireOp",EDGE,"E118"),sQuery(id+"F16.wireOp",EDGE,"E119"),sQuery(id+"F16.wireOp",EDGE,"E120"),sQuery(id+"F16.wireOp",EDGE,"E121"),sQuery(id+"F16.wireOp",EDGE,"E122"),sQuery(id+"F16.wireOp",EDGE,"E123"),sQuery(id+"F16.wireOp",EDGE,"E124"),sQuery(id+"F16.wireOp",EDGE,"E125"),sQuery(id+"F16.wireOp",EDGE,"E126"),sQuery(id+"F16.wireOp",EDGE,"E127"),sQuery(id+"F16.wireOp",EDGE,"E128"),sQuery(id+"F16.wireOp",EDGE,"E129"),sQuery(id+"F16.wireOp",EDGE,"E130"),sQuery(id+"F16.wireOp",EDGE,"E131"),sQuery(id+"F16.wireOp",EDGE,"E132"),sQuery(id+"F16.wireOp",EDGE,"E133"),sQuery(id+"F16.wireOp",EDGE,"E134"),sQuery(id+"F16.wireOp",EDGE,"E135"),sQuery(id+"F16.wireOp",EDGE,"E136"),sQuery(id+"F16.wireOp",EDGE,"E137"),sQuery(id+"F16.wireOp",EDGE,"E138"),sQuery(id+"F16.wireOp",EDGE,"E139"),sQuery(id+"F16.wireOp",EDGE,"E140"),sQuery(id+"F16.wireOp",EDGE,"E141"),sQuery(id+"F16.wireOp",EDGE,"E142"),sQuery(id+"F16.wireOp",EDGE,"E143"),sQuery(id+"F16.wireOp",EDGE,"E144"),sQuery(id+"F16.wireOp",EDGE,"E145"),sQuery(id+"F16.wireOp",EDGE,"E146"),sQuery(id+"F16.wireOp",EDGE,"E147"),sQuery(id+"F16.wireOp",EDGE,"E148"),sQuery(id+"F16.wireOp",EDGE,"E149"),sQuery(id+"F16.wireOp",EDGE,"E150"),sQuery(id+"F16.wireOp",EDGE,"E151"),sQuery(id+"F16.wireOp",EDGE,"E152"),sQuery(id+"F16.wireOp",EDGE,"E153"),sQuery(id+"F16.wireOp",EDGE,"E154"),sQuery(id+"F16.wireOp",EDGE,"E155"),sQuery(id+"F16.wireOp",EDGE,"E156"),sQuery(id+"F16.wireOp",EDGE,"E157"),sQuery(id+"F16.wireOp",EDGE,"E158"),sQuery(id+"F16.wireOp",EDGE,"E159"),sQuery(id+"F16.wireOp",EDGE,"E160"),sQuery(id+"F16.wireOp",EDGE,"E161"),sQuery(id+"F16.wireOp",EDGE,"E162"),sQuery(id+"F16.wireOp",EDGE,"E163"),sQuery(id+"F16.wireOp",EDGE,"E164"),sQuery(id+"F16.wireOp",EDGE,"E165"),sQuery(id+"F16.wireOp",EDGE,"E166"),sQuery(id+"F16.wireOp",EDGE,"E167"),sQuery(id+"F16.wireOp",EDGE,"E168"),sQuery(id+"F16.wireOp",EDGE,"E169"),sQuery(id+"F16.wireOp",EDGE,"E170"),sQuery(id+"F16.wireOp",EDGE,"E171"),sQuery(id+"F16.wireOp",EDGE,"E172"),sQuery(id+"F16.wireOp",EDGE,"E173"),sQuery(id+"F16.wireOp",EDGE,"E174"),sQuery(id+"F16.wireOp",EDGE,"E175"),sQuery(id+"F16.wireOp",EDGE,"E176"),sQuery(id+"F16.wireOp",EDGE,"E177"),sQuery(id+"F16.wireOp",EDGE,"E178"),sQuery(id+"F16.wireOp",EDGE,"E179"),sQuery(id+"F16.wireOp",EDGE,"E180"),sQuery(id+"F16.wireOp",EDGE,"E181"),sQuery(id+"F16.wireOp",EDGE,"E182"),sQuery(id+"F16.wireOp",EDGE,"E183"),sQuery(id+"F16.wireOp",EDGE,"E184"),sQuery(id+"F16.wireOp",EDGE,"E185"),sQuery(id+"F16.wireOp",EDGE,"E186"),sQuery(id+"F16.wireOp",EDGE,"E187"),sQuery(id+"F16.wireOp",EDGE,"E188"),sQuery(id+"F16.wireOp",EDGE,"E189"),sQuery(id+"F16.wireOp",EDGE,"E190"),sQuery(id+"F16.wireOp",EDGE,"E191"),sQuery(id+"F16.wireOp",EDGE,"E192"),sQuery(id+"F16.wireOp",EDGE,"E193"),sQuery(id+"F16.wireOp",EDGE,"E194"),sQuery(id+"F16.wireOp",EDGE,"E195"),sQuery(id+"F16.wireOp",EDGE,"E196"),sQuery(id+"F16.wireOp",EDGE,"E197"),sQuery(id+"F16.wireOp",EDGE,"E198"),sQuery(id+"F16.wireOp",EDGE,"E199"),sQuery(id+"F16.wireOp",EDGE,"E200"),sQuery(id+"F16.wireOp",EDGE,"E201"),sQuery(id+"F16.wireOp",EDGE,"E202"),sQuery(id+"F16.wireOp",EDGE,"E203"),sQuery(id+"F16.wireOp",EDGE,"E204"),sQuery(id+"F16.wireOp",EDGE,"E205"),sQuery(id+"F16.wireOp",EDGE,"E206"),sQuery(id+"F16.wireOp",EDGE,"E207"),sQuery(id+"F16.wireOp",EDGE,"E208"),sQuery(id+"F16.wireOp",EDGE,"E209"),sQuery(id+"F16.wireOp",EDGE,"E210"),sQuery(id+"F16.wireOp",EDGE,"E211"),sQuery(id+"F16.wireOp",EDGE,"E212"),sQuery(id+"F16.wireOp",EDGE,"E213"),sQuery(id+"F16.wireOp",EDGE,"E214"),sQuery(id+"F16.wireOp",EDGE,"E215"),sQuery(id+"F16.wireOp",EDGE,"E216"),sQuery(id+"F16.wireOp",EDGE,"E217"),sQuery(id+"F16.wireOp",EDGE,"E218"),sQuery(id+"F16.wireOp",EDGE,"E219"),sQuery(id+"F16.wireOp",EDGE,"E220"),sQuery(id+"F16.wireOp",EDGE,"E221"),sQuery(id+"F16.wireOp",EDGE,"E222"),sQuery(id+"F16.wireOp",EDGE,"E223"),sQuery(id+"F16.wireOp",EDGE,"E224"),sQuery(id+"F16.wireOp",EDGE,"E225"),sQuery(id+"F16.wireOp",EDGE,"E226"),sQuery(id+"F16.wireOp",EDGE,"E227"),sQuery(id+"F16.wireOp",EDGE,"E228"),sQuery(id+"F16.wireOp",EDGE,"E229"),sQuery(id+"F16.wireOp",EDGE,"E230"),sQuery(id+"F16.wireOp",EDGE,"E231"),sQuery(id+"F16.wireOp",EDGE,"E232"),sQuery(id+"F16.wireOp",EDGE,"E233"),sQuery(id+"F16.wireOp",EDGE,"E234")])]});
            var Q2;
            Q2=makeQuery(id+"F17.opExtrude","SWEPT_BODY",BODY,{"disambiguationData":[OSD([sQuery(id+"F16.wireOp",EDGE,"E235"),sQuery(id+"F16.wireOp",EDGE,"E236"),sQuery(id+"F16.wireOp",EDGE,"E237"),sQuery(id+"F16.wireOp",EDGE,"E238"),sQuery(id+"F16.wireOp",EDGE,"E239"),sQuery(id+"F16.wireOp",EDGE,"E240"),sQuery(id+"F16.wireOp",EDGE,"E241"),sQuery(id+"F16.wireOp",EDGE,"E242"),sQuery(id+"F16.wireOp",EDGE,"E243"),sQuery(id+"F16.wireOp",EDGE,"E244"),sQuery(id+"F16.wireOp",EDGE,"E245"),sQuery(id+"F16.wireOp",EDGE,"E246"),sQuery(id+"F16.wireOp",EDGE,"E247"),sQuery(id+"F16.wireOp",EDGE,"E248"),sQuery(id+"F16.wireOp",EDGE,"E249"),sQuery(id+"F16.wireOp",EDGE,"E250"),sQuery(id+"F16.wireOp",EDGE,"E251"),sQuery(id+"F16.wireOp",EDGE,"E252"),sQuery(id+"F16.wireOp",EDGE,"E253"),sQuery(id+"F16.wireOp",EDGE,"E254"),sQuery(id+"F16.wireOp",EDGE,"E255"),sQuery(id+"F16.wireOp",EDGE,"E256"),sQuery(id+"F16.wireOp",EDGE,"E257"),sQuery(id+"F16.wireOp",EDGE,"E258"),sQuery(id+"F16.wireOp",EDGE,"E259"),sQuery(id+"F16.wireOp",EDGE,"E260"),sQuery(id+"F16.wireOp",EDGE,"E261"),sQuery(id+"F16.wireOp",EDGE,"E262"),sQuery(id+"F16.wireOp",EDGE,"E263"),sQuery(id+"F16.wireOp",EDGE,"E264"),sQuery(id+"F16.wireOp",EDGE,"E265"),sQuery(id+"F16.wireOp",EDGE,"E266"),sQuery(id+"F16.wireOp",EDGE,"E267"),sQuery(id+"F16.wireOp",EDGE,"E268"),sQuery(id+"F16.wireOp",EDGE,"E269"),sQuery(id+"F16.wireOp",EDGE,"E270"),sQuery(id+"F16.wireOp",EDGE,"E271"),sQuery(id+"F16.wireOp",EDGE,"E272"),sQuery(id+"F16.wireOp",EDGE,"E273"),sQuery(id+"F16.wireOp",EDGE,"E274")])]});
            var Q3;
            Q3=makeQuery(id+"F17.opExtrude","SWEPT_BODY",BODY,{"disambiguationData":[OSD([sQuery(id+"F16.wireOp",EDGE,"E275"),sQuery(id+"F16.wireOp",EDGE,"E276"),sQuery(id+"F16.wireOp",EDGE,"E277"),sQuery(id+"F16.wireOp",EDGE,"E278"),sQuery(id+"F16.wireOp",EDGE,"E279"),sQuery(id+"F16.wireOp",EDGE,"E280"),sQuery(id+"F16.wireOp",EDGE,"E281"),sQuery(id+"F16.wireOp",EDGE,"E282"),sQuery(id+"F16.wireOp",EDGE,"E283"),sQuery(id+"F16.wireOp",EDGE,"E284"),sQuery(id+"F16.wireOp",EDGE,"E285"),sQuery(id+"F16.wireOp",EDGE,"E286"),sQuery(id+"F16.wireOp",EDGE,"E287"),sQuery(id+"F16.wireOp",EDGE,"E288"),sQuery(id+"F16.wireOp",EDGE,"E289"),sQuery(id+"F16.wireOp",EDGE,"E290"),sQuery(id+"F16.wireOp",EDGE,"E291"),sQuery(id+"F16.wireOp",EDGE,"E292"),sQuery(id+"F16.wireOp",EDGE,"E293"),sQuery(id+"F16.wireOp",EDGE,"E294"),sQuery(id+"F16.wireOp",EDGE,"E295"),sQuery(id+"F16.wireOp",EDGE,"E296"),sQuery(id+"F16.wireOp",EDGE,"E297"),sQuery(id+"F16.wireOp",EDGE,"E298"),sQuery(id+"F16.wireOp",EDGE,"E299")])]});
            var Q4;
            Q4=makeQuery(id+"F17.opExtrude","SWEPT_BODY",BODY,{"disambiguationData":[OSD([sQuery(id+"F16.wireOp",EDGE,"E300"),sQuery(id+"F16.wireOp",EDGE,"E301"),sQuery(id+"F16.wireOp",EDGE,"E302"),sQuery(id+"F16.wireOp",EDGE,"E303"),sQuery(id+"F16.wireOp",EDGE,"E304"),sQuery(id+"F16.wireOp",EDGE,"E305"),sQuery(id+"F16.wireOp",EDGE,"E306"),sQuery(id+"F16.wireOp",EDGE,"E307"),sQuery(id+"F16.wireOp",EDGE,"E308"),sQuery(id+"F16.wireOp",EDGE,"E309"),sQuery(id+"F16.wireOp",EDGE,"E310"),sQuery(id+"F16.wireOp",EDGE,"E311"),sQuery(id+"F16.wireOp",EDGE,"E312"),sQuery(id+"F16.wireOp",EDGE,"E313"),sQuery(id+"F16.wireOp",EDGE,"E314"),sQuery(id+"F16.wireOp",EDGE,"E315"),sQuery(id+"F16.wireOp",EDGE,"E316"),sQuery(id+"F16.wireOp",EDGE,"E317"),sQuery(id+"F16.wireOp",EDGE,"E318"),sQuery(id+"F16.wireOp",EDGE,"E319"),sQuery(id+"F16.wireOp",EDGE,"E320"),sQuery(id+"F16.wireOp",EDGE,"E321"),sQuery(id+"F16.wireOp",EDGE,"E322"),sQuery(id+"F16.wireOp",EDGE,"E323"),sQuery(id+"F16.wireOp",EDGE,"E324"),sQuery(id+"F16.wireOp",EDGE,"E325"),sQuery(id+"F16.wireOp",EDGE,"E326"),sQuery(id+"F16.wireOp",EDGE,"E327"),sQuery(id+"F16.wireOp",EDGE,"E328"),sQuery(id+"F16.wireOp",EDGE,"E329"),sQuery(id+"F16.wireOp",EDGE,"E330"),sQuery(id+"F16.wireOp",EDGE,"E331"),sQuery(id+"F16.wireOp",EDGE,"E332"),sQuery(id+"F16.wireOp",EDGE,"E333"),sQuery(id+"F16.wireOp",EDGE,"E334"),sQuery(id+"F16.wireOp",EDGE,"E335"),sQuery(id+"F16.wireOp",EDGE,"E336"),sQuery(id+"F16.wireOp",EDGE,"E337"),sQuery(id+"F16.wireOp",EDGE,"E338"),sQuery(id+"F16.wireOp",EDGE,"E339"),sQuery(id+"F16.wireOp",EDGE,"E340"),sQuery(id+"F16.wireOp",EDGE,"E341"),sQuery(id+"F16.wireOp",EDGE,"E342"),sQuery(id+"F16.wireOp",EDGE,"E343"),sQuery(id+"F16.wireOp",EDGE,"E344"),sQuery(id+"F16.wireOp",EDGE,"E345"),sQuery(id+"F16.wireOp",EDGE,"E346"),sQuery(id+"F16.wireOp",EDGE,"E347"),sQuery(id+"F16.wireOp",EDGE,"E348"),sQuery(id+"F16.wireOp",EDGE,"E349"),sQuery(id+"F16.wireOp",EDGE,"E350"),sQuery(id+"F16.wireOp",EDGE,"E351"),sQuery(id+"F16.wireOp",EDGE,"E352"),sQuery(id+"F16.wireOp",EDGE,"E353")])]});
            var Q5;
            Q5=makeQuery(id+"F17.opExtrude","SWEPT_BODY",BODY,{"disambiguationData":[OSD([sQuery(id+"F16.wireOp",EDGE,"E354"),sQuery(id+"F16.wireOp",EDGE,"E355"),sQuery(id+"F16.wireOp",EDGE,"E356"),sQuery(id+"F16.wireOp",EDGE,"E357"),sQuery(id+"F16.wireOp",EDGE,"E358"),sQuery(id+"F16.wireOp",EDGE,"E359"),sQuery(id+"F16.wireOp",EDGE,"E360"),sQuery(id+"F16.wireOp",EDGE,"E361"),sQuery(id+"F16.wireOp",EDGE,"E362"),sQuery(id+"F16.wireOp",EDGE,"E363"),sQuery(id+"F16.wireOp",EDGE,"E364"),sQuery(id+"F16.wireOp",EDGE,"E365"),sQuery(id+"F16.wireOp",EDGE,"E366"),sQuery(id+"F16.wireOp",EDGE,"E367"),sQuery(id+"F16.wireOp",EDGE,"E368"),sQuery(id+"F16.wireOp",EDGE,"E369"),sQuery(id+"F16.wireOp",EDGE,"E370"),sQuery(id+"F16.wireOp",EDGE,"E371"),sQuery(id+"F16.wireOp",EDGE,"E372"),sQuery(id+"F16.wireOp",EDGE,"E373"),sQuery(id+"F16.wireOp",EDGE,"E374"),sQuery(id+"F16.wireOp",EDGE,"E375"),sQuery(id+"F16.wireOp",EDGE,"E376"),sQuery(id+"F16.wireOp",EDGE,"E377"),sQuery(id+"F16.wireOp",EDGE,"E378"),sQuery(id+"F16.wireOp",EDGE,"E379"),sQuery(id+"F16.wireOp",EDGE,"E380"),sQuery(id+"F16.wireOp",EDGE,"E381"),sQuery(id+"F16.wireOp",EDGE,"E382"),sQuery(id+"F16.wireOp",EDGE,"E383"),sQuery(id+"F16.wireOp",EDGE,"E384"),sQuery(id+"F16.wireOp",EDGE,"E385"),sQuery(id+"F16.wireOp",EDGE,"E386"),sQuery(id+"F16.wireOp",EDGE,"E387"),sQuery(id+"F16.wireOp",EDGE,"E388"),sQuery(id+"F16.wireOp",EDGE,"E389"),sQuery(id+"F16.wireOp",EDGE,"E390"),sQuery(id+"F16.wireOp",EDGE,"E391"),sQuery(id+"F16.wireOp",EDGE,"E392"),sQuery(id+"F16.wireOp",EDGE,"E393"),sQuery(id+"F16.wireOp",EDGE,"E394"),sQuery(id+"F16.wireOp",EDGE,"E395"),sQuery(id+"F16.wireOp",EDGE,"E396"),sQuery(id+"F16.wireOp",EDGE,"E397"),sQuery(id+"F16.wireOp",EDGE,"E398"),sQuery(id+"F16.wireOp",EDGE,"E399"),sQuery(id+"F16.wireOp",EDGE,"E400"),sQuery(id+"F16.wireOp",EDGE,"E401"),sQuery(id+"F16.wireOp",EDGE,"E402"),sQuery(id+"F16.wireOp",EDGE,"E403"),sQuery(id+"F16.wireOp",EDGE,"E404"),sQuery(id+"F16.wireOp",EDGE,"E405"),sQuery(id+"F16.wireOp",EDGE,"E406"),sQuery(id+"F16.wireOp",EDGE,"E407"),sQuery(id+"F16.wireOp",EDGE,"E408"),sQuery(id+"F16.wireOp",EDGE,"E409"),sQuery(id+"F16.wireOp",EDGE,"E410"),sQuery(id+"F16.wireOp",EDGE,"E411"),sQuery(id+"F16.wireOp",EDGE,"E412"),sQuery(id+"F16.wireOp",EDGE,"E413"),sQuery(id+"F16.wireOp",EDGE,"E414"),sQuery(id+"F16.wireOp",EDGE,"E415"),sQuery(id+"F16.wireOp",EDGE,"E416"),sQuery(id+"F16.wireOp",EDGE,"E417"),sQuery(id+"F16.wireOp",EDGE,"E418"),sQuery(id+"F16.wireOp",EDGE,"E419"),sQuery(id+"F16.wireOp",EDGE,"E420"),sQuery(id+"F16.wireOp",EDGE,"E421"),sQuery(id+"F16.wireOp",EDGE,"E422"),sQuery(id+"F16.wireOp",EDGE,"E423"),sQuery(id+"F16.wireOp",EDGE,"E424"),sQuery(id+"F16.wireOp",EDGE,"E425"),sQuery(id+"F16.wireOp",EDGE,"E426"),sQuery(id+"F16.wireOp",EDGE,"E427"),sQuery(id+"F16.wireOp",EDGE,"E428"),sQuery(id+"F16.wireOp",EDGE,"E429"),sQuery(id+"F16.wireOp",EDGE,"E430"),sQuery(id+"F16.wireOp",EDGE,"E431")])]});
            var Q6;
            Q6=makeQuery(id+"F17.opExtrude","SWEPT_BODY",BODY,{"disambiguationData":[OSD([sQuery(id+"F16.wireOp",EDGE,"E432"),sQuery(id+"F16.wireOp",EDGE,"E433"),sQuery(id+"F16.wireOp",EDGE,"E434"),sQuery(id+"F16.wireOp",EDGE,"E435"),sQuery(id+"F16.wireOp",EDGE,"E436"),sQuery(id+"F16.wireOp",EDGE,"E437"),sQuery(id+"F16.wireOp",EDGE,"E438"),sQuery(id+"F16.wireOp",EDGE,"E439"),sQuery(id+"F16.wireOp",EDGE,"E440"),sQuery(id+"F16.wireOp",EDGE,"E441"),sQuery(id+"F16.wireOp",EDGE,"E442"),sQuery(id+"F16.wireOp",EDGE,"E443"),sQuery(id+"F16.wireOp",EDGE,"E444"),sQuery(id+"F16.wireOp",EDGE,"E445"),sQuery(id+"F16.wireOp",EDGE,"E446"),sQuery(id+"F16.wireOp",EDGE,"E447"),sQuery(id+"F16.wireOp",EDGE,"E448"),sQuery(id+"F16.wireOp",EDGE,"E449"),sQuery(id+"F16.wireOp",EDGE,"E450"),sQuery(id+"F16.wireOp",EDGE,"E451"),sQuery(id+"F16.wireOp",EDGE,"E452"),sQuery(id+"F16.wireOp",EDGE,"E453"),sQuery(id+"F16.wireOp",EDGE,"E454"),sQuery(id+"F16.wireOp",EDGE,"E455"),sQuery(id+"F16.wireOp",EDGE,"E456"),sQuery(id+"F16.wireOp",EDGE,"E457"),sQuery(id+"F16.wireOp",EDGE,"E458"),sQuery(id+"F16.wireOp",EDGE,"E459"),sQuery(id+"F16.wireOp",EDGE,"E460"),sQuery(id+"F16.wireOp",EDGE,"E461"),sQuery(id+"F16.wireOp",EDGE,"E462"),sQuery(id+"F16.wireOp",EDGE,"E463"),sQuery(id+"F16.wireOp",EDGE,"E464"),sQuery(id+"F16.wireOp",EDGE,"E465"),sQuery(id+"F16.wireOp",EDGE,"E466"),sQuery(id+"F16.wireOp",EDGE,"E467"),sQuery(id+"F16.wireOp",EDGE,"E468"),sQuery(id+"F16.wireOp",EDGE,"E469"),sQuery(id+"F16.wireOp",EDGE,"E470"),sQuery(id+"F16.wireOp",EDGE,"E471"),sQuery(id+"F16.wireOp",EDGE,"E472"),sQuery(id+"F16.wireOp",EDGE,"E473"),sQuery(id+"F16.wireOp",EDGE,"E474"),sQuery(id+"F16.wireOp",EDGE,"E475"),sQuery(id+"F16.wireOp",EDGE,"E476"),sQuery(id+"F16.wireOp",EDGE,"E477")])]});
            var Q7;
            Q7=makeQuery(id+"F17.opExtrude","SWEPT_BODY",BODY,{"disambiguationData":[OSD([sQuery(id+"F16.wireOp",EDGE,"E478"),sQuery(id+"F16.wireOp",EDGE,"E479"),sQuery(id+"F16.wireOp",EDGE,"E480"),sQuery(id+"F16.wireOp",EDGE,"E481"),sQuery(id+"F16.wireOp",EDGE,"E482"),sQuery(id+"F16.wireOp",EDGE,"E483"),sQuery(id+"F16.wireOp",EDGE,"E484"),sQuery(id+"F16.wireOp",EDGE,"E485"),sQuery(id+"F16.wireOp",EDGE,"E486"),sQuery(id+"F16.wireOp",EDGE,"E487"),sQuery(id+"F16.wireOp",EDGE,"E488"),sQuery(id+"F16.wireOp",EDGE,"E489"),sQuery(id+"F16.wireOp",EDGE,"E490"),sQuery(id+"F16.wireOp",EDGE,"E491"),sQuery(id+"F16.wireOp",EDGE,"E492"),sQuery(id+"F16.wireOp",EDGE,"E493"),sQuery(id+"F16.wireOp",EDGE,"E494"),sQuery(id+"F16.wireOp",EDGE,"E495"),sQuery(id+"F16.wireOp",EDGE,"E496"),sQuery(id+"F16.wireOp",EDGE,"E497"),sQuery(id+"F16.wireOp",EDGE,"E498"),sQuery(id+"F16.wireOp",EDGE,"E499"),sQuery(id+"F16.wireOp",EDGE,"E500"),sQuery(id+"F16.wireOp",EDGE,"E501"),sQuery(id+"F16.wireOp",EDGE,"E502"),sQuery(id+"F16.wireOp",EDGE,"E503"),sQuery(id+"F16.wireOp",EDGE,"E504"),sQuery(id+"F16.wireOp",EDGE,"E505"),sQuery(id+"F16.wireOp",EDGE,"E506"),sQuery(id+"F16.wireOp",EDGE,"E507"),sQuery(id+"F16.wireOp",EDGE,"E508"),sQuery(id+"F16.wireOp",EDGE,"E509"),sQuery(id+"F16.wireOp",EDGE,"E510"),sQuery(id+"F16.wireOp",EDGE,"E511"),sQuery(id+"F16.wireOp",EDGE,"E512"),sQuery(id+"F16.wireOp",EDGE,"E513"),sQuery(id+"F16.wireOp",EDGE,"E514"),sQuery(id+"F16.wireOp",EDGE,"E515"),sQuery(id+"F16.wireOp",EDGE,"E516"),sQuery(id+"F16.wireOp",EDGE,"E517"),sQuery(id+"F16.wireOp",EDGE,"E518"),sQuery(id+"F16.wireOp",EDGE,"E519"),sQuery(id+"F16.wireOp",EDGE,"E520"),sQuery(id+"F16.wireOp",EDGE,"E521"),sQuery(id+"F16.wireOp",EDGE,"E522"),sQuery(id+"F16.wireOp",EDGE,"E523"),sQuery(id+"F16.wireOp",EDGE,"E524"),sQuery(id+"F16.wireOp",EDGE,"E525"),sQuery(id+"F16.wireOp",EDGE,"E526"),sQuery(id+"F16.wireOp",EDGE,"E527"),sQuery(id+"F16.wireOp",EDGE,"E528"),sQuery(id+"F16.wireOp",EDGE,"E529"),sQuery(id+"F16.wireOp",EDGE,"E530"),sQuery(id+"F16.wireOp",EDGE,"E531"),sQuery(id+"F16.wireOp",EDGE,"E532"),sQuery(id+"F16.wireOp",EDGE,"E533"),sQuery(id+"F16.wireOp",EDGE,"E534")])]});
            var Q8;
            Q8=makeQuery(id+"F17.opExtrude","SWEPT_BODY",BODY,{"disambiguationData":[OSD([sQuery(id+"F16.wireOp",EDGE,"E535"),sQuery(id+"F16.wireOp",EDGE,"E536"),sQuery(id+"F16.wireOp",EDGE,"E537"),sQuery(id+"F16.wireOp",EDGE,"E538"),sQuery(id+"F16.wireOp",EDGE,"E539"),sQuery(id+"F16.wireOp",EDGE,"E540"),sQuery(id+"F16.wireOp",EDGE,"E541"),sQuery(id+"F16.wireOp",EDGE,"E542"),sQuery(id+"F16.wireOp",EDGE,"E543"),sQuery(id+"F16.wireOp",EDGE,"E544"),sQuery(id+"F16.wireOp",EDGE,"E545"),sQuery(id+"F16.wireOp",EDGE,"E546"),sQuery(id+"F16.wireOp",EDGE,"E547"),sQuery(id+"F16.wireOp",EDGE,"E548"),sQuery(id+"F16.wireOp",EDGE,"E549"),sQuery(id+"F16.wireOp",EDGE,"E550"),sQuery(id+"F16.wireOp",EDGE,"E551"),sQuery(id+"F16.wireOp",EDGE,"E552"),sQuery(id+"F16.wireOp",EDGE,"E553"),sQuery(id+"F16.wireOp",EDGE,"E554"),sQuery(id+"F16.wireOp",EDGE,"E555"),sQuery(id+"F16.wireOp",EDGE,"E556"),sQuery(id+"F16.wireOp",EDGE,"E557"),sQuery(id+"F16.wireOp",EDGE,"E558")])]});
            var Q9;
            Q9=makeQuery(id+"F17.opExtrude","SWEPT_BODY",BODY,{"disambiguationData":[OSD([sQuery(id+"F16.wireOp",EDGE,"E559"),sQuery(id+"F16.wireOp",EDGE,"E560"),sQuery(id+"F16.wireOp",EDGE,"E561"),sQuery(id+"F16.wireOp",EDGE,"E562"),sQuery(id+"F16.wireOp",EDGE,"E563"),sQuery(id+"F16.wireOp",EDGE,"E564"),sQuery(id+"F16.wireOp",EDGE,"E565"),sQuery(id+"F16.wireOp",EDGE,"E566"),sQuery(id+"F16.wireOp",EDGE,"E567"),sQuery(id+"F16.wireOp",EDGE,"E568"),sQuery(id+"F16.wireOp",EDGE,"E569"),sQuery(id+"F16.wireOp",EDGE,"E570"),sQuery(id+"F16.wireOp",EDGE,"E571"),sQuery(id+"F16.wireOp",EDGE,"E572"),sQuery(id+"F16.wireOp",EDGE,"E573"),sQuery(id+"F16.wireOp",EDGE,"E574"),sQuery(id+"F16.wireOp",EDGE,"E575"),sQuery(id+"F16.wireOp",EDGE,"E576"),sQuery(id+"F16.wireOp",EDGE,"E577"),sQuery(id+"F16.wireOp",EDGE,"E578"),sQuery(id+"F16.wireOp",EDGE,"E579"),sQuery(id+"F16.wireOp",EDGE,"E580"),sQuery(id+"F16.wireOp",EDGE,"E581"),sQuery(id+"F16.wireOp",EDGE,"E582"),sQuery(id+"F16.wireOp",EDGE,"E583"),sQuery(id+"F16.wireOp",EDGE,"E584"),sQuery(id+"F16.wireOp",EDGE,"E585"),sQuery(id+"F16.wireOp",EDGE,"E586"),sQuery(id+"F16.wireOp",EDGE,"E587"),sQuery(id+"F16.wireOp",EDGE,"E588"),sQuery(id+"F16.wireOp",EDGE,"E589"),sQuery(id+"F16.wireOp",EDGE,"E590"),sQuery(id+"F16.wireOp",EDGE,"E591"),sQuery(id+"F16.wireOp",EDGE,"E592")])]});
            var Q10;
            Q10=makeQuery(id+"F17.opExtrude","SWEPT_BODY",BODY,{"disambiguationData":[OSD([sQuery(id+"F16.wireOp",EDGE,"E593"),sQuery(id+"F16.wireOp",EDGE,"E594"),sQuery(id+"F16.wireOp",EDGE,"E595"),sQuery(id+"F16.wireOp",EDGE,"E596"),sQuery(id+"F16.wireOp",EDGE,"E597"),sQuery(id+"F16.wireOp",EDGE,"E598"),sQuery(id+"F16.wireOp",EDGE,"E599"),sQuery(id+"F16.wireOp",EDGE,"E600"),sQuery(id+"F16.wireOp",EDGE,"E601"),sQuery(id+"F16.wireOp",EDGE,"E602"),sQuery(id+"F16.wireOp",EDGE,"E603"),sQuery(id+"F16.wireOp",EDGE,"E604"),sQuery(id+"F16.wireOp",EDGE,"E605"),sQuery(id+"F16.wireOp",EDGE,"E606"),sQuery(id+"F16.wireOp",EDGE,"E607"),sQuery(id+"F16.wireOp",EDGE,"E608"),sQuery(id+"F16.wireOp",EDGE,"E609"),sQuery(id+"F16.wireOp",EDGE,"E610"),sQuery(id+"F16.wireOp",EDGE,"E611"),sQuery(id+"F16.wireOp",EDGE,"E612"),sQuery(id+"F16.wireOp",EDGE,"E613"),sQuery(id+"F16.wireOp",EDGE,"E614"),sQuery(id+"F16.wireOp",EDGE,"E615"),sQuery(id+"F16.wireOp",EDGE,"E616"),sQuery(id+"F16.wireOp",EDGE,"E617"),sQuery(id+"F16.wireOp",EDGE,"E618"),sQuery(id+"F16.wireOp",EDGE,"E619"),sQuery(id+"F16.wireOp",EDGE,"E620"),sQuery(id+"F16.wireOp",EDGE,"E621"),sQuery(id+"F16.wireOp",EDGE,"E622"),sQuery(id+"F16.wireOp",EDGE,"E623"),sQuery(id+"F16.wireOp",EDGE,"E624"),sQuery(id+"F16.wireOp",EDGE,"E625"),sQuery(id+"F16.wireOp",EDGE,"E626"),sQuery(id+"F16.wireOp",EDGE,"E627"),sQuery(id+"F16.wireOp",EDGE,"E628"),sQuery(id+"F16.wireOp",EDGE,"E629"),sQuery(id+"F16.wireOp",EDGE,"E630"),sQuery(id+"F16.wireOp",EDGE,"E631")])]});
            var Q11;
            Q11=makeQuery(id+"F17.opExtrude","SWEPT_BODY",BODY,{"disambiguationData":[OSD([sQuery(id+"F16.wireOp",EDGE,"E632"),sQuery(id+"F16.wireOp",EDGE,"E633"),sQuery(id+"F16.wireOp",EDGE,"E634"),sQuery(id+"F16.wireOp",EDGE,"E635"),sQuery(id+"F16.wireOp",EDGE,"E636"),sQuery(id+"F16.wireOp",EDGE,"E637"),sQuery(id+"F16.wireOp",EDGE,"E638"),sQuery(id+"F16.wireOp",EDGE,"E639"),sQuery(id+"F16.wireOp",EDGE,"E640"),sQuery(id+"F16.wireOp",EDGE,"E641"),sQuery(id+"F16.wireOp",EDGE,"E642"),sQuery(id+"F16.wireOp",EDGE,"E643"),sQuery(id+"F16.wireOp",EDGE,"E644"),sQuery(id+"F16.wireOp",EDGE,"E645"),sQuery(id+"F16.wireOp",EDGE,"E646"),sQuery(id+"F16.wireOp",EDGE,"E647"),sQuery(id+"F16.wireOp",EDGE,"E648"),sQuery(id+"F16.wireOp",EDGE,"E649"),sQuery(id+"F16.wireOp",EDGE,"E650"),sQuery(id+"F16.wireOp",EDGE,"E651"),sQuery(id+"F16.wireOp",EDGE,"E652"),sQuery(id+"F16.wireOp",EDGE,"E653"),sQuery(id+"F16.wireOp",EDGE,"E654"),sQuery(id+"F16.wireOp",EDGE,"E655"),sQuery(id+"F16.wireOp",EDGE,"E656"),sQuery(id+"F16.wireOp",EDGE,"E657"),sQuery(id+"F16.wireOp",EDGE,"E658"),sQuery(id+"F16.wireOp",EDGE,"E659"),sQuery(id+"F16.wireOp",EDGE,"E660"),sQuery(id+"F16.wireOp",EDGE,"E661"),sQuery(id+"F16.wireOp",EDGE,"E662"),sQuery(id+"F16.wireOp",EDGE,"E663"),sQuery(id+"F16.wireOp",EDGE,"E664"),sQuery(id+"F16.wireOp",EDGE,"E665"),sQuery(id+"F16.wireOp",EDGE,"E666"),sQuery(id+"F16.wireOp",EDGE,"E667"),sQuery(id+"F16.wireOp",EDGE,"E668"),sQuery(id+"F16.wireOp",EDGE,"E669"),sQuery(id+"F16.wireOp",EDGE,"E670"),sQuery(id+"F16.wireOp",EDGE,"E671"),sQuery(id+"F16.wireOp",EDGE,"E672"),sQuery(id+"F16.wireOp",EDGE,"E673"),sQuery(id+"F16.wireOp",EDGE,"E674"),sQuery(id+"F16.wireOp",EDGE,"E675"),sQuery(id+"F16.wireOp",EDGE,"E676"),sQuery(id+"F16.wireOp",EDGE,"E677"),sQuery(id+"F16.wireOp",EDGE,"E678"),sQuery(id+"F16.wireOp",EDGE,"E679"),sQuery(id+"F16.wireOp",EDGE,"E680"),sQuery(id+"F16.wireOp",EDGE,"E681"),sQuery(id+"F16.wireOp",EDGE,"E682"),sQuery(id+"F16.wireOp",EDGE,"E683"),sQuery(id+"F16.wireOp",EDGE,"E684"),sQuery(id+"F16.wireOp",EDGE,"E685"),sQuery(id+"F16.wireOp",EDGE,"E686"),sQuery(id+"F16.wireOp",EDGE,"E687"),sQuery(id+"F16.wireOp",EDGE,"E688"),sQuery(id+"F16.wireOp",EDGE,"E689"),sQuery(id+"F16.wireOp",EDGE,"E690"),sQuery(id+"F16.wireOp",EDGE,"E691"),sQuery(id+"F16.wireOp",EDGE,"E692"),sQuery(id+"F16.wireOp",EDGE,"E693"),sQuery(id+"F16.wireOp",EDGE,"E694"),sQuery(id+"F16.wireOp",EDGE,"E695")])]});
            var Q12;
            Q12=makeQuery(id+"F17.opExtrude","SWEPT_BODY",BODY,{"disambiguationData":[OSD([sQuery(id+"F16.wireOp",EDGE,"E696"),sQuery(id+"F16.wireOp",EDGE,"E697"),sQuery(id+"F16.wireOp",EDGE,"E698"),sQuery(id+"F16.wireOp",EDGE,"E699"),sQuery(id+"F16.wireOp",EDGE,"E700"),sQuery(id+"F16.wireOp",EDGE,"E701"),sQuery(id+"F16.wireOp",EDGE,"E702"),sQuery(id+"F16.wireOp",EDGE,"E703"),sQuery(id+"F16.wireOp",EDGE,"E704"),sQuery(id+"F16.wireOp",EDGE,"E705"),sQuery(id+"F16.wireOp",EDGE,"E706"),sQuery(id+"F16.wireOp",EDGE,"E707"),sQuery(id+"F16.wireOp",EDGE,"E708"),sQuery(id+"F16.wireOp",EDGE,"E709"),sQuery(id+"F16.wireOp",EDGE,"E710"),sQuery(id+"F16.wireOp",EDGE,"E711"),sQuery(id+"F16.wireOp",EDGE,"E712"),sQuery(id+"F16.wireOp",EDGE,"E713"),sQuery(id+"F16.wireOp",EDGE,"E714"),sQuery(id+"F16.wireOp",EDGE,"E715"),sQuery(id+"F16.wireOp",EDGE,"E716"),sQuery(id+"F16.wireOp",EDGE,"E717"),sQuery(id+"F16.wireOp",EDGE,"E718"),sQuery(id+"F16.wireOp",EDGE,"E719"),sQuery(id+"F16.wireOp",EDGE,"E720"),sQuery(id+"F16.wireOp",EDGE,"E721"),sQuery(id+"F16.wireOp",EDGE,"E722"),sQuery(id+"F16.wireOp",EDGE,"E723"),sQuery(id+"F16.wireOp",EDGE,"E724"),sQuery(id+"F16.wireOp",EDGE,"E725"),sQuery(id+"F16.wireOp",EDGE,"E726"),sQuery(id+"F16.wireOp",EDGE,"E727"),sQuery(id+"F16.wireOp",EDGE,"E728"),sQuery(id+"F16.wireOp",EDGE,"E729"),sQuery(id+"F16.wireOp",EDGE,"E730"),sQuery(id+"F16.wireOp",EDGE,"E731"),sQuery(id+"F16.wireOp",EDGE,"E732"),sQuery(id+"F16.wireOp",EDGE,"E733"),sQuery(id+"F16.wireOp",EDGE,"E734"),sQuery(id+"F16.wireOp",EDGE,"E735"),sQuery(id+"F16.wireOp",EDGE,"E736"),sQuery(id+"F16.wireOp",EDGE,"E737"),sQuery(id+"F16.wireOp",EDGE,"E738"),sQuery(id+"F16.wireOp",EDGE,"E739"),sQuery(id+"F16.wireOp",EDGE,"E740"),sQuery(id+"F16.wireOp",EDGE,"E741"),sQuery(id+"F16.wireOp",EDGE,"E742"),sQuery(id+"F16.wireOp",EDGE,"E743"),sQuery(id+"F16.wireOp",EDGE,"E744"),sQuery(id+"F16.wireOp",EDGE,"E745"),sQuery(id+"F16.wireOp",EDGE,"E746"),sQuery(id+"F16.wireOp",EDGE,"E747"),sQuery(id+"F16.wireOp",EDGE,"E748"),sQuery(id+"F16.wireOp",EDGE,"E749")])]});
            var Q13;
            Q13=makeQuery(id+"F17.opExtrude","SWEPT_BODY",BODY,{"disambiguationData":[OSD([sQuery(id+"F16.wireOp",EDGE,"E750"),sQuery(id+"F16.wireOp",EDGE,"E751"),sQuery(id+"F16.wireOp",EDGE,"E752"),sQuery(id+"F16.wireOp",EDGE,"E753"),sQuery(id+"F16.wireOp",EDGE,"E754"),sQuery(id+"F16.wireOp",EDGE,"E755"),sQuery(id+"F16.wireOp",EDGE,"E756"),sQuery(id+"F16.wireOp",EDGE,"E757"),sQuery(id+"F16.wireOp",EDGE,"E758"),sQuery(id+"F16.wireOp",EDGE,"E759"),sQuery(id+"F16.wireOp",EDGE,"E760"),sQuery(id+"F16.wireOp",EDGE,"E761"),sQuery(id+"F16.wireOp",EDGE,"E762"),sQuery(id+"F16.wireOp",EDGE,"E763"),sQuery(id+"F16.wireOp",EDGE,"E764"),sQuery(id+"F16.wireOp",EDGE,"E765"),sQuery(id+"F16.wireOp",EDGE,"E766"),sQuery(id+"F16.wireOp",EDGE,"E767"),sQuery(id+"F16.wireOp",EDGE,"E768"),sQuery(id+"F16.wireOp",EDGE,"E769"),sQuery(id+"F16.wireOp",EDGE,"E770"),sQuery(id+"F16.wireOp",EDGE,"E771"),sQuery(id+"F16.wireOp",EDGE,"E772"),sQuery(id+"F16.wireOp",EDGE,"E773"),sQuery(id+"F16.wireOp",EDGE,"E774"),sQuery(id+"F16.wireOp",EDGE,"E775"),sQuery(id+"F16.wireOp",EDGE,"E776"),sQuery(id+"F16.wireOp",EDGE,"E777"),sQuery(id+"F16.wireOp",EDGE,"E778"),sQuery(id+"F16.wireOp",EDGE,"E779"),sQuery(id+"F16.wireOp",EDGE,"E780"),sQuery(id+"F16.wireOp",EDGE,"E781"),sQuery(id+"F16.wireOp",EDGE,"E782"),sQuery(id+"F16.wireOp",EDGE,"E783"),sQuery(id+"F16.wireOp",EDGE,"E784"),sQuery(id+"F16.wireOp",EDGE,"E785"),sQuery(id+"F16.wireOp",EDGE,"E786"),sQuery(id+"F16.wireOp",EDGE,"E787"),sQuery(id+"F16.wireOp",EDGE,"E788"),sQuery(id+"F16.wireOp",EDGE,"E789"),sQuery(id+"F16.wireOp",EDGE,"E790"),sQuery(id+"F16.wireOp",EDGE,"E791"),sQuery(id+"F16.wireOp",EDGE,"E792"),sQuery(id+"F16.wireOp",EDGE,"E793"),sQuery(id+"F16.wireOp",EDGE,"E794"),sQuery(id+"F16.wireOp",EDGE,"E795"),sQuery(id+"F16.wireOp",EDGE,"E796"),sQuery(id+"F16.wireOp",EDGE,"E797"),sQuery(id+"F16.wireOp",EDGE,"E798"),sQuery(id+"F16.wireOp",EDGE,"E799"),sQuery(id+"F16.wireOp",EDGE,"E800"),sQuery(id+"F16.wireOp",EDGE,"E801"),sQuery(id+"F16.wireOp",EDGE,"E802"),sQuery(id+"F16.wireOp",EDGE,"E803"),sQuery(id+"F16.wireOp",EDGE,"E804"),sQuery(id+"F16.wireOp",EDGE,"E805"),sQuery(id+"F16.wireOp",EDGE,"E806"),sQuery(id+"F16.wireOp",EDGE,"E807"),sQuery(id+"F16.wireOp",EDGE,"E808"),sQuery(id+"F16.wireOp",EDGE,"E809"),sQuery(id+"F16.wireOp",EDGE,"E810"),sQuery(id+"F16.wireOp",EDGE,"E811"),sQuery(id+"F16.wireOp",EDGE,"E812"),sQuery(id+"F16.wireOp",EDGE,"E813")])]});
            var Q14;
            Q14=makeQuery(id+"F13.opExtrude","SWEPT_BODY",BODY,{"disambiguationData":[OSD([sQuery(id+"F12.wireOp",EDGE,"E46.0")])]});
            booleanBodies(context, id + "F20", {"operationType" : BooleanOperationType.SUBTRACTION, "tools" : qUnion([Q0, Q1, Q2, Q3, Q4, Q5, Q6, Q7, Q8, Q9, Q10, Q11, Q12, Q13]), "targets" : qUnion([Q14])});
        }
    });
